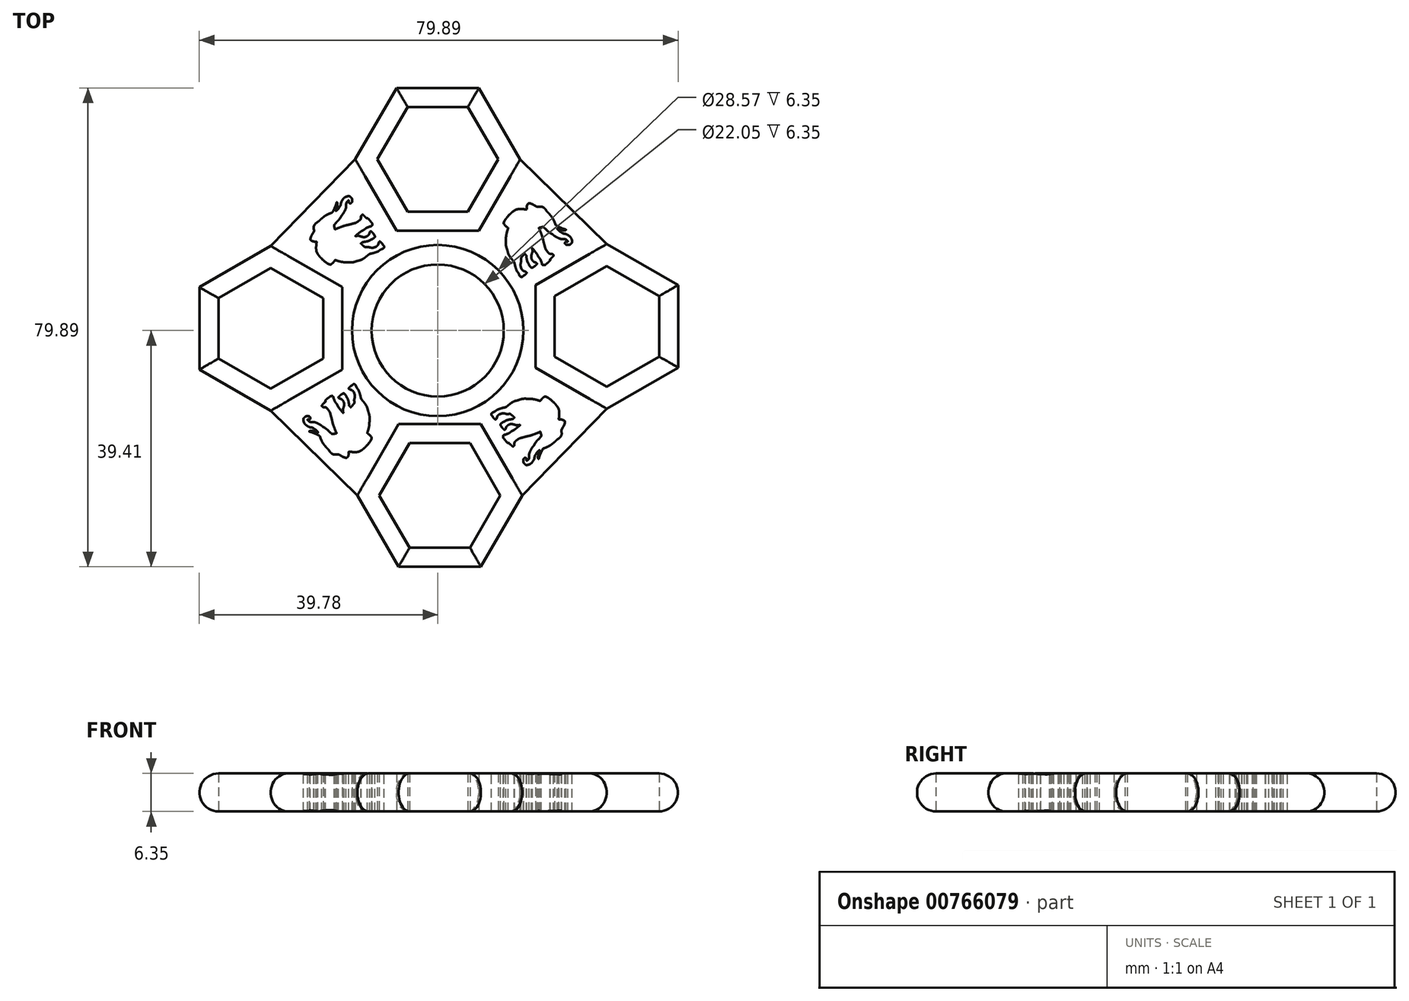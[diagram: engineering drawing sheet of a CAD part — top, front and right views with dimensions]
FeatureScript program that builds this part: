
annotation { "Feature Type Name" : "Feature", "Feature Type Description" : "" }
export const myFeature = defineFeature(function(context is Context, id is Id, definition is map)
    precondition{}
    {
        {
            var Q0;
            Q0=qCreatedBy(makeId("Top.planeOp"),FACE);
            var sketch = newSketch(context, id + "F0", { "sketchPlane" : qUnion([Q0])});
            skCircle(sketch, "E0", {"center": v(0, 0) * mm, "radius": 11.02 * mm});
            skCircle(sketch, "E1", {"center": v(0, 0) * mm, "radius": 14.29 * mm});
            skCircle(sketch, "E2.cCircle", {"center": v(0, 28.58) * mm, "radius": 8.73 * mm, "construction": true});
            skLineSegment(sketch, "E2.0", {"start": v(5.04, 19.84) * mm, "end": v(-5.04, 19.84) * mm});
            skLineSegment(sketch, "E2.1", {"start": v(-5.04, 19.84) * mm, "end": v(-10.08, 28.58) * mm});
            skLineSegment(sketch, "E2.2", {"start": v(-10.08, 28.58) * mm, "end": v(-5.04, 37.3) * mm});
            skLineSegment(sketch, "E2.3", {"start": v(-5.04, 37.3) * mm, "end": v(5.04, 37.3) * mm});
            skLineSegment(sketch, "E2.4", {"start": v(5.04, 37.3) * mm, "end": v(10.08, 28.57) * mm});
            skLineSegment(sketch, "E2.5", {"start": v(10.08, 28.58) * mm, "end": v(5.04, 19.84) * mm});
            skPoint(sketch, "E2.0.midPoint", {"position": v(0, 19.84) * mm});
            skCircle(sketch, "E3.cCircle", {"center": v(0, 28.58) * mm, "radius": 11.9 * mm, "construction": true});
            skLineSegment(sketch, "E3.0", {"start": v(6.87, 16.67) * mm, "end": v(-6.87, 16.67) * mm});
            skLineSegment(sketch, "E3.1", {"start": v(-6.87, 16.67) * mm, "end": v(-13.75, 28.57) * mm});
            skLineSegment(sketch, "E3.2", {"start": v(-13.75, 28.57) * mm, "end": v(-6.87, 40.48) * mm});
            skLineSegment(sketch, "E3.3", {"start": v(-6.87, 40.48) * mm, "end": v(6.87, 40.48) * mm});
            skLineSegment(sketch, "E3.4", {"start": v(6.87, 40.48) * mm, "end": v(13.75, 28.58) * mm});
            skLineSegment(sketch, "E3.5", {"start": v(13.75, 28.58) * mm, "end": v(6.87, 16.67) * mm});
            skPoint(sketch, "E3.0.midPoint", {"position": v(0, 16.67) * mm});
            skLineSegment(sketch, "E4.1.0", {"start": v(-39.78, 7.24) * mm, "end": v(-27.87, 14.11) * mm});
            skLineSegment(sketch, "E4.1.1", {"start": v(-27.87, 14.11) * mm, "end": v(-15.96, 7.24) * mm});
            skPoint(sketch, "E4.1.2", {"position": v(-15.96, 0.37) * mm});
            skCircle(sketch, "E4.1.3", {"center": v(-27.87, 0.37) * mm, "radius": 8.73 * mm, "construction": true});
            skCircle(sketch, "E4.1.4", {"center": v(-27.87, 0.37) * mm, "radius": 11.9 * mm, "construction": true});
            skLineSegment(sketch, "E4.1.5", {"start": v(-15.96, -6.5) * mm, "end": v(-27.87, -13.38) * mm});
            skLineSegment(sketch, "E4.1.6", {"start": v(-27.87, -13.38) * mm, "end": v(-39.78, -6.5) * mm});
            skPoint(sketch, "E4.1.7", {"position": v(-19.14, 0.37) * mm});
            skLineSegment(sketch, "E4.1.8", {"start": v(-36.6, -4.67) * mm, "end": v(-36.6, 5.4) * mm});
            skLineSegment(sketch, "E4.1.9", {"start": v(-39.78, -6.5) * mm, "end": v(-39.78, 7.24) * mm});
            skLineSegment(sketch, "E4.1.10", {"start": v(-19.14, -4.67) * mm, "end": v(-27.87, -9.72) * mm});
            skLineSegment(sketch, "E4.1.11", {"start": v(-27.87, -9.72) * mm, "end": v(-36.6, -4.67) * mm});
            skLineSegment(sketch, "E4.1.12", {"start": v(-19.14, 5.4) * mm, "end": v(-19.14, -4.67) * mm});
            skLineSegment(sketch, "E4.1.13", {"start": v(-36.6, 5.4) * mm, "end": v(-27.87, 10.45) * mm});
            skLineSegment(sketch, "E4.1.14", {"start": v(-27.87, 10.45) * mm, "end": v(-19.14, 5.4) * mm});
            skLineSegment(sketch, "E4.1.15", {"start": v(-15.96, 7.24) * mm, "end": v(-15.96, -6.5) * mm});
            skLineSegment(sketch, "E4.2.0", {"start": v(-6.54, -39.4) * mm, "end": v(-13.4, -27.5) * mm});
            skLineSegment(sketch, "E4.2.1", {"start": v(-13.4, -27.5) * mm, "end": v(-6.54, -15.6) * mm});
            skPoint(sketch, "E4.2.2", {"position": v(0.34, -15.6) * mm});
            skCircle(sketch, "E4.2.3", {"center": v(0.34, -27.5) * mm, "radius": 8.73 * mm, "construction": true});
            skCircle(sketch, "E4.2.4", {"center": v(0.34, -27.5) * mm, "radius": 11.9 * mm, "construction": true});
            skLineSegment(sketch, "E4.2.5", {"start": v(7.21, -15.6) * mm, "end": v(14.09, -27.5) * mm});
            skLineSegment(sketch, "E4.2.6", {"start": v(14.09, -27.5) * mm, "end": v(7.21, -39.4) * mm});
            skPoint(sketch, "E4.2.7", {"position": v(0.34, -18.77) * mm});
            skLineSegment(sketch, "E4.2.8", {"start": v(5.38, -36.23) * mm, "end": v(-4.7, -36.23) * mm});
            skLineSegment(sketch, "E4.2.9", {"start": v(7.21, -39.4) * mm, "end": v(-6.54, -39.4) * mm});
            skLineSegment(sketch, "E4.2.10", {"start": v(5.38, -18.77) * mm, "end": v(10.42, -27.5) * mm});
            skLineSegment(sketch, "E4.2.11", {"start": v(10.42, -27.5) * mm, "end": v(5.38, -36.23) * mm});
            skLineSegment(sketch, "E4.2.12", {"start": v(-4.7, -18.77) * mm, "end": v(5.38, -18.77) * mm});
            skLineSegment(sketch, "E4.2.13", {"start": v(-4.7, -36.23) * mm, "end": v(-9.74, -27.5) * mm});
            skLineSegment(sketch, "E4.2.14", {"start": v(-9.74, -27.5) * mm, "end": v(-4.7, -18.77) * mm});
            skLineSegment(sketch, "E4.2.15", {"start": v(-6.54, -15.6) * mm, "end": v(7.21, -15.6) * mm});
            skLineSegment(sketch, "E4.3.0", {"start": v(40.11, -6.17) * mm, "end": v(28.2, -13.04) * mm});
            skLineSegment(sketch, "E4.3.1", {"start": v(28.2, -13.04) * mm, "end": v(16.3, -6.17) * mm});
            skPoint(sketch, "E4.3.2", {"position": v(16.3, 0.7) * mm});
            skCircle(sketch, "E4.3.3", {"center": v(28.2, 0.7) * mm, "radius": 8.73 * mm, "construction": true});
            skCircle(sketch, "E4.3.4", {"center": v(28.2, 0.7) * mm, "radius": 11.9 * mm, "construction": true});
            skLineSegment(sketch, "E4.3.5", {"start": v(16.3, 7.58) * mm, "end": v(28.2, 14.45) * mm});
            skLineSegment(sketch, "E4.3.6", {"start": v(28.2, 14.45) * mm, "end": v(40.11, 7.58) * mm});
            skPoint(sketch, "E4.3.7", {"position": v(19.48, 0.7) * mm});
            skLineSegment(sketch, "E4.3.8", {"start": v(36.94, 5.75) * mm, "end": v(36.94, -4.34) * mm});
            skLineSegment(sketch, "E4.3.9", {"start": v(40.11, 7.58) * mm, "end": v(40.11, -6.17) * mm});
            skLineSegment(sketch, "E4.3.10", {"start": v(19.48, 5.75) * mm, "end": v(28.2, 10.79) * mm});
            skLineSegment(sketch, "E4.3.11", {"start": v(28.2, 10.79) * mm, "end": v(36.94, 5.75) * mm});
            skLineSegment(sketch, "E4.3.12", {"start": v(19.48, -4.34) * mm, "end": v(19.48, 5.75) * mm});
            skLineSegment(sketch, "E4.3.13", {"start": v(36.94, -4.34) * mm, "end": v(28.2, -9.38) * mm});
            skLineSegment(sketch, "E4.3.14", {"start": v(28.2, -9.38) * mm, "end": v(19.48, -4.34) * mm});
            skLineSegment(sketch, "E4.3.15", {"start": v(16.3, -6.17) * mm, "end": v(16.3, 7.58) * mm});
            skPoint(sketch, "E4.center", {"position": v(0.17, 0.54) * mm});
            skSolve(sketch);
        }
        {
            var Q0;
            Q0=qCreatedBy(makeId("Top.planeOp"),FACE);
            var sketch = newSketch(context, id + "F1", { "sketchPlane" : qUnion([Q0])});
            skLineSegment(sketch, "E5.0", {"start": v(6.87, 40.48) * mm, "end": v(13.75, 28.58) * mm});
            skLineSegment(sketch, "E5.1", {"start": v(-6.87, 40.48) * mm, "end": v(6.87, 40.48) * mm});
            skLineSegment(sketch, "E5.2", {"start": v(14.09, -27.5) * mm, "end": v(7.21, -39.4) * mm});
            skCircle(sketch, "E5.3", {"center": v(0, 28.58) * mm, "radius": 11.9 * mm});
            skLineSegment(sketch, "E5.4", {"start": v(-5.04, 19.84) * mm, "end": v(-10.08, 28.58) * mm});
            skLineSegment(sketch, "E5.5", {"start": v(10.08, 28.58) * mm, "end": v(5.04, 19.84) * mm});
            skLineSegment(sketch, "E5.6", {"start": v(40.11, 7.58) * mm, "end": v(40.11, -6.17) * mm});
            skLineSegment(sketch, "E5.7", {"start": v(5.04, 37.3) * mm, "end": v(10.08, 28.57) * mm});
            skLineSegment(sketch, "E5.8", {"start": v(-5.04, 37.3) * mm, "end": v(5.04, 37.3) * mm});
            skLineSegment(sketch, "E5.9", {"start": v(-10.08, 28.58) * mm, "end": v(-5.04, 37.3) * mm});
            skCircle(sketch, "E5.10", {"center": v(0, 28.58) * mm, "radius": 8.73 * mm});
            skCircle(sketch, "E5.11", {"center": v(0, 0) * mm, "radius": 14.29 * mm});
            skCircle(sketch, "E5.12", {"center": v(0, 0) * mm, "radius": 11.02 * mm});
            skLineSegment(sketch, "E5.13", {"start": v(13.75, 28.58) * mm, "end": v(6.87, 16.67) * mm});
            skLineSegment(sketch, "E5.14", {"start": v(6.87, 16.67) * mm, "end": v(-6.87, 16.67) * mm});
            skLineSegment(sketch, "E5.15", {"start": v(-6.87, 16.67) * mm, "end": v(-13.75, 28.57) * mm});
            skLineSegment(sketch, "E5.16", {"start": v(-13.75, 28.57) * mm, "end": v(-6.87, 40.48) * mm});
            skLineSegment(sketch, "E5.17", {"start": v(-6.54, -15.6) * mm, "end": v(7.21, -15.6) * mm});
            skLineSegment(sketch, "E5.18", {"start": v(-36.6, 5.4) * mm, "end": v(-27.87, 10.45) * mm});
            skLineSegment(sketch, "E5.19", {"start": v(36.94, -4.34) * mm, "end": v(28.2, -9.38) * mm});
            skLineSegment(sketch, "E5.20", {"start": v(-39.78, -6.5) * mm, "end": v(-39.78, 7.24) * mm});
            skLineSegment(sketch, "E5.21", {"start": v(10.42, -27.5) * mm, "end": v(5.38, -36.23) * mm});
            skLineSegment(sketch, "E5.22", {"start": v(-15.96, -6.5) * mm, "end": v(-27.87, -13.38) * mm});
            skLineSegment(sketch, "E5.23", {"start": v(19.48, 5.75) * mm, "end": v(28.2, 10.79) * mm});
            skLineSegment(sketch, "E5.24", {"start": v(28.2, -13.04) * mm, "end": v(16.3, -6.17) * mm});
            skLineSegment(sketch, "E5.25", {"start": v(-15.96, 7.24) * mm, "end": v(-15.96, -6.5) * mm});
            skLineSegment(sketch, "E5.26", {"start": v(5.38, -36.23) * mm, "end": v(-4.7, -36.23) * mm});
            skLineSegment(sketch, "E5.27", {"start": v(-39.78, 7.24) * mm, "end": v(-27.87, 14.11) * mm});
            skLineSegment(sketch, "E5.28", {"start": v(16.3, 7.58) * mm, "end": v(28.2, 14.45) * mm});
            skCircle(sketch, "E5.29", {"center": v(0.34, -27.5) * mm, "radius": 8.73 * mm});
            skLineSegment(sketch, "E5.30", {"start": v(40.11, -6.17) * mm, "end": v(28.2, -13.04) * mm});
            skLineSegment(sketch, "E5.31", {"start": v(-27.87, 10.45) * mm, "end": v(-19.14, 5.4) * mm});
            skLineSegment(sketch, "E5.32", {"start": v(28.2, -9.38) * mm, "end": v(19.48, -4.34) * mm});
            skLineSegment(sketch, "E5.33", {"start": v(-19.14, -4.67) * mm, "end": v(-27.87, -9.72) * mm});
            skLineSegment(sketch, "E5.34", {"start": v(-27.87, -13.38) * mm, "end": v(-39.78, -6.5) * mm});
            skCircle(sketch, "E5.35", {"center": v(28.2, 0.7) * mm, "radius": 8.73 * mm});
            skLineSegment(sketch, "E5.36", {"start": v(28.2, 10.79) * mm, "end": v(36.94, 5.75) * mm});
            skLineSegment(sketch, "E5.37", {"start": v(7.21, -39.4) * mm, "end": v(-6.54, -39.4) * mm});
            skLineSegment(sketch, "E5.38", {"start": v(-6.54, -39.4) * mm, "end": v(-13.4, -27.5) * mm});
            skLineSegment(sketch, "E5.39", {"start": v(-27.87, 14.11) * mm, "end": v(-15.96, 7.24) * mm});
            skLineSegment(sketch, "E5.40", {"start": v(28.2, 14.45) * mm, "end": v(40.11, 7.58) * mm});
            skCircle(sketch, "E5.41", {"center": v(0.34, -27.5) * mm, "radius": 11.9 * mm});
            skLineSegment(sketch, "E5.42", {"start": v(16.3, -6.17) * mm, "end": v(16.3, 7.58) * mm});
            skLineSegment(sketch, "E5.43", {"start": v(-4.7, -36.23) * mm, "end": v(-9.74, -27.5) * mm});
            skLineSegment(sketch, "E5.44", {"start": v(-27.87, -9.72) * mm, "end": v(-36.6, -4.67) * mm});
            skLineSegment(sketch, "E5.45", {"start": v(-36.6, -4.67) * mm, "end": v(-36.6, 5.4) * mm});
            skCircle(sketch, "E5.46", {"center": v(28.2, 0.7) * mm, "radius": 11.9 * mm});
            skLineSegment(sketch, "E5.47", {"start": v(-13.4, -27.5) * mm, "end": v(-6.54, -15.6) * mm});
            skLineSegment(sketch, "E5.48", {"start": v(5.38, -18.77) * mm, "end": v(10.42, -27.5) * mm});
            skCircle(sketch, "E5.49", {"center": v(-27.87, 0.37) * mm, "radius": 8.73 * mm});
            skLineSegment(sketch, "E5.50", {"start": v(36.94, 5.75) * mm, "end": v(36.94, -4.34) * mm});
            skLineSegment(sketch, "E5.51", {"start": v(7.21, -15.6) * mm, "end": v(14.09, -27.5) * mm});
            skCircle(sketch, "E5.52", {"center": v(-27.87, 0.37) * mm, "radius": 11.9 * mm});
            skLineSegment(sketch, "E5.53", {"start": v(-9.74, -27.5) * mm, "end": v(-4.7, -18.77) * mm});
            skLineSegment(sketch, "E5.54", {"start": v(-4.7, -18.77) * mm, "end": v(5.38, -18.77) * mm});
            skLineSegment(sketch, "E6", {"start": v(-27.87, 14.11) * mm, "end": v(-13.75, 28.58) * mm});
            skLineSegment(sketch, "E7", {"start": v(13.75, 28.58) * mm, "end": v(28.2, 14.45) * mm});
            skLineSegment(sketch, "E8", {"start": v(28.2, -13.04) * mm, "end": v(14.09, -27.5) * mm});
            skLineSegment(sketch, "E9", {"start": v(-13.4, -27.5) * mm, "end": v(-27.87, -13.38) * mm});
            skSolve(sketch);
        }
        {
            var Q0;
            Q0=makeQuery(id+"F1.imprint","IMPRINT",FACE,{"disambiguationData":[TD([[makeQuery(id+"F1.imprint","IMPRINT",EDGE,{"derivedFrom":sQuery(id+"F1.wireOp",EDGE,"E5.11")}),-1.0]])]});
            var Q1;
            Q1=makeQuery(id+"F0.imprint","IMPRINT",FACE,{"disambiguationData":[TD([[makeQuery(id+"F0.imprint","IMPRINT",EDGE,{"derivedFrom":sQuery(id+"F0.wireOp",EDGE,"E0")}),-1.0]])]});
            var Q2;
            Q2=makeQuery(id+"F0.imprint","IMPRINT",FACE,{"disambiguationData":[TD([[makeQuery(id+"F0.imprint","IMPRINT",EDGE,{"derivedFrom":sQuery(id+"F0.wireOp",EDGE,"E2.0")}),1.0]])]});
            var Q3;
            Q3=makeQuery(id+"F0.imprint","IMPRINT",FACE,{"disambiguationData":[TD([[makeQuery(id+"F0.imprint","IMPRINT",EDGE,{"derivedFrom":sQuery(id+"F0.wireOp",EDGE,"E4.1.0")}),-1.0]])]});
            var Q4;
            Q4=makeQuery(id+"F0.imprint","IMPRINT",FACE,{"disambiguationData":[TD([[makeQuery(id+"F0.imprint","IMPRINT",EDGE,{"derivedFrom":sQuery(id+"F0.wireOp",EDGE,"E4.3.0")}),-1.0]])]});
            var Q5;
            Q5=makeQuery(id+"F0.imprint","IMPRINT",FACE,{"disambiguationData":[TD([[makeQuery(id+"F0.imprint","IMPRINT",EDGE,{"derivedFrom":sQuery(id+"F0.wireOp",EDGE,"E4.2.0")}),-1.0]])]});
            extrude(context, id + "F2", {"entities" : qUnion([Q0, Q1, Q2, Q3, Q4, Q5]), "depth" : 6.35 * mm, "offsetDistance" : 25.4 * mm});
        }
        {
            var Q0;
            Q0=makeQuery(id+"F2.opExtrude","CAP_FACE",FACE,{"disambiguationData":[OSD([sQuery(id+"F1.wireOp",EDGE,"E5.11"),sQuery(id+"F1.wireOp",EDGE,"E5.13"),sQuery(id+"F1.wireOp",EDGE,"E5.14"),sQuery(id+"F1.wireOp",EDGE,"E5.15"),sQuery(id+"F1.wireOp",EDGE,"E5.17"),sQuery(id+"F1.wireOp",EDGE,"E5.22"),sQuery(id+"F1.wireOp",EDGE,"E5.24"),sQuery(id+"F1.wireOp",EDGE,"E5.25"),sQuery(id+"F1.wireOp",EDGE,"E5.28"),sQuery(id+"F1.wireOp",EDGE,"E5.39"),sQuery(id+"F1.wireOp",EDGE,"E5.42"),sQuery(id+"F1.wireOp",EDGE,"E5.47"),sQuery(id+"F1.wireOp",EDGE,"E5.51"),sQuery(id+"F1.wireOp",EDGE,"E6"),sQuery(id+"F1.wireOp",EDGE,"E7"),sQuery(id+"F1.wireOp",EDGE,"E8"),sQuery(id+"F1.wireOp",EDGE,"E9")])],"isStart":false});
            var sketch = newSketch(context, id + "F3", { "sketchPlane" : qUnion([Q0])});
            skArc(sketch, "E10", {"start": v(12.38, 19.72) * mm, "mid": v(12.3, 19.64) * mm, "end": v(12.2, 19.56) * mm});
            skArc(sketch, "E11", {"start": v(12.2, 19.56) * mm, "mid": v(12.12, 19.49) * mm, "end": v(12.04, 19.41) * mm});
            skArc(sketch, "E12", {"start": v(12.04, 19.41) * mm, "mid": v(11.7, 19.04) * mm, "end": v(11.37, 18.64) * mm});
            skArc(sketch, "E13", {"start": v(11.37, 18.64) * mm, "mid": v(11.27, 18.5) * mm, "end": v(11.18, 18.35) * mm});
            skArc(sketch, "E14", {"start": v(11.18, 18.35) * mm, "mid": v(11.11, 18.22) * mm, "end": v(11.06, 18.09) * mm});
            skArc(sketch, "E15", {"start": v(11.06, 18.09) * mm, "mid": v(11.04, 18.03) * mm, "end": v(11.03, 17.97) * mm});
            skArc(sketch, "E16", {"start": v(11.03, 17.97) * mm, "mid": v(11.02, 17.93) * mm, "end": v(11.02, 17.9) * mm});
            skArc(sketch, "E17", {"start": v(11.02, 17.9) * mm, "mid": v(11.03, 17.87) * mm, "end": v(11.04, 17.84) * mm});
            skArc(sketch, "E18", {"start": v(11.04, 17.84) * mm, "mid": v(11.07, 17.77) * mm, "end": v(11.1, 17.71) * mm});
            skArc(sketch, "E19", {"start": v(11.1, 17.71) * mm, "mid": v(11.22, 17.57) * mm, "end": v(11.34, 17.44) * mm});
            skArc(sketch, "E20", {"start": v(11.34, 17.44) * mm, "mid": v(11.4, 17.4) * mm, "end": v(11.45, 17.34) * mm});
            skArc(sketch, "E21", {"start": v(11.45, 17.34) * mm, "mid": v(11.53, 17.28) * mm, "end": v(11.6, 17.22) * mm});
            skArc(sketch, "E22", {"start": v(11.6, 17.22) * mm, "mid": v(11.66, 17.18) * mm, "end": v(11.73, 17.14) * mm});
            skArc(sketch, "E23", {"start": v(11.73, 17.14) * mm, "mid": v(11.74, 17.13) * mm, "end": v(11.75, 17.12) * mm});
            skArc(sketch, "E24", {"start": v(11.75, 17.12) * mm, "mid": v(11.75, 17.1) * mm, "end": v(11.75, 17.08) * mm});
            skArc(sketch, "E25", {"start": v(11.75, 17.08) * mm, "mid": v(11.73, 17.04) * mm, "end": v(11.72, 16.99) * mm});
            skArc(sketch, "E26", {"start": v(11.72, 16.99) * mm, "mid": v(11.7, 16.96) * mm, "end": v(11.7, 16.93) * mm});
            skArc(sketch, "E27", {"start": v(11.7, 16.93) * mm, "mid": v(11.7, 16.9) * mm, "end": v(11.68, 16.87) * mm});
            skArc(sketch, "E28", {"start": v(11.68, 16.87) * mm, "mid": v(11.67, 16.83) * mm, "end": v(11.66, 16.79) * mm});
            skArc(sketch, "E29", {"start": v(11.66, 16.79) * mm, "mid": v(11.66, 16.77) * mm, "end": v(11.65, 16.75) * mm});
            skArc(sketch, "E30", {"start": v(11.65, 16.75) * mm, "mid": v(11.64, 16.72) * mm, "end": v(11.62, 16.68) * mm});
            skArc(sketch, "E31", {"start": v(11.62, 16.68) * mm, "mid": v(11.62, 16.67) * mm, "end": v(11.62, 16.66) * mm});
            skArc(sketch, "E32", {"start": v(11.62, 16.66) * mm, "mid": v(11.55, 16.4) * mm, "end": v(11.48, 16.15) * mm});
            skArc(sketch, "E33", {"start": v(11.48, 16.15) * mm, "mid": v(11.43, 15.87) * mm, "end": v(11.4, 15.59) * mm});
            skArc(sketch, "E34", {"start": v(11.4, 15.59) * mm, "mid": v(11.4, 15.48) * mm, "end": v(11.4, 15.37) * mm});
            skArc(sketch, "E35", {"start": v(11.4, 15.37) * mm, "mid": v(11.38, 15.13) * mm, "end": v(11.38, 14.9) * mm});
            skArc(sketch, "E36", {"start": v(11.38, 14.9) * mm, "mid": v(11.38, 14.82) * mm, "end": v(11.37, 14.75) * mm});
            skArc(sketch, "E37", {"start": v(11.37, 14.75) * mm, "mid": v(11.36, 14.62) * mm, "end": v(11.37, 14.5) * mm});
            skArc(sketch, "E38", {"start": v(11.37, 14.5) * mm, "mid": v(11.38, 14.34) * mm, "end": v(11.4, 14.18) * mm});
            skArc(sketch, "E39", {"start": v(11.4, 14.18) * mm, "mid": v(11.42, 14.03) * mm, "end": v(11.47, 13.89) * mm});
            skArc(sketch, "E40", {"start": v(11.47, 13.89) * mm, "mid": v(11.59, 13.52) * mm, "end": v(11.69, 13.15) * mm});
            skArc(sketch, "E41", {"start": v(11.69, 13.15) * mm, "mid": v(11.71, 13.05) * mm, "end": v(11.74, 12.96) * mm});
            skArc(sketch, "E42", {"start": v(11.74, 12.96) * mm, "mid": v(11.77, 12.86) * mm, "end": v(11.8, 12.77) * mm});
            skArc(sketch, "E43", {"start": v(11.8, 12.77) * mm, "mid": v(11.83, 12.72) * mm, "end": v(11.85, 12.66) * mm});
            skArc(sketch, "E44", {"start": v(11.85, 12.66) * mm, "mid": v(11.88, 12.6) * mm, "end": v(11.92, 12.55) * mm});
            skArc(sketch, "E45", {"start": v(11.92, 12.55) * mm, "mid": v(11.97, 12.45) * mm, "end": v(12.03, 12.36) * mm});
            skArc(sketch, "E46", {"start": v(12.03, 12.36) * mm, "mid": v(12.06, 12.3) * mm, "end": v(12.1, 12.24) * mm});
            skArc(sketch, "E47", {"start": v(12.1, 12.24) * mm, "mid": v(12.3, 12) * mm, "end": v(12.49, 11.75) * mm});
            skArc(sketch, "E48", {"start": v(12.49, 11.75) * mm, "mid": v(12.6, 11.63) * mm, "end": v(12.7, 11.51) * mm});
            skArc(sketch, "E49", {"start": v(12.7, 11.51) * mm, "mid": v(12.72, 11.48) * mm, "end": v(12.74, 11.45) * mm});
            skArc(sketch, "E50", {"start": v(12.74, 11.45) * mm, "mid": v(12.75, 11.43) * mm, "end": v(12.75, 11.41) * mm});
            skArc(sketch, "E51", {"start": v(12.75, 11.41) * mm, "mid": v(12.78, 11.33) * mm, "end": v(12.8, 11.26) * mm});
            skArc(sketch, "E52", {"start": v(12.8, 11.26) * mm, "mid": v(12.84, 11.15) * mm, "end": v(12.87, 11.03) * mm});
            skArc(sketch, "E53", {"start": v(12.87, 11.03) * mm, "mid": v(12.9, 10.92) * mm, "end": v(12.92, 10.8) * mm});
            skArc(sketch, "E54", {"start": v(12.92, 10.8) * mm, "mid": v(12.93, 10.74) * mm, "end": v(12.95, 10.68) * mm});
            skArc(sketch, "E55", {"start": v(12.95, 10.68) * mm, "mid": v(13, 10.51) * mm, "end": v(13.06, 10.34) * mm});
            skArc(sketch, "E56", {"start": v(13.06, 10.34) * mm, "mid": v(13.12, 10.17) * mm, "end": v(13.19, 10) * mm});
            skArc(sketch, "E57", {"start": v(13.19, 10) * mm, "mid": v(13.22, 9.93) * mm, "end": v(13.26, 9.87) * mm});
            skArc(sketch, "E58", {"start": v(13.26, 9.87) * mm, "mid": v(13.28, 9.84) * mm, "end": v(13.31, 9.8) * mm});
            skArc(sketch, "E59", {"start": v(13.31, 9.8) * mm, "mid": v(13.41, 9.67) * mm, "end": v(13.5, 9.53) * mm});
            skArc(sketch, "E60", {"start": v(13.5, 9.53) * mm, "mid": v(13.53, 9.47) * mm, "end": v(13.55, 9.41) * mm});
            skArc(sketch, "E61", {"start": v(13.55, 9.41) * mm, "mid": v(13.58, 9.36) * mm, "end": v(13.6, 9.3) * mm});
            skArc(sketch, "E62", {"start": v(13.6, 9.3) * mm, "mid": v(13.63, 9.26) * mm, "end": v(13.66, 9.21) * mm});
            skArc(sketch, "E63", {"start": v(13.66, 9.21) * mm, "mid": v(13.67, 9.18) * mm, "end": v(13.68, 9.15) * mm});
            skArc(sketch, "E64", {"start": v(13.68, 9.15) * mm, "mid": v(13.7, 9.12) * mm, "end": v(13.7, 9.1) * mm});
            skArc(sketch, "E65", {"start": v(13.7, 9.1) * mm, "mid": v(13.72, 9.07) * mm, "end": v(13.74, 9.04) * mm});
            skArc(sketch, "E66", {"start": v(13.74, 9.04) * mm, "mid": v(13.77, 9.01) * mm, "end": v(13.81, 8.98) * mm});
            skArc(sketch, "E67", {"start": v(13.81, 8.98) * mm, "mid": v(13.84, 8.97) * mm, "end": v(13.88, 8.96) * mm});
            skArc(sketch, "E68", {"start": v(13.88, 8.96) * mm, "mid": v(13.9, 8.96) * mm, "end": v(13.92, 8.95) * mm});
            skArc(sketch, "E69", {"start": v(13.92, 8.95) * mm, "mid": v(13.94, 8.95) * mm, "end": v(13.96, 8.95) * mm});
            skArc(sketch, "E70", {"start": v(13.96, 8.95) * mm, "mid": v(13.99, 8.94) * mm, "end": v(14.02, 8.94) * mm});
            skArc(sketch, "E71", {"start": v(14.02, 8.94) * mm, "mid": v(14.05, 8.95) * mm, "end": v(14.08, 8.96) * mm});
            skArc(sketch, "E72", {"start": v(14.08, 8.96) * mm, "mid": v(14.1, 8.97) * mm, "end": v(14.12, 9) * mm});
            skArc(sketch, "E73", {"start": v(14.12, 9) * mm, "mid": v(14.16, 9.02) * mm, "end": v(14.2, 9.06) * mm});
            skArc(sketch, "E74", {"start": v(14.2, 9.06) * mm, "mid": v(14.24, 9.1) * mm, "end": v(14.28, 9.12) * mm});
            skArc(sketch, "E75", {"start": v(14.28, 9.12) * mm, "mid": v(14.36, 9.17) * mm, "end": v(14.45, 9.22) * mm});
            skArc(sketch, "E76", {"start": v(14.45, 9.22) * mm, "mid": v(14.5, 9.26) * mm, "end": v(14.56, 9.3) * mm});
            skArc(sketch, "E77", {"start": v(14.56, 9.3) * mm, "mid": v(14.6, 9.34) * mm, "end": v(14.64, 9.38) * mm});
            skArc(sketch, "E78", {"start": v(14.64, 9.38) * mm, "mid": v(14.68, 9.42) * mm, "end": v(14.72, 9.46) * mm});
            skArc(sketch, "E79", {"start": v(14.72, 9.46) * mm, "mid": v(14.75, 9.48) * mm, "end": v(14.77, 9.51) * mm});
            skArc(sketch, "E80", {"start": v(14.77, 9.51) * mm, "mid": v(14.8, 9.56) * mm, "end": v(14.81, 9.6) * mm});
            skArc(sketch, "E81", {"start": v(14.81, 9.6) * mm, "mid": v(14.82, 9.6) * mm, "end": v(14.83, 9.62) * mm});
            skArc(sketch, "E82", {"start": v(14.83, 9.62) * mm, "mid": v(14.84, 9.63) * mm, "end": v(14.85, 9.64) * mm});
            skArc(sketch, "E83", {"start": v(14.85, 9.64) * mm, "mid": v(14.86, 9.65) * mm, "end": v(14.86, 9.66) * mm});
            skArc(sketch, "E84", {"start": v(14.86, 9.66) * mm, "mid": v(14.86, 9.67) * mm, "end": v(14.85, 9.69) * mm});
            skArc(sketch, "E85", {"start": v(14.85, 9.69) * mm, "mid": v(14.8, 9.74) * mm, "end": v(14.75, 9.79) * mm});
            skArc(sketch, "E86", {"start": v(14.75, 9.79) * mm, "mid": v(14.7, 9.82) * mm, "end": v(14.65, 9.83) * mm});
            skArc(sketch, "E87", {"start": v(14.65, 9.83) * mm, "mid": v(14.62, 9.83) * mm, "end": v(14.6, 9.84) * mm});
            skArc(sketch, "E88", {"start": v(14.6, 9.84) * mm, "mid": v(14.56, 9.85) * mm, "end": v(14.53, 9.87) * mm});
            skArc(sketch, "E89", {"start": v(14.53, 9.87) * mm, "mid": v(14.47, 9.9) * mm, "end": v(14.41, 9.91) * mm});
            skArc(sketch, "E90", {"start": v(14.41, 9.91) * mm, "mid": v(14.37, 9.93) * mm, "end": v(14.32, 9.95) * mm});
            skArc(sketch, "E91", {"start": v(14.32, 9.95) * mm, "mid": v(14.26, 9.98) * mm, "end": v(14.21, 10.02) * mm});
            skArc(sketch, "E92", {"start": v(14.21, 10.02) * mm, "mid": v(14.17, 10.05) * mm, "end": v(14.13, 10.1) * mm});
            skArc(sketch, "E93", {"start": v(14.13, 10.1) * mm, "mid": v(14.07, 10.16) * mm, "end": v(14.02, 10.23) * mm});
            skArc(sketch, "E94", {"start": v(14.02, 10.23) * mm, "mid": v(14, 10.26) * mm, "end": v(13.98, 10.28) * mm});
            skArc(sketch, "E95", {"start": v(13.98, 10.28) * mm, "mid": v(13.98, 10.3) * mm, "end": v(13.97, 10.32) * mm});
            skArc(sketch, "E96", {"start": v(13.97, 10.32) * mm, "mid": v(13.96, 10.34) * mm, "end": v(13.95, 10.36) * mm});
            skArc(sketch, "E97", {"start": v(13.95, 10.36) * mm, "mid": v(13.94, 10.4) * mm, "end": v(13.92, 10.45) * mm});
            skArc(sketch, "E98", {"start": v(13.92, 10.45) * mm, "mid": v(13.87, 10.6) * mm, "end": v(13.84, 10.74) * mm});
            skArc(sketch, "E99", {"start": v(13.84, 10.74) * mm, "mid": v(13.82, 10.96) * mm, "end": v(13.84, 11.19) * mm});
            skArc(sketch, "E100", {"start": v(13.84, 11.19) * mm, "mid": v(13.87, 11.3) * mm, "end": v(13.9, 11.4) * mm});
            skArc(sketch, "E101", {"start": v(13.9, 11.4) * mm, "mid": v(13.91, 11.46) * mm, "end": v(13.93, 11.52) * mm});
            skArc(sketch, "E102", {"start": v(13.93, 11.52) * mm, "mid": v(13.93, 11.59) * mm, "end": v(13.93, 11.66) * mm});
            skArc(sketch, "E103", {"start": v(13.93, 11.66) * mm, "mid": v(13.93, 11.72) * mm, "end": v(13.92, 11.78) * mm});
            skArc(sketch, "E104", {"start": v(13.92, 11.78) * mm, "mid": v(13.91, 11.86) * mm, "end": v(13.9, 11.94) * mm});
            skArc(sketch, "E105", {"start": v(13.9, 11.94) * mm, "mid": v(13.9, 11.98) * mm, "end": v(13.9, 12.03) * mm});
            skArc(sketch, "E106", {"start": v(13.9, 12.03) * mm, "mid": v(13.93, 12.12) * mm, "end": v(13.97, 12.2) * mm});
            skArc(sketch, "E107", {"start": v(13.97, 12.2) * mm, "mid": v(14.01, 12.25) * mm, "end": v(14.06, 12.3) * mm});
            skArc(sketch, "E108", {"start": v(14.06, 12.3) * mm, "mid": v(14.1, 12.35) * mm, "end": v(14.14, 12.4) * mm});
            skArc(sketch, "E109", {"start": v(14.14, 12.4) * mm, "mid": v(14.16, 12.42) * mm, "end": v(14.18, 12.44) * mm});
            skArc(sketch, "E110", {"start": v(14.18, 12.44) * mm, "mid": v(14.3, 12.58) * mm, "end": v(14.4, 12.7) * mm});
            skArc(sketch, "E111", {"start": v(14.4, 12.7) * mm, "mid": v(14.43, 12.74) * mm, "end": v(14.46, 12.77) * mm});
            skArc(sketch, "E112", {"start": v(14.46, 12.77) * mm, "mid": v(14.48, 12.79) * mm, "end": v(14.5, 12.8) * mm});
            skArc(sketch, "E113", {"start": v(14.5, 12.8) * mm, "mid": v(14.51, 12.8) * mm, "end": v(14.53, 12.8) * mm});
            skArc(sketch, "E114", {"start": v(14.53, 12.8) * mm, "mid": v(14.55, 12.8) * mm, "end": v(14.56, 12.79) * mm});
            skArc(sketch, "E115", {"start": v(14.56, 12.79) * mm, "mid": v(14.59, 12.76) * mm, "end": v(14.6, 12.73) * mm});
            skArc(sketch, "E116", {"start": v(14.6, 12.73) * mm, "mid": v(14.62, 12.7) * mm, "end": v(14.64, 12.69) * mm});
            skArc(sketch, "E117", {"start": v(14.64, 12.69) * mm, "mid": v(14.65, 12.66) * mm, "end": v(14.67, 12.64) * mm});
            skArc(sketch, "E118", {"start": v(14.67, 12.64) * mm, "mid": v(14.7, 12.6) * mm, "end": v(14.73, 12.57) * mm});
            skArc(sketch, "E119", {"start": v(14.73, 12.57) * mm, "mid": v(14.75, 12.55) * mm, "end": v(14.77, 12.52) * mm});
            skArc(sketch, "E120", {"start": v(14.77, 12.52) * mm, "mid": v(14.77, 12.5) * mm, "end": v(14.78, 12.48) * mm});
            skArc(sketch, "E121", {"start": v(14.78, 12.48) * mm, "mid": v(14.78, 12.43) * mm, "end": v(14.78, 12.39) * mm});
            skArc(sketch, "E122", {"start": v(14.78, 12.39) * mm, "mid": v(14.79, 12.33) * mm, "end": v(14.8, 12.28) * mm});
            skArc(sketch, "E123", {"start": v(14.8, 12.28) * mm, "mid": v(14.82, 12.14) * mm, "end": v(14.84, 12) * mm});
            skArc(sketch, "E124", {"start": v(14.84, 12) * mm, "mid": v(14.88, 11.82) * mm, "end": v(14.92, 11.65) * mm});
            skArc(sketch, "E125", {"start": v(14.92, 11.65) * mm, "mid": v(14.94, 11.57) * mm, "end": v(14.97, 11.5) * mm});
            skArc(sketch, "E126", {"start": v(14.97, 11.5) * mm, "mid": v(14.99, 11.48) * mm, "end": v(15, 11.45) * mm});
            skArc(sketch, "E127", {"start": v(15, 11.45) * mm, "mid": v(15.01, 11.43) * mm, "end": v(15.02, 11.4) * mm});
            skArc(sketch, "E128", {"start": v(15.02, 11.4) * mm, "mid": v(15.03, 11.37) * mm, "end": v(15.05, 11.34) * mm});
            skArc(sketch, "E129", {"start": v(15.05, 11.34) * mm, "mid": v(15.06, 11.32) * mm, "end": v(15.07, 11.3) * mm});
            skArc(sketch, "E130", {"start": v(15.07, 11.3) * mm, "mid": v(15.09, 11.27) * mm, "end": v(15.1, 11.25) * mm});
            skArc(sketch, "E131", {"start": v(15.1, 11.25) * mm, "mid": v(15.12, 11.23) * mm, "end": v(15.13, 11.21) * mm});
            skArc(sketch, "E132", {"start": v(15.13, 11.21) * mm, "mid": v(15.18, 11.12) * mm, "end": v(15.22, 11.02) * mm});
            skArc(sketch, "E133", {"start": v(15.22, 11.02) * mm, "mid": v(15.25, 10.96) * mm, "end": v(15.27, 10.91) * mm});
            skArc(sketch, "E134", {"start": v(15.27, 10.91) * mm, "mid": v(15.3, 10.88) * mm, "end": v(15.32, 10.84) * mm});
            skArc(sketch, "E135", {"start": v(15.32, 10.84) * mm, "mid": v(15.37, 10.78) * mm, "end": v(15.4, 10.71) * mm});
            skArc(sketch, "E136", {"start": v(15.4, 10.71) * mm, "mid": v(15.45, 10.66) * mm, "end": v(15.49, 10.6) * mm});
            skArc(sketch, "E137", {"start": v(15.49, 10.6) * mm, "mid": v(15.54, 10.54) * mm, "end": v(15.61, 10.5) * mm});
            skArc(sketch, "E138", {"start": v(15.61, 10.5) * mm, "mid": v(15.64, 10.5) * mm, "end": v(15.67, 10.48) * mm});
            skArc(sketch, "E139", {"start": v(15.67, 10.48) * mm, "mid": v(15.7, 10.48) * mm, "end": v(15.72, 10.48) * mm});
            skArc(sketch, "E140", {"start": v(15.72, 10.48) * mm, "mid": v(15.77, 10.5) * mm, "end": v(15.82, 10.52) * mm});
            skArc(sketch, "E141", {"start": v(15.82, 10.52) * mm, "mid": v(15.95, 10.59) * mm, "end": v(16.08, 10.67) * mm});
            skArc(sketch, "E142", {"start": v(16.08, 10.67) * mm, "mid": v(16.15, 10.72) * mm, "end": v(16.23, 10.78) * mm});
            skArc(sketch, "E143", {"start": v(16.23, 10.78) * mm, "mid": v(16.32, 10.85) * mm, "end": v(16.4, 10.93) * mm});
            skArc(sketch, "E144", {"start": v(16.4, 10.93) * mm, "mid": v(16.47, 11) * mm, "end": v(16.53, 11.08) * mm});
            skArc(sketch, "E145", {"start": v(16.53, 11.08) * mm, "mid": v(16.55, 11.1) * mm, "end": v(16.56, 11.14) * mm});
            skArc(sketch, "E146", {"start": v(16.56, 11.14) * mm, "mid": v(16.57, 11.15) * mm, "end": v(16.57, 11.17) * mm});
            skArc(sketch, "E147", {"start": v(16.57, 11.17) * mm, "mid": v(16.57, 11.19) * mm, "end": v(16.56, 11.2) * mm});
            skArc(sketch, "E148", {"start": v(16.56, 11.2) * mm, "mid": v(16.55, 11.23) * mm, "end": v(16.53, 11.25) * mm});
            skArc(sketch, "E149", {"start": v(16.53, 11.25) * mm, "mid": v(16.46, 11.3) * mm, "end": v(16.39, 11.34) * mm});
            skArc(sketch, "E150", {"start": v(16.39, 11.34) * mm, "mid": v(16.35, 11.36) * mm, "end": v(16.3, 11.36) * mm});
            skArc(sketch, "E151", {"start": v(16.3, 11.36) * mm, "mid": v(16.26, 11.37) * mm, "end": v(16.22, 11.39) * mm});
            skArc(sketch, "E152", {"start": v(16.22, 11.39) * mm, "mid": v(16.2, 11.4) * mm, "end": v(16.16, 11.42) * mm});
            skArc(sketch, "E153", {"start": v(16.16, 11.42) * mm, "mid": v(16.13, 11.44) * mm, "end": v(16.1, 11.45) * mm});
            skArc(sketch, "E154", {"start": v(16.1, 11.45) * mm, "mid": v(16.07, 11.46) * mm, "end": v(16.04, 11.47) * mm});
            skArc(sketch, "E155", {"start": v(16.04, 11.47) * mm, "mid": v(16.01, 11.49) * mm, "end": v(15.99, 11.5) * mm});
            skArc(sketch, "E156", {"start": v(15.99, 11.5) * mm, "mid": v(15.96, 11.52) * mm, "end": v(15.94, 11.54) * mm});
            skArc(sketch, "E157", {"start": v(15.94, 11.54) * mm, "mid": v(15.9, 11.58) * mm, "end": v(15.87, 11.62) * mm});
            skArc(sketch, "E158", {"start": v(15.87, 11.62) * mm, "mid": v(15.83, 11.67) * mm, "end": v(15.8, 11.71) * mm});
            skArc(sketch, "E159", {"start": v(15.8, 11.71) * mm, "mid": v(15.72, 11.85) * mm, "end": v(15.66, 12) * mm});
            skArc(sketch, "E160", {"start": v(15.66, 12) * mm, "mid": v(15.64, 12.05) * mm, "end": v(15.62, 12.1) * mm});
            skArc(sketch, "E161", {"start": v(15.62, 12.1) * mm, "mid": v(15.61, 12.15) * mm, "end": v(15.6, 12.2) * mm});
            skArc(sketch, "E162", {"start": v(15.6, 12.2) * mm, "mid": v(15.6, 12.35) * mm, "end": v(15.62, 12.5) * mm});
            skArc(sketch, "E163", {"start": v(15.62, 12.5) * mm, "mid": v(15.65, 12.64) * mm, "end": v(15.69, 12.78) * mm});
            skArc(sketch, "E164", {"start": v(15.69, 12.78) * mm, "mid": v(15.73, 12.89) * mm, "end": v(15.77, 13) * mm});
            skArc(sketch, "E165", {"start": v(15.77, 13) * mm, "mid": v(15.79, 13.05) * mm, "end": v(15.8, 13.1) * mm});
            skArc(sketch, "E166", {"start": v(15.8, 13.1) * mm, "mid": v(15.81, 13.15) * mm, "end": v(15.82, 13.2) * mm});
            skArc(sketch, "E167", {"start": v(15.82, 13.2) * mm, "mid": v(15.82, 13.29) * mm, "end": v(15.81, 13.38) * mm});
            skArc(sketch, "E168", {"start": v(15.81, 13.38) * mm, "mid": v(15.8, 13.46) * mm, "end": v(15.79, 13.53) * mm});
            skArc(sketch, "E169", {"start": v(15.79, 13.53) * mm, "mid": v(15.78, 13.58) * mm, "end": v(15.76, 13.63) * mm});
            skArc(sketch, "E170", {"start": v(15.76, 13.63) * mm, "mid": v(15.75, 13.65) * mm, "end": v(15.74, 13.67) * mm});
            skArc(sketch, "E171", {"start": v(15.74, 13.67) * mm, "mid": v(15.74, 13.7) * mm, "end": v(15.75, 13.72) * mm});
            skArc(sketch, "E172", {"start": v(15.75, 13.72) * mm, "mid": v(15.76, 13.73) * mm, "end": v(15.78, 13.73) * mm});
            skArc(sketch, "E173", {"start": v(15.78, 13.73) * mm, "mid": v(15.8, 13.73) * mm, "end": v(15.81, 13.71) * mm});
            skArc(sketch, "E174", {"start": v(15.81, 13.71) * mm, "mid": v(15.83, 13.7) * mm, "end": v(15.84, 13.7) * mm});
            skArc(sketch, "E175", {"start": v(15.84, 13.7) * mm, "mid": v(15.88, 13.65) * mm, "end": v(15.92, 13.6) * mm});
            skArc(sketch, "E176", {"start": v(15.92, 13.6) * mm, "mid": v(15.95, 13.56) * mm, "end": v(15.99, 13.52) * mm});
            skArc(sketch, "E177", {"start": v(15.99, 13.52) * mm, "mid": v(16.13, 13.34) * mm, "end": v(16.28, 13.15) * mm});
            skArc(sketch, "E178", {"start": v(16.28, 13.15) * mm, "mid": v(16.4, 12.99) * mm, "end": v(16.53, 12.82) * mm});
            skArc(sketch, "E179", {"start": v(16.53, 12.82) * mm, "mid": v(16.59, 12.73) * mm, "end": v(16.64, 12.64) * mm});
            skArc(sketch, "E180", {"start": v(16.64, 12.64) * mm, "mid": v(16.67, 12.59) * mm, "end": v(16.7, 12.53) * mm});
            skArc(sketch, "E181", {"start": v(16.7, 12.53) * mm, "mid": v(16.75, 12.42) * mm, "end": v(16.8, 12.32) * mm});
            skArc(sketch, "E182", {"start": v(16.8, 12.32) * mm, "mid": v(16.86, 12.24) * mm, "end": v(16.93, 12.16) * mm});
            skArc(sketch, "E183", {"start": v(16.93, 12.16) * mm, "mid": v(16.99, 12.08) * mm, "end": v(17.05, 12) * mm});
            skArc(sketch, "E184", {"start": v(17.05, 12) * mm, "mid": v(17.08, 11.96) * mm, "end": v(17.12, 11.91) * mm});
            skArc(sketch, "E185", {"start": v(17.12, 11.91) * mm, "mid": v(17.16, 11.84) * mm, "end": v(17.19, 11.77) * mm});
            skArc(sketch, "E186", {"start": v(17.19, 11.77) * mm, "mid": v(17.2, 11.72) * mm, "end": v(17.22, 11.66) * mm});
            skArc(sketch, "E187", {"start": v(17.22, 11.66) * mm, "mid": v(17.24, 11.6) * mm, "end": v(17.27, 11.55) * mm});
            skArc(sketch, "E188", {"start": v(17.27, 11.55) * mm, "mid": v(17.29, 11.5) * mm, "end": v(17.3, 11.46) * mm});
            skArc(sketch, "E189", {"start": v(17.3, 11.46) * mm, "mid": v(17.33, 11.42) * mm, "end": v(17.35, 11.37) * mm});
            skArc(sketch, "E190", {"start": v(17.35, 11.37) * mm, "mid": v(17.36, 11.33) * mm, "end": v(17.37, 11.3) * mm});
            skArc(sketch, "E191", {"start": v(17.37, 11.3) * mm, "mid": v(17.38, 11.22) * mm, "end": v(17.4, 11.15) * mm});
            skArc(sketch, "E192", {"start": v(17.4, 11.15) * mm, "mid": v(17.4, 11.1) * mm, "end": v(17.43, 11.07) * mm});
            skArc(sketch, "E193", {"start": v(17.43, 11.07) * mm, "mid": v(17.46, 11) * mm, "end": v(17.52, 10.96) * mm});
            skArc(sketch, "E194", {"start": v(17.52, 10.96) * mm, "mid": v(17.55, 10.95) * mm, "end": v(17.58, 10.93) * mm});
            skArc(sketch, "E195", {"start": v(17.58, 10.93) * mm, "mid": v(17.6, 10.93) * mm, "end": v(17.63, 10.92) * mm});
            skArc(sketch, "E196", {"start": v(17.63, 10.92) * mm, "mid": v(17.67, 10.92) * mm, "end": v(17.7, 10.93) * mm});
            skArc(sketch, "E197", {"start": v(17.7, 10.93) * mm, "mid": v(17.74, 10.93) * mm, "end": v(17.78, 10.93) * mm});
            skArc(sketch, "E198", {"start": v(17.78, 10.93) * mm, "mid": v(17.82, 10.93) * mm, "end": v(17.86, 10.93) * mm});
            skArc(sketch, "E199", {"start": v(17.86, 10.93) * mm, "mid": v(17.9, 10.95) * mm, "end": v(17.95, 10.97) * mm});
            skArc(sketch, "E200", {"start": v(17.95, 10.97) * mm, "mid": v(17.97, 11) * mm, "end": v(18, 11.01) * mm});
            skArc(sketch, "E201", {"start": v(18, 11.01) * mm, "mid": v(18.04, 11.06) * mm, "end": v(18.08, 11.1) * mm});
            skArc(sketch, "E202", {"start": v(18.08, 11.1) * mm, "mid": v(18.12, 11.13) * mm, "end": v(18.16, 11.16) * mm});
            skArc(sketch, "E203", {"start": v(18.16, 11.16) * mm, "mid": v(18.3, 11.27) * mm, "end": v(18.46, 11.39) * mm});
            skArc(sketch, "E204", {"start": v(18.46, 11.39) * mm, "mid": v(18.56, 11.48) * mm, "end": v(18.66, 11.58) * mm});
            skArc(sketch, "E205", {"start": v(18.66, 11.58) * mm, "mid": v(18.7, 11.62) * mm, "end": v(18.72, 11.65) * mm});
            skArc(sketch, "E206", {"start": v(18.72, 11.65) * mm, "mid": v(18.73, 11.69) * mm, "end": v(18.74, 11.72) * mm});
            skArc(sketch, "E207", {"start": v(18.74, 11.72) * mm, "mid": v(18.75, 11.74) * mm, "end": v(18.75, 11.75) * mm});
            skArc(sketch, "E208", {"start": v(18.75, 11.75) * mm, "mid": v(18.77, 11.77) * mm, "end": v(18.78, 11.78) * mm});
            skArc(sketch, "E209", {"start": v(18.78, 11.78) * mm, "mid": v(18.8, 11.79) * mm, "end": v(18.8, 11.8) * mm});
            skArc(sketch, "E210", {"start": v(18.8, 11.8) * mm, "mid": v(18.79, 11.83) * mm, "end": v(18.77, 11.84) * mm});
            skArc(sketch, "E211", {"start": v(18.77, 11.84) * mm, "mid": v(18.76, 11.86) * mm, "end": v(18.75, 11.87) * mm});
            skArc(sketch, "E212", {"start": v(18.75, 11.87) * mm, "mid": v(18.74, 11.88) * mm, "end": v(18.74, 11.9) * mm});
            skArc(sketch, "E213", {"start": v(18.74, 11.9) * mm, "mid": v(18.74, 11.9) * mm, "end": v(18.75, 11.91) * mm});
            skArc(sketch, "E214", {"start": v(18.75, 11.91) * mm, "mid": v(18.76, 11.92) * mm, "end": v(18.77, 11.93) * mm});
            skArc(sketch, "E215", {"start": v(18.77, 11.93) * mm, "mid": v(18.82, 11.95) * mm, "end": v(18.87, 11.99) * mm});
            skArc(sketch, "E216", {"start": v(18.87, 11.99) * mm, "mid": v(18.93, 12.04) * mm, "end": v(18.98, 12.1) * mm});
            skArc(sketch, "E217", {"start": v(18.98, 12.1) * mm, "mid": v(19.02, 12.15) * mm, "end": v(19.07, 12.2) * mm});
            skArc(sketch, "E218", {"start": v(19.07, 12.2) * mm, "mid": v(19.12, 12.25) * mm, "end": v(19.17, 12.3) * mm});
            skArc(sketch, "E219", {"start": v(19.17, 12.3) * mm, "mid": v(19.21, 12.34) * mm, "end": v(19.25, 12.39) * mm});
            skArc(sketch, "E220", {"start": v(19.25, 12.39) * mm, "mid": v(19.27, 12.41) * mm, "end": v(19.29, 12.44) * mm});
            skArc(sketch, "E221", {"start": v(19.29, 12.44) * mm, "mid": v(19.3, 12.48) * mm, "end": v(19.32, 12.53) * mm});
            skArc(sketch, "E222", {"start": v(19.32, 12.53) * mm, "mid": v(19.33, 12.55) * mm, "end": v(19.33, 12.58) * mm});
            skArc(sketch, "E223", {"start": v(19.33, 12.58) * mm, "mid": v(19.33, 12.6) * mm, "end": v(19.32, 12.63) * mm});
            skArc(sketch, "E224", {"start": v(19.32, 12.63) * mm, "mid": v(19.3, 12.65) * mm, "end": v(19.29, 12.66) * mm});
            skArc(sketch, "E225", {"start": v(19.29, 12.66) * mm, "mid": v(19.25, 12.7) * mm, "end": v(19.2, 12.73) * mm});
            skArc(sketch, "E226", {"start": v(19.2, 12.73) * mm, "mid": v(19.16, 12.75) * mm, "end": v(19.12, 12.77) * mm});
            skArc(sketch, "E227", {"start": v(19.12, 12.77) * mm, "mid": v(19.07, 12.79) * mm, "end": v(19.02, 12.8) * mm});
            skArc(sketch, "E228", {"start": v(19.02, 12.8) * mm, "mid": v(19, 12.8) * mm, "end": v(18.97, 12.8) * mm});
            skArc(sketch, "E229", {"start": v(18.97, 12.8) * mm, "mid": v(18.92, 12.79) * mm, "end": v(18.88, 12.79) * mm});
            skArc(sketch, "E230", {"start": v(18.88, 12.79) * mm, "mid": v(18.83, 12.8) * mm, "end": v(18.77, 12.8) * mm});
            skArc(sketch, "E231", {"start": v(18.77, 12.8) * mm, "mid": v(18.71, 12.82) * mm, "end": v(18.66, 12.84) * mm});
            skArc(sketch, "E232", {"start": v(18.66, 12.84) * mm, "mid": v(18.59, 12.87) * mm, "end": v(18.53, 12.9) * mm});
            skArc(sketch, "E233", {"start": v(18.53, 12.9) * mm, "mid": v(18.5, 12.94) * mm, "end": v(18.47, 12.97) * mm});
            skArc(sketch, "E234", {"start": v(18.47, 12.97) * mm, "mid": v(18.43, 13.01) * mm, "end": v(18.4, 13.05) * mm});
            skArc(sketch, "E235", {"start": v(18.4, 13.05) * mm, "mid": v(18.37, 13.1) * mm, "end": v(18.34, 13.13) * mm});
            skArc(sketch, "E236", {"start": v(18.34, 13.13) * mm, "mid": v(18.28, 13.21) * mm, "end": v(18.22, 13.3) * mm});
            skArc(sketch, "E237", {"start": v(18.22, 13.3) * mm, "mid": v(18.14, 13.41) * mm, "end": v(18.06, 13.53) * mm});
            skArc(sketch, "E238", {"start": v(18.06, 13.53) * mm, "mid": v(18.01, 13.61) * mm, "end": v(17.98, 13.7) * mm});
            skArc(sketch, "E239", {"start": v(17.98, 13.7) * mm, "mid": v(17.94, 13.78) * mm, "end": v(17.92, 13.88) * mm});
            skArc(sketch, "E240", {"start": v(17.92, 13.88) * mm, "mid": v(17.9, 13.97) * mm, "end": v(17.87, 14.06) * mm});
            skArc(sketch, "E241", {"start": v(17.87, 14.06) * mm, "mid": v(17.85, 14.16) * mm, "end": v(17.82, 14.25) * mm});
            skArc(sketch, "E242", {"start": v(17.82, 14.25) * mm, "mid": v(17.78, 14.4) * mm, "end": v(17.74, 14.54) * mm});
            skArc(sketch, "E243", {"start": v(17.74, 14.54) * mm, "mid": v(17.7, 14.68) * mm, "end": v(17.66, 14.83) * mm});
            skArc(sketch, "E244", {"start": v(17.66, 14.83) * mm, "mid": v(17.64, 14.91) * mm, "end": v(17.63, 15) * mm});
            skArc(sketch, "E245", {"start": v(17.63, 15) * mm, "mid": v(17.56, 15.33) * mm, "end": v(17.46, 15.66) * mm});
            skArc(sketch, "E246", {"start": v(17.46, 15.66) * mm, "mid": v(17.42, 15.8) * mm, "end": v(17.37, 15.93) * mm});
            skArc(sketch, "E247", {"start": v(17.37, 15.93) * mm, "mid": v(17.24, 16.26) * mm, "end": v(17.12, 16.59) * mm});
            skArc(sketch, "E248", {"start": v(17.12, 16.59) * mm, "mid": v(17.06, 16.72) * mm, "end": v(17, 16.86) * mm});
            skArc(sketch, "E249", {"start": v(17, 16.86) * mm, "mid": v(16.95, 16.97) * mm, "end": v(16.9, 17.08) * mm});
            skArc(sketch, "E250", {"start": v(16.9, 17.08) * mm, "mid": v(16.89, 17.1) * mm, "end": v(16.88, 17.11) * mm});
            skArc(sketch, "E251", {"start": v(16.88, 17.11) * mm, "mid": v(16.88, 17.13) * mm, "end": v(16.9, 17.14) * mm});
            skArc(sketch, "E252", {"start": v(16.9, 17.14) * mm, "mid": v(16.9, 17.15) * mm, "end": v(16.9, 17.15) * mm});
            skArc(sketch, "E253", {"start": v(16.9, 17.15) * mm, "mid": v(16.95, 17.16) * mm, "end": v(17, 17.17) * mm});
            skArc(sketch, "E254", {"start": v(17, 17.17) * mm, "mid": v(17.09, 17.19) * mm, "end": v(17.18, 17.21) * mm});
            skArc(sketch, "E255", {"start": v(17.18, 17.21) * mm, "mid": v(17.28, 17.24) * mm, "end": v(17.37, 17.26) * mm});
            skArc(sketch, "E256", {"start": v(17.37, 17.26) * mm, "mid": v(17.43, 17.27) * mm, "end": v(17.48, 17.27) * mm});
            skArc(sketch, "E257", {"start": v(17.48, 17.27) * mm, "mid": v(17.53, 17.27) * mm, "end": v(17.58, 17.27) * mm});
            skArc(sketch, "E258", {"start": v(17.58, 17.27) * mm, "mid": v(17.62, 17.26) * mm, "end": v(17.65, 17.25) * mm});
            skArc(sketch, "E259", {"start": v(17.65, 17.25) * mm, "mid": v(17.67, 17.24) * mm, "end": v(17.7, 17.22) * mm});
            skArc(sketch, "E260", {"start": v(17.7, 17.22) * mm, "mid": v(17.72, 17.2) * mm, "end": v(17.74, 17.17) * mm});
            skArc(sketch, "E261", {"start": v(17.74, 17.17) * mm, "mid": v(17.79, 17.12) * mm, "end": v(17.83, 17.08) * mm});
            skArc(sketch, "E262", {"start": v(17.83, 17.08) * mm, "mid": v(17.9, 17.02) * mm, "end": v(17.97, 16.98) * mm});
            skArc(sketch, "E263", {"start": v(17.97, 16.98) * mm, "mid": v(18.05, 16.93) * mm, "end": v(18.1, 16.87) * mm});
            skArc(sketch, "E264", {"start": v(18.1, 16.87) * mm, "mid": v(18.13, 16.85) * mm, "end": v(18.14, 16.83) * mm});
            skArc(sketch, "E265", {"start": v(18.14, 16.83) * mm, "mid": v(18.22, 16.73) * mm, "end": v(18.3, 16.64) * mm});
            skArc(sketch, "E266", {"start": v(18.3, 16.64) * mm, "mid": v(18.43, 16.53) * mm, "end": v(18.56, 16.43) * mm});
            skArc(sketch, "E267", {"start": v(18.56, 16.43) * mm, "mid": v(18.77, 16.28) * mm, "end": v(19, 16.14) * mm});
            skArc(sketch, "E268", {"start": v(19, 16.14) * mm, "mid": v(19.02, 16.12) * mm, "end": v(19.05, 16.11) * mm});
            skArc(sketch, "E269", {"start": v(19.05, 16.11) * mm, "mid": v(19.08, 16.1) * mm, "end": v(19.1, 16.09) * mm});
            skArc(sketch, "E270", {"start": v(19.1, 16.09) * mm, "mid": v(19.13, 16.08) * mm, "end": v(19.15, 16.07) * mm});
            skArc(sketch, "E271", {"start": v(19.15, 16.07) * mm, "mid": v(19.18, 16.05) * mm, "end": v(19.2, 16.03) * mm});
            skArc(sketch, "E272", {"start": v(19.2, 16.03) * mm, "mid": v(19.22, 16.02) * mm, "end": v(19.24, 16) * mm});
            skArc(sketch, "E273", {"start": v(19.24, 16) * mm, "mid": v(19.32, 15.93) * mm, "end": v(19.4, 15.87) * mm});
            skArc(sketch, "E274", {"start": v(19.4, 15.87) * mm, "mid": v(19.54, 15.77) * mm, "end": v(19.69, 15.68) * mm});
            skArc(sketch, "E275", {"start": v(19.69, 15.68) * mm, "mid": v(19.95, 15.53) * mm, "end": v(20.23, 15.4) * mm});
            skArc(sketch, "E276", {"start": v(20.23, 15.4) * mm, "mid": v(20.38, 15.34) * mm, "end": v(20.53, 15.29) * mm});
            skArc(sketch, "E277", {"start": v(20.53, 15.29) * mm, "mid": v(20.63, 15.27) * mm, "end": v(20.73, 15.27) * mm});
            skArc(sketch, "E278", {"start": v(20.73, 15.27) * mm, "mid": v(20.82, 15.27) * mm, "end": v(20.91, 15.27) * mm});
            skArc(sketch, "E279", {"start": v(20.91, 15.27) * mm, "mid": v(21, 15.28) * mm, "end": v(21.1, 15.27) * mm});
            skArc(sketch, "E280", {"start": v(21.1, 15.27) * mm, "mid": v(21.15, 15.26) * mm, "end": v(21.2, 15.26) * mm});
            skArc(sketch, "E281", {"start": v(21.2, 15.26) * mm, "mid": v(21.27, 15.24) * mm, "end": v(21.33, 15.22) * mm});
            skArc(sketch, "E282", {"start": v(21.33, 15.22) * mm, "mid": v(21.4, 15.2) * mm, "end": v(21.45, 15.17) * mm});
            skArc(sketch, "E283", {"start": v(21.45, 15.17) * mm, "mid": v(21.51, 15.13) * mm, "end": v(21.56, 15.08) * mm});
            skArc(sketch, "E284", {"start": v(21.56, 15.08) * mm, "mid": v(21.58, 15.05) * mm, "end": v(21.6, 15.02) * mm});
            skArc(sketch, "E285", {"start": v(21.6, 15.02) * mm, "mid": v(21.62, 15) * mm, "end": v(21.64, 14.98) * mm});
            skArc(sketch, "E286", {"start": v(21.64, 14.98) * mm, "mid": v(21.68, 14.94) * mm, "end": v(21.71, 14.9) * mm});
            skArc(sketch, "E287", {"start": v(21.71, 14.9) * mm, "mid": v(21.72, 14.88) * mm, "end": v(21.72, 14.87) * mm});
            skArc(sketch, "E288", {"start": v(21.72, 14.87) * mm, "mid": v(21.72, 14.85) * mm, "end": v(21.7, 14.84) * mm});
            skArc(sketch, "E289", {"start": v(21.7, 14.84) * mm, "mid": v(21.64, 14.83) * mm, "end": v(21.57, 14.83) * mm});
            skArc(sketch, "E290", {"start": v(21.57, 14.83) * mm, "mid": v(21.54, 14.83) * mm, "end": v(21.52, 14.84) * mm});
            skArc(sketch, "E291", {"start": v(21.52, 14.84) * mm, "mid": v(21.49, 14.84) * mm, "end": v(21.46, 14.84) * mm});
            skArc(sketch, "E292", {"start": v(21.46, 14.84) * mm, "mid": v(21.44, 14.84) * mm, "end": v(21.41, 14.84) * mm});
            skArc(sketch, "E293", {"start": v(21.41, 14.84) * mm, "mid": v(21.38, 14.83) * mm, "end": v(21.35, 14.82) * mm});
            skArc(sketch, "E294", {"start": v(21.35, 14.82) * mm, "mid": v(21.33, 14.8) * mm, "end": v(21.3, 14.8) * mm});
            skArc(sketch, "E295", {"start": v(21.3, 14.8) * mm, "mid": v(21.3, 14.78) * mm, "end": v(21.29, 14.77) * mm});
            skArc(sketch, "E296", {"start": v(21.29, 14.77) * mm, "mid": v(21.28, 14.75) * mm, "end": v(21.27, 14.74) * mm});
            skArc(sketch, "E297", {"start": v(21.27, 14.74) * mm, "mid": v(21.26, 14.7) * mm, "end": v(21.26, 14.67) * mm});
            skArc(sketch, "E298", {"start": v(21.26, 14.67) * mm, "mid": v(21.24, 14.59) * mm, "end": v(21.25, 14.5) * mm});
            skArc(sketch, "E299", {"start": v(21.25, 14.5) * mm, "mid": v(21.25, 14.47) * mm, "end": v(21.27, 14.45) * mm});
            skArc(sketch, "E300", {"start": v(21.27, 14.45) * mm, "mid": v(21.3, 14.44) * mm, "end": v(21.31, 14.43) * mm});
            skArc(sketch, "E301", {"start": v(21.31, 14.43) * mm, "mid": v(21.33, 14.42) * mm, "end": v(21.35, 14.4) * mm});
            skArc(sketch, "E302", {"start": v(21.35, 14.4) * mm, "mid": v(21.36, 14.4) * mm, "end": v(21.36, 14.38) * mm});
            skArc(sketch, "E303", {"start": v(21.36, 14.38) * mm, "mid": v(21.37, 14.37) * mm, "end": v(21.38, 14.37) * mm});
            skArc(sketch, "E304", {"start": v(21.38, 14.37) * mm, "mid": v(21.39, 14.36) * mm, "end": v(21.4, 14.35) * mm});
            skArc(sketch, "E305", {"start": v(21.4, 14.35) * mm, "mid": v(21.41, 14.34) * mm, "end": v(21.42, 14.33) * mm});
            skArc(sketch, "E306", {"start": v(21.42, 14.33) * mm, "mid": v(21.43, 14.32) * mm, "end": v(21.44, 14.3) * mm});
            skArc(sketch, "E307", {"start": v(21.44, 14.3) * mm, "mid": v(21.45, 14.3) * mm, "end": v(21.46, 14.3) * mm});
            skArc(sketch, "E308", {"start": v(21.46, 14.3) * mm, "mid": v(21.48, 14.29) * mm, "end": v(21.5, 14.29) * mm});
            skArc(sketch, "E309", {"start": v(21.5, 14.29) * mm, "mid": v(21.53, 14.3) * mm, "end": v(21.56, 14.3) * mm});
            skArc(sketch, "E310", {"start": v(21.56, 14.3) * mm, "mid": v(21.6, 14.3) * mm, "end": v(21.65, 14.3) * mm});
            skArc(sketch, "E311", {"start": v(21.65, 14.3) * mm, "mid": v(21.74, 14.29) * mm, "end": v(21.83, 14.29) * mm});
            skArc(sketch, "E312", {"start": v(21.83, 14.29) * mm, "mid": v(21.87, 14.29) * mm, "end": v(21.92, 14.3) * mm});
            skArc(sketch, "E313", {"start": v(21.92, 14.3) * mm, "mid": v(21.98, 14.3) * mm, "end": v(22.03, 14.32) * mm});
            skArc(sketch, "E314", {"start": v(22.03, 14.32) * mm, "mid": v(22.06, 14.34) * mm, "end": v(22.1, 14.37) * mm});
            skArc(sketch, "E315", {"start": v(22.1, 14.37) * mm, "mid": v(22.16, 14.41) * mm, "end": v(22.22, 14.46) * mm});
            skArc(sketch, "E316", {"start": v(22.22, 14.46) * mm, "mid": v(22.25, 14.49) * mm, "end": v(22.28, 14.51) * mm});
            skArc(sketch, "E317", {"start": v(22.28, 14.51) * mm, "mid": v(22.3, 14.53) * mm, "end": v(22.32, 14.56) * mm});
            skArc(sketch, "E318", {"start": v(22.32, 14.56) * mm, "mid": v(22.37, 14.63) * mm, "end": v(22.4, 14.7) * mm});
            skArc(sketch, "E319", {"start": v(22.4, 14.7) * mm, "mid": v(22.43, 14.77) * mm, "end": v(22.43, 14.83) * mm});
            skArc(sketch, "E320", {"start": v(22.43, 14.83) * mm, "mid": v(22.44, 14.9) * mm, "end": v(22.43, 14.96) * mm});
            skArc(sketch, "E321", {"start": v(22.43, 14.96) * mm, "mid": v(22.4, 15.05) * mm, "end": v(22.38, 15.15) * mm});
            skArc(sketch, "E322", {"start": v(22.38, 15.15) * mm, "mid": v(22.34, 15.26) * mm, "end": v(22.3, 15.38) * mm});
            skArc(sketch, "E323", {"start": v(22.3, 15.38) * mm, "mid": v(22.2, 15.53) * mm, "end": v(22.1, 15.66) * mm});
            skArc(sketch, "E324", {"start": v(22.1, 15.66) * mm, "mid": v(22.01, 15.74) * mm, "end": v(21.92, 15.81) * mm});
            skArc(sketch, "E325", {"start": v(21.92, 15.81) * mm, "mid": v(21.75, 15.93) * mm, "end": v(21.57, 16.03) * mm});
            skArc(sketch, "E326", {"start": v(21.57, 16.03) * mm, "mid": v(21.48, 16.08) * mm, "end": v(21.38, 16.11) * mm});
            skArc(sketch, "E327", {"start": v(21.38, 16.11) * mm, "mid": v(21.3, 16.14) * mm, "end": v(21.22, 16.16) * mm});
            skArc(sketch, "E328", {"start": v(21.22, 16.16) * mm, "mid": v(21.15, 16.17) * mm, "end": v(21.08, 16.18) * mm});
            skArc(sketch, "E329", {"start": v(21.08, 16.18) * mm, "mid": v(21.01, 16.19) * mm, "end": v(20.94, 16.2) * mm});
            skArc(sketch, "E330", {"start": v(20.94, 16.2) * mm, "mid": v(20.9, 16.23) * mm, "end": v(20.84, 16.25) * mm});
            skArc(sketch, "E331", {"start": v(20.84, 16.25) * mm, "mid": v(20.77, 16.3) * mm, "end": v(20.7, 16.34) * mm});
            skArc(sketch, "E332", {"start": v(20.7, 16.34) * mm, "mid": v(20.66, 16.37) * mm, "end": v(20.61, 16.4) * mm});
            skArc(sketch, "E333", {"start": v(20.61, 16.4) * mm, "mid": v(20.57, 16.43) * mm, "end": v(20.52, 16.46) * mm});
            skArc(sketch, "E334", {"start": v(20.52, 16.46) * mm, "mid": v(20.43, 16.52) * mm, "end": v(20.33, 16.58) * mm});
            skArc(sketch, "E335", {"start": v(20.33, 16.58) * mm, "mid": v(20.28, 16.6) * mm, "end": v(20.23, 16.64) * mm});
            skArc(sketch, "E336", {"start": v(20.23, 16.64) * mm, "mid": v(20.18, 16.7) * mm, "end": v(20.14, 16.75) * mm});
            skArc(sketch, "E337", {"start": v(20.14, 16.75) * mm, "mid": v(20.08, 16.82) * mm, "end": v(20.03, 16.9) * mm});
            skArc(sketch, "E338", {"start": v(20.03, 16.9) * mm, "mid": v(20, 16.93) * mm, "end": v(19.98, 16.97) * mm});
            skArc(sketch, "E339", {"start": v(19.98, 16.97) * mm, "mid": v(19.98, 16.98) * mm, "end": v(19.97, 17) * mm});
            skArc(sketch, "E340", {"start": v(19.97, 17) * mm, "mid": v(19.97, 17) * mm, "end": v(19.97, 17.01) * mm});
            skArc(sketch, "E341", {"start": v(19.97, 17.01) * mm, "mid": v(19.98, 17.02) * mm, "end": v(19.98, 17.02) * mm});
            skArc(sketch, "E342", {"start": v(19.98, 17.02) * mm, "mid": v(20, 17.02) * mm, "end": v(20, 17.02) * mm});
            skArc(sketch, "E343", {"start": v(20, 17.02) * mm, "mid": v(20.05, 17) * mm, "end": v(20.1, 17) * mm});
            skArc(sketch, "E344", {"start": v(20.1, 17) * mm, "mid": v(20.15, 16.97) * mm, "end": v(20.2, 16.96) * mm});
            skArc(sketch, "E345", {"start": v(20.2, 16.96) * mm, "mid": v(20.31, 16.93) * mm, "end": v(20.42, 16.9) * mm});
            skArc(sketch, "E346", {"start": v(20.42, 16.9) * mm, "mid": v(20.52, 16.86) * mm, "end": v(20.61, 16.83) * mm});
            skArc(sketch, "E347", {"start": v(20.61, 16.83) * mm, "mid": v(20.71, 16.8) * mm, "end": v(20.81, 16.77) * mm});
            skArc(sketch, "E348", {"start": v(20.81, 16.77) * mm, "mid": v(20.92, 16.74) * mm, "end": v(21.03, 16.73) * mm});
            skArc(sketch, "E349", {"start": v(21.03, 16.73) * mm, "mid": v(21.14, 16.73) * mm, "end": v(21.25, 16.74) * mm});
            skArc(sketch, "E350", {"start": v(21.25, 16.74) * mm, "mid": v(21.31, 16.75) * mm, "end": v(21.37, 16.78) * mm});
            skArc(sketch, "E351", {"start": v(21.37, 16.78) * mm, "mid": v(21.4, 16.79) * mm, "end": v(21.4, 16.8) * mm});
            skArc(sketch, "E352", {"start": v(21.4, 16.8) * mm, "mid": v(21.41, 16.82) * mm, "end": v(21.42, 16.83) * mm});
            skArc(sketch, "E353", {"start": v(21.42, 16.83) * mm, "mid": v(21.41, 16.84) * mm, "end": v(21.4, 16.85) * mm});
            skArc(sketch, "E354", {"start": v(21.4, 16.85) * mm, "mid": v(21.39, 16.86) * mm, "end": v(21.37, 16.87) * mm});
            skArc(sketch, "E355", {"start": v(21.37, 16.87) * mm, "mid": v(21.34, 16.88) * mm, "end": v(21.31, 16.88) * mm});
            skArc(sketch, "E356", {"start": v(21.31, 16.88) * mm, "mid": v(21.25, 16.9) * mm, "end": v(21.2, 16.9) * mm});
            skArc(sketch, "E357", {"start": v(21.2, 16.9) * mm, "mid": v(20.98, 16.98) * mm, "end": v(20.78, 17.05) * mm});
            skArc(sketch, "E358", {"start": v(20.78, 17.05) * mm, "mid": v(20.63, 17.11) * mm, "end": v(20.49, 17.18) * mm});
            skArc(sketch, "E359", {"start": v(20.49, 17.18) * mm, "mid": v(20.16, 17.34) * mm, "end": v(19.84, 17.5) * mm});
            skArc(sketch, "E360", {"start": v(19.84, 17.5) * mm, "mid": v(19.79, 17.54) * mm, "end": v(19.73, 17.57) * mm});
            skArc(sketch, "E361", {"start": v(19.73, 17.57) * mm, "mid": v(19.7, 17.6) * mm, "end": v(19.66, 17.66) * mm});
            skArc(sketch, "E362", {"start": v(19.66, 17.66) * mm, "mid": v(19.65, 17.69) * mm, "end": v(19.64, 17.72) * mm});
            skArc(sketch, "E363", {"start": v(19.64, 17.72) * mm, "mid": v(19.64, 17.75) * mm, "end": v(19.63, 17.78) * mm});
            skArc(sketch, "E364", {"start": v(19.63, 17.78) * mm, "mid": v(19.58, 17.9) * mm, "end": v(19.54, 18.02) * mm});
            skArc(sketch, "E365", {"start": v(19.54, 18.02) * mm, "mid": v(19.46, 18.2) * mm, "end": v(19.38, 18.38) * mm});
            skArc(sketch, "E366", {"start": v(19.38, 18.38) * mm, "mid": v(19.3, 18.54) * mm, "end": v(19.21, 18.7) * mm});
            skArc(sketch, "E367", {"start": v(19.21, 18.7) * mm, "mid": v(19.12, 18.84) * mm, "end": v(19.02, 18.98) * mm});
            skArc(sketch, "E368", {"start": v(19.02, 18.98) * mm, "mid": v(18.96, 19.05) * mm, "end": v(18.9, 19.12) * mm});
            skArc(sketch, "E369", {"start": v(18.9, 19.12) * mm, "mid": v(18.8, 19.24) * mm, "end": v(18.7, 19.37) * mm});
            skArc(sketch, "E370", {"start": v(18.7, 19.37) * mm, "mid": v(18.63, 19.47) * mm, "end": v(18.55, 19.56) * mm});
            skArc(sketch, "E371", {"start": v(18.55, 19.56) * mm, "mid": v(18.46, 19.64) * mm, "end": v(18.38, 19.72) * mm});
            skArc(sketch, "E372", {"start": v(18.38, 19.72) * mm, "mid": v(18.31, 19.8) * mm, "end": v(18.25, 19.87) * mm});
            skArc(sketch, "E373", {"start": v(18.25, 19.87) * mm, "mid": v(18.16, 19.97) * mm, "end": v(18.08, 20.09) * mm});
            skArc(sketch, "E374", {"start": v(18.08, 20.09) * mm, "mid": v(18.04, 20.16) * mm, "end": v(18, 20.23) * mm});
            skArc(sketch, "E375", {"start": v(18, 20.23) * mm, "mid": v(17.93, 20.32) * mm, "end": v(17.85, 20.4) * mm});
            skArc(sketch, "E376", {"start": v(17.85, 20.4) * mm, "mid": v(17.7, 20.53) * mm, "end": v(17.51, 20.63) * mm});
            skArc(sketch, "E377", {"start": v(17.51, 20.63) * mm, "mid": v(17.34, 20.68) * mm, "end": v(17.17, 20.7) * mm});
            skArc(sketch, "E378", {"start": v(17.17, 20.7) * mm, "mid": v(17.1, 20.7) * mm, "end": v(17.05, 20.68) * mm});
            skArc(sketch, "E379", {"start": v(17.05, 20.68) * mm, "mid": v(16.93, 20.67) * mm, "end": v(16.82, 20.65) * mm});
            skArc(sketch, "E380", {"start": v(16.82, 20.65) * mm, "mid": v(16.73, 20.65) * mm, "end": v(16.64, 20.65) * mm});
            skArc(sketch, "E381", {"start": v(16.64, 20.65) * mm, "mid": v(16.6, 20.65) * mm, "end": v(16.57, 20.66) * mm});
            skArc(sketch, "E382", {"start": v(16.57, 20.66) * mm, "mid": v(16.53, 20.67) * mm, "end": v(16.49, 20.7) * mm});
            skArc(sketch, "E383", {"start": v(16.49, 20.7) * mm, "mid": v(16.39, 20.75) * mm, "end": v(16.3, 20.8) * mm});
            skArc(sketch, "E384", {"start": v(16.3, 20.8) * mm, "mid": v(16.16, 20.88) * mm, "end": v(16.02, 20.96) * mm});
            skArc(sketch, "E385", {"start": v(16.02, 20.96) * mm, "mid": v(15.92, 21.02) * mm, "end": v(15.82, 21.07) * mm});
            skArc(sketch, "E386", {"start": v(15.82, 21.07) * mm, "mid": v(15.66, 21.14) * mm, "end": v(15.5, 21.2) * mm});
            skArc(sketch, "E387", {"start": v(15.5, 21.2) * mm, "mid": v(15.4, 21.22) * mm, "end": v(15.27, 21.24) * mm});
            skArc(sketch, "E388", {"start": v(15.27, 21.24) * mm, "mid": v(15.2, 21.23) * mm, "end": v(15.14, 21.2) * mm});
            skArc(sketch, "E389", {"start": v(15.14, 21.2) * mm, "mid": v(15.1, 21.17) * mm, "end": v(15.05, 21.12) * mm});
            skArc(sketch, "E390", {"start": v(15.05, 21.12) * mm, "mid": v(15, 21.07) * mm, "end": v(14.96, 21) * mm});
            skArc(sketch, "E391", {"start": v(14.96, 21) * mm, "mid": v(14.9, 20.85) * mm, "end": v(14.86, 20.68) * mm});
            skArc(sketch, "E392", {"start": v(14.86, 20.68) * mm, "mid": v(14.85, 20.6) * mm, "end": v(14.85, 20.52) * mm});
            skArc(sketch, "E393", {"start": v(14.85, 20.52) * mm, "mid": v(14.84, 20.43) * mm, "end": v(14.85, 20.33) * mm});
            skArc(sketch, "E394", {"start": v(14.85, 20.33) * mm, "mid": v(14.85, 20.29) * mm, "end": v(14.85, 20.25) * mm});
            skArc(sketch, "E395", {"start": v(14.85, 20.25) * mm, "mid": v(14.85, 20.23) * mm, "end": v(14.84, 20.22) * mm});
            skArc(sketch, "E396", {"start": v(14.84, 20.22) * mm, "mid": v(14.83, 20.2) * mm, "end": v(14.81, 20.2) * mm});
            skArc(sketch, "E397", {"start": v(14.81, 20.2) * mm, "mid": v(14.78, 20.2) * mm, "end": v(14.75, 20.2) * mm});
            skArc(sketch, "E398", {"start": v(14.75, 20.2) * mm, "mid": v(14.72, 20.2) * mm, "end": v(14.7, 20.22) * mm});
            skArc(sketch, "E399", {"start": v(14.7, 20.22) * mm, "mid": v(14.66, 20.22) * mm, "end": v(14.63, 20.23) * mm});
            skArc(sketch, "E400", {"start": v(14.63, 20.23) * mm, "mid": v(14.57, 20.23) * mm, "end": v(14.5, 20.24) * mm});
            skArc(sketch, "E401", {"start": v(14.5, 20.24) * mm, "mid": v(14.38, 20.25) * mm, "end": v(14.26, 20.26) * mm});
            skArc(sketch, "E402", {"start": v(14.26, 20.26) * mm, "mid": v(13.98, 20.28) * mm, "end": v(13.7, 20.28) * mm});
            skArc(sketch, "E403", {"start": v(13.7, 20.28) * mm, "mid": v(13.54, 20.27) * mm, "end": v(13.37, 20.25) * mm});
            skArc(sketch, "E404", {"start": v(13.37, 20.25) * mm, "mid": v(13.26, 20.23) * mm, "end": v(13.16, 20.2) * mm});
            skArc(sketch, "E405", {"start": v(13.16, 20.2) * mm, "mid": v(13.07, 20.17) * mm, "end": v(12.98, 20.13) * mm});
            skArc(sketch, "E406", {"start": v(12.98, 20.13) * mm, "mid": v(12.9, 20.09) * mm, "end": v(12.83, 20.05) * mm});
            skArc(sketch, "E407", {"start": v(12.83, 20.05) * mm, "mid": v(12.71, 19.98) * mm, "end": v(12.6, 19.9) * mm});
            skArc(sketch, "E408", {"start": v(12.6, 19.9) * mm, "mid": v(12.55, 19.87) * mm, "end": v(12.5, 19.83) * mm});
            skArc(sketch, "E409", {"start": v(12.5, 19.83) * mm, "mid": v(12.44, 19.77) * mm, "end": v(12.38, 19.72) * mm});
            skArc(sketch, "E410.1.0", {"start": v(-20.05, 12.83) * mm, "mid": v(-19.98, 12.71) * mm, "end": v(-19.9, 12.6) * mm});
            skArc(sketch, "E410.1.1", {"start": v(-19.83, 12.5) * mm, "mid": v(-19.77, 12.44) * mm, "end": v(-19.72, 12.38) * mm});
            skArc(sketch, "E410.1.2", {"start": v(-19.41, 12.04) * mm, "mid": v(-19.04, 11.7) * mm, "end": v(-18.64, 11.37) * mm});
            skArc(sketch, "E410.1.3", {"start": v(-20.13, 12.98) * mm, "mid": v(-20.09, 12.9) * mm, "end": v(-20.05, 12.83) * mm});
            skArc(sketch, "E410.1.4", {"start": v(-19.9, 12.6) * mm, "mid": v(-19.87, 12.55) * mm, "end": v(-19.83, 12.5) * mm});
            skArc(sketch, "E410.1.5", {"start": v(-19.56, 18.55) * mm, "mid": v(-19.64, 18.46) * mm, "end": v(-19.72, 18.38) * mm});
            skArc(sketch, "E410.1.6", {"start": v(-19.56, 12.2) * mm, "mid": v(-19.49, 12.12) * mm, "end": v(-19.41, 12.04) * mm});
            skArc(sketch, "E410.1.7", {"start": v(-20.23, 18) * mm, "mid": v(-20.32, 17.93) * mm, "end": v(-20.4, 17.85) * mm});
            skArc(sketch, "E410.1.8", {"start": v(-20.4, 17.85) * mm, "mid": v(-20.53, 17.7) * mm, "end": v(-20.63, 17.51) * mm});
            skArc(sketch, "E410.1.9", {"start": v(-20.68, 17.05) * mm, "mid": v(-20.67, 16.93) * mm, "end": v(-20.65, 16.82) * mm});
            skArc(sketch, "E410.1.10", {"start": v(-20.65, 16.82) * mm, "mid": v(-20.65, 16.73) * mm, "end": v(-20.65, 16.64) * mm});
            skArc(sketch, "E410.1.11", {"start": v(-20.66, 16.57) * mm, "mid": v(-20.67, 16.53) * mm, "end": v(-20.7, 16.49) * mm});
            skArc(sketch, "E410.1.12", {"start": v(-19.37, 18.7) * mm, "mid": v(-19.47, 18.63) * mm, "end": v(-19.56, 18.55) * mm});
            skArc(sketch, "E410.1.13", {"start": v(-19.72, 12.38) * mm, "mid": v(-19.64, 12.3) * mm, "end": v(-19.56, 12.2) * mm});
            skArc(sketch, "E410.1.14", {"start": v(-19.87, 18.25) * mm, "mid": v(-19.97, 18.16) * mm, "end": v(-20.09, 18.08) * mm});
            skArc(sketch, "E410.1.15", {"start": v(-20.09, 18.08) * mm, "mid": v(-20.16, 18.04) * mm, "end": v(-20.23, 18) * mm});
            skArc(sketch, "E410.1.16", {"start": v(-20.7, 17.17) * mm, "mid": v(-20.7, 17.1) * mm, "end": v(-20.68, 17.05) * mm});
            skArc(sketch, "E410.1.17", {"start": v(-20.65, 16.64) * mm, "mid": v(-20.65, 16.6) * mm, "end": v(-20.66, 16.57) * mm});
            skArc(sketch, "E410.1.18", {"start": v(-19.72, 18.38) * mm, "mid": v(-19.8, 18.31) * mm, "end": v(-19.87, 18.25) * mm});
            skArc(sketch, "E410.1.19", {"start": v(-20.63, 17.51) * mm, "mid": v(-20.68, 17.34) * mm, "end": v(-20.7, 17.17) * mm});
            skArc(sketch, "E410.1.20", {"start": v(-18.64, 11.37) * mm, "mid": v(-18.5, 11.27) * mm, "end": v(-18.35, 11.18) * mm});
            skArc(sketch, "E410.1.21", {"start": v(-20.25, 13.37) * mm, "mid": v(-20.23, 13.26) * mm, "end": v(-20.2, 13.16) * mm});
            skArc(sketch, "E410.1.22", {"start": v(-20.2, 13.16) * mm, "mid": v(-20.17, 13.07) * mm, "end": v(-20.13, 12.98) * mm});
            skArc(sketch, "E410.1.23", {"start": v(-13.89, 11.47) * mm, "mid": v(-13.52, 11.59) * mm, "end": v(-13.15, 11.69) * mm});
            skArc(sketch, "E410.1.24", {"start": v(-18.7, 19.21) * mm, "mid": v(-18.84, 19.12) * mm, "end": v(-18.98, 19.02) * mm});
            skArc(sketch, "E410.1.25", {"start": v(-19.12, 18.9) * mm, "mid": v(-19.24, 18.8) * mm, "end": v(-19.37, 18.7) * mm});
            skArc(sketch, "E410.1.26", {"start": v(-20.28, 13.7) * mm, "mid": v(-20.27, 13.54) * mm, "end": v(-20.25, 13.37) * mm});
            skArc(sketch, "E410.1.27", {"start": v(-14.18, 11.4) * mm, "mid": v(-14.03, 11.42) * mm, "end": v(-13.89, 11.47) * mm});
            skArc(sketch, "E410.1.28", {"start": v(-12.96, 11.74) * mm, "mid": v(-12.86, 11.77) * mm, "end": v(-12.77, 11.8) * mm});
            skArc(sketch, "E410.1.29", {"start": v(-18.38, 19.38) * mm, "mid": v(-18.54, 19.3) * mm, "end": v(-18.7, 19.21) * mm});
            skArc(sketch, "E410.1.30", {"start": v(-18.98, 19.02) * mm, "mid": v(-19.05, 18.96) * mm, "end": v(-19.12, 18.9) * mm});
            skArc(sketch, "E410.1.31", {"start": v(-15.37, 11.4) * mm, "mid": v(-15.13, 11.38) * mm, "end": v(-14.9, 11.38) * mm});
            skArc(sketch, "E410.1.32", {"start": v(-14.9, 11.38) * mm, "mid": v(-14.82, 11.38) * mm, "end": v(-14.75, 11.37) * mm});
            skArc(sketch, "E410.1.33", {"start": v(-14.75, 11.37) * mm, "mid": v(-14.62, 11.36) * mm, "end": v(-14.5, 11.37) * mm});
            skArc(sketch, "E410.1.34", {"start": v(-14.5, 11.37) * mm, "mid": v(-14.34, 11.38) * mm, "end": v(-14.18, 11.4) * mm});
            skArc(sketch, "E410.1.35", {"start": v(-13.15, 11.69) * mm, "mid": v(-13.05, 11.71) * mm, "end": v(-12.96, 11.74) * mm});
            skArc(sketch, "E410.1.36", {"start": v(-12.66, 11.85) * mm, "mid": v(-12.6, 11.88) * mm, "end": v(-12.55, 11.92) * mm});
            skArc(sketch, "E410.1.37", {"start": v(-12.36, 12.03) * mm, "mid": v(-12.3, 12.06) * mm, "end": v(-12.24, 12.1) * mm});
            skArc(sketch, "E410.1.38", {"start": v(-12.24, 12.1) * mm, "mid": v(-12, 12.3) * mm, "end": v(-11.75, 12.49) * mm});
            skArc(sketch, "E410.1.39", {"start": v(-12.77, 11.8) * mm, "mid": v(-12.72, 11.83) * mm, "end": v(-12.66, 11.85) * mm});
            skArc(sketch, "E410.1.40", {"start": v(-12.55, 11.92) * mm, "mid": v(-12.45, 11.97) * mm, "end": v(-12.36, 12.03) * mm});
            skArc(sketch, "E410.1.41", {"start": v(-16.66, 11.62) * mm, "mid": v(-16.4, 11.55) * mm, "end": v(-16.15, 11.48) * mm});
            skArc(sketch, "E410.1.42", {"start": v(-16.15, 11.48) * mm, "mid": v(-15.87, 11.43) * mm, "end": v(-15.59, 11.4) * mm});
            skArc(sketch, "E410.1.43", {"start": v(-15.59, 11.4) * mm, "mid": v(-15.48, 11.4) * mm, "end": v(-15.37, 11.4) * mm});
            skArc(sketch, "E410.1.44", {"start": v(-17.9, 11.02) * mm, "mid": v(-17.87, 11.03) * mm, "end": v(-17.84, 11.04) * mm});
            skArc(sketch, "E410.1.45", {"start": v(-17.84, 11.04) * mm, "mid": v(-17.77, 11.07) * mm, "end": v(-17.71, 11.1) * mm});
            skArc(sketch, "E410.1.46", {"start": v(-17.44, 11.34) * mm, "mid": v(-17.4, 11.4) * mm, "end": v(-17.34, 11.45) * mm});
            skArc(sketch, "E410.1.47", {"start": v(-17.22, 11.6) * mm, "mid": v(-17.18, 11.66) * mm, "end": v(-17.14, 11.73) * mm});
            skArc(sketch, "E410.1.48", {"start": v(-21, 14.96) * mm, "mid": v(-20.85, 14.9) * mm, "end": v(-20.68, 14.86) * mm});
            skArc(sketch, "E410.1.49", {"start": v(-20.52, 14.85) * mm, "mid": v(-20.43, 14.84) * mm, "end": v(-20.33, 14.85) * mm});
            skArc(sketch, "E410.1.50", {"start": v(-16.68, 11.62) * mm, "mid": v(-16.67, 11.62) * mm, "end": v(-16.66, 11.62) * mm});
            skArc(sketch, "E410.1.51", {"start": v(-20.8, 16.3) * mm, "mid": v(-20.88, 16.16) * mm, "end": v(-20.96, 16.02) * mm});
            skArc(sketch, "E410.1.52", {"start": v(-20.24, 14.5) * mm, "mid": v(-20.25, 14.38) * mm, "end": v(-20.26, 14.26) * mm});
            skArc(sketch, "E410.1.53", {"start": v(-20.96, 16.02) * mm, "mid": v(-21.02, 15.92) * mm, "end": v(-21.07, 15.82) * mm});
            skArc(sketch, "E410.1.54", {"start": v(-20.26, 14.26) * mm, "mid": v(-20.28, 13.98) * mm, "end": v(-20.28, 13.7) * mm});
            skArc(sketch, "E410.1.55", {"start": v(-21.2, 15.5) * mm, "mid": v(-21.22, 15.4) * mm, "end": v(-21.24, 15.27) * mm});
            skArc(sketch, "E410.1.56", {"start": v(-17.97, 11.03) * mm, "mid": v(-17.93, 11.02) * mm, "end": v(-17.9, 11.02) * mm});
            skArc(sketch, "E410.1.57", {"start": v(-17.71, 11.1) * mm, "mid": v(-17.57, 11.22) * mm, "end": v(-17.44, 11.34) * mm});
            skArc(sketch, "E410.1.58", {"start": v(-17.34, 11.45) * mm, "mid": v(-17.28, 11.53) * mm, "end": v(-17.22, 11.6) * mm});
            skArc(sketch, "E410.1.59", {"start": v(-21.24, 15.27) * mm, "mid": v(-21.23, 15.2) * mm, "end": v(-21.2, 15.14) * mm});
            skArc(sketch, "E410.1.60", {"start": v(-21.2, 15.14) * mm, "mid": v(-21.17, 15.1) * mm, "end": v(-21.12, 15.05) * mm});
            skArc(sketch, "E410.1.61", {"start": v(-21.12, 15.05) * mm, "mid": v(-21.07, 15) * mm, "end": v(-21, 14.96) * mm});
            skArc(sketch, "E410.1.62", {"start": v(-16.98, 17.97) * mm, "mid": v(-16.93, 18.05) * mm, "end": v(-16.87, 18.1) * mm});
            skArc(sketch, "E410.1.63", {"start": v(-15.93, 17.37) * mm, "mid": v(-16.26, 17.24) * mm, "end": v(-16.59, 17.12) * mm});
            skArc(sketch, "E410.1.64", {"start": v(-20.68, 14.86) * mm, "mid": v(-20.6, 14.85) * mm, "end": v(-20.52, 14.85) * mm});
            skArc(sketch, "E410.1.65", {"start": v(-16.87, 18.1) * mm, "mid": v(-16.85, 18.13) * mm, "end": v(-16.83, 18.14) * mm});
            skArc(sketch, "E410.1.66", {"start": v(-16.59, 17.12) * mm, "mid": v(-16.72, 17.06) * mm, "end": v(-16.86, 17) * mm});
            skArc(sketch, "E410.1.67", {"start": v(-16.86, 17) * mm, "mid": v(-16.97, 16.95) * mm, "end": v(-17.08, 16.9) * mm});
            skArc(sketch, "E410.1.68", {"start": v(-16.64, 18.3) * mm, "mid": v(-16.53, 18.43) * mm, "end": v(-16.43, 18.56) * mm});
            skArc(sketch, "E410.1.69", {"start": v(-16.75, 11.65) * mm, "mid": v(-16.72, 11.64) * mm, "end": v(-16.68, 11.62) * mm});
            skArc(sketch, "E410.1.70", {"start": v(-17.17, 17) * mm, "mid": v(-17.19, 17.09) * mm, "end": v(-17.21, 17.18) * mm});
            skArc(sketch, "E410.1.71", {"start": v(-20.7, 16.49) * mm, "mid": v(-20.75, 16.39) * mm, "end": v(-20.8, 16.3) * mm});
            skArc(sketch, "E410.1.72", {"start": v(-17.21, 17.18) * mm, "mid": v(-17.24, 17.28) * mm, "end": v(-17.26, 17.37) * mm});
            skArc(sketch, "E410.1.73", {"start": v(-20.23, 14.63) * mm, "mid": v(-20.23, 14.57) * mm, "end": v(-20.24, 14.5) * mm});
            skArc(sketch, "E410.1.74", {"start": v(-17.27, 17.48) * mm, "mid": v(-17.27, 17.53) * mm, "end": v(-17.27, 17.58) * mm});
            skArc(sketch, "E410.1.75", {"start": v(-21.07, 15.82) * mm, "mid": v(-21.14, 15.66) * mm, "end": v(-21.2, 15.5) * mm});
            skArc(sketch, "E410.1.76", {"start": v(-17.08, 11.75) * mm, "mid": v(-17.04, 11.73) * mm, "end": v(-16.99, 11.72) * mm});
            skArc(sketch, "E410.1.77", {"start": v(-18.09, 11.06) * mm, "mid": v(-18.03, 11.04) * mm, "end": v(-17.97, 11.03) * mm});
            skArc(sketch, "E410.1.78", {"start": v(-15, 17.63) * mm, "mid": v(-15.33, 17.56) * mm, "end": v(-15.66, 17.46) * mm});
            skArc(sketch, "E410.1.79", {"start": v(-17.17, 17.74) * mm, "mid": v(-17.12, 17.79) * mm, "end": v(-17.08, 17.83) * mm});
            skArc(sketch, "E410.1.80", {"start": v(-15.66, 17.46) * mm, "mid": v(-15.8, 17.42) * mm, "end": v(-15.93, 17.37) * mm});
            skArc(sketch, "E410.1.81", {"start": v(-10.68, 12.95) * mm, "mid": v(-10.51, 13) * mm, "end": v(-10.34, 13.06) * mm});
            skArc(sketch, "E410.1.82", {"start": v(-10.34, 13.06) * mm, "mid": v(-10.17, 13.12) * mm, "end": v(-10, 13.19) * mm});
            skArc(sketch, "E410.1.83", {"start": v(-16.83, 18.14) * mm, "mid": v(-16.73, 18.22) * mm, "end": v(-16.64, 18.3) * mm});
            skArc(sketch, "E410.1.84", {"start": v(-9.12, 14.28) * mm, "mid": v(-9.17, 14.36) * mm, "end": v(-9.22, 14.45) * mm});
            skArc(sketch, "E410.1.85", {"start": v(-9.8, 13.31) * mm, "mid": v(-9.67, 13.41) * mm, "end": v(-9.53, 13.5) * mm});
            skArc(sketch, "E410.1.86", {"start": v(-9.22, 14.45) * mm, "mid": v(-9.26, 14.5) * mm, "end": v(-9.3, 14.56) * mm});
            skArc(sketch, "E410.1.87", {"start": v(-17.15, 16.9) * mm, "mid": v(-17.16, 16.95) * mm, "end": v(-17.17, 17) * mm});
            skArc(sketch, "E410.1.88", {"start": v(-16.79, 11.66) * mm, "mid": v(-16.77, 11.66) * mm, "end": v(-16.75, 11.65) * mm});
            skArc(sketch, "E410.1.89", {"start": v(-9.3, 13.6) * mm, "mid": v(-9.26, 13.63) * mm, "end": v(-9.21, 13.66) * mm});
            skArc(sketch, "E410.1.90", {"start": v(-20.22, 14.7) * mm, "mid": v(-20.22, 14.66) * mm, "end": v(-20.23, 14.63) * mm});
            skArc(sketch, "E410.1.91", {"start": v(-17.26, 17.37) * mm, "mid": v(-17.27, 17.43) * mm, "end": v(-17.27, 17.48) * mm});
            skArc(sketch, "E410.1.92", {"start": v(-11.41, 12.75) * mm, "mid": v(-11.33, 12.78) * mm, "end": v(-11.26, 12.8) * mm});
            skArc(sketch, "E410.1.93", {"start": v(-8.98, 13.81) * mm, "mid": v(-8.97, 13.84) * mm, "end": v(-8.96, 13.88) * mm});
            skArc(sketch, "E410.1.94", {"start": v(-17.12, 11.75) * mm, "mid": v(-17.1, 11.75) * mm, "end": v(-17.08, 11.75) * mm});
            skArc(sketch, "E410.1.95", {"start": v(-14.83, 17.66) * mm, "mid": v(-14.91, 17.64) * mm, "end": v(-15, 17.63) * mm});
            skArc(sketch, "E410.1.96", {"start": v(-18.35, 11.18) * mm, "mid": v(-18.22, 11.11) * mm, "end": v(-18.09, 11.06) * mm});
            skArc(sketch, "E410.1.97", {"start": v(-17.22, 17.7) * mm, "mid": v(-17.2, 17.72) * mm, "end": v(-17.17, 17.74) * mm});
            skArc(sketch, "E410.1.98", {"start": v(-11.03, 12.87) * mm, "mid": v(-10.92, 12.9) * mm, "end": v(-10.8, 12.92) * mm});
            skArc(sketch, "E410.1.99", {"start": v(-9.69, 14.85) * mm, "mid": v(-9.74, 14.8) * mm, "end": v(-9.79, 14.75) * mm});
            skArc(sketch, "E410.1.100", {"start": v(-8.95, 13.92) * mm, "mid": v(-8.95, 13.94) * mm, "end": v(-8.95, 13.96) * mm});
            skArc(sketch, "E410.1.101", {"start": v(-10.8, 12.92) * mm, "mid": v(-10.74, 12.93) * mm, "end": v(-10.68, 12.95) * mm});
            skArc(sketch, "E410.1.102", {"start": v(-9.06, 14.2) * mm, "mid": v(-9.1, 14.24) * mm, "end": v(-9.12, 14.28) * mm});
            skArc(sketch, "E410.1.103", {"start": v(-9.87, 13.26) * mm, "mid": v(-9.84, 13.28) * mm, "end": v(-9.8, 13.31) * mm});
            skArc(sketch, "E410.1.104", {"start": v(-9.91, 14.41) * mm, "mid": v(-9.93, 14.37) * mm, "end": v(-9.95, 14.32) * mm});
            skArc(sketch, "E410.1.105", {"start": v(-17.14, 16.9) * mm, "mid": v(-17.15, 16.9) * mm, "end": v(-17.15, 16.9) * mm});
            skArc(sketch, "E410.1.106", {"start": v(-16.87, 11.68) * mm, "mid": v(-16.83, 11.67) * mm, "end": v(-16.79, 11.66) * mm});
            skArc(sketch, "E410.1.107", {"start": v(-9.41, 13.55) * mm, "mid": v(-9.36, 13.58) * mm, "end": v(-9.3, 13.6) * mm});
            skArc(sketch, "E410.1.108", {"start": v(-20.2, 14.75) * mm, "mid": v(-20.2, 14.72) * mm, "end": v(-20.22, 14.7) * mm});
            skArc(sketch, "E410.1.109", {"start": v(-11.45, 12.74) * mm, "mid": v(-11.43, 12.75) * mm, "end": v(-11.41, 12.75) * mm});
            skArc(sketch, "E410.1.110", {"start": v(-14.54, 17.74) * mm, "mid": v(-14.68, 17.7) * mm, "end": v(-14.83, 17.66) * mm});
            skArc(sketch, "E410.1.111", {"start": v(-17.25, 17.65) * mm, "mid": v(-17.24, 17.67) * mm, "end": v(-17.22, 17.7) * mm});
            skArc(sketch, "E410.1.112", {"start": v(-11.26, 12.8) * mm, "mid": v(-11.15, 12.84) * mm, "end": v(-11.03, 12.87) * mm});
            skArc(sketch, "E410.1.113", {"start": v(-17.14, 11.73) * mm, "mid": v(-17.13, 11.74) * mm, "end": v(-17.12, 11.75) * mm});
            skArc(sketch, "E410.1.114", {"start": v(-9.66, 14.86) * mm, "mid": v(-9.67, 14.86) * mm, "end": v(-9.69, 14.85) * mm});
            skArc(sketch, "E410.1.115", {"start": v(-8.96, 13.88) * mm, "mid": v(-8.96, 13.9) * mm, "end": v(-8.95, 13.92) * mm});
            skArc(sketch, "E410.1.116", {"start": v(-9, 14.12) * mm, "mid": v(-9.02, 14.16) * mm, "end": v(-9.06, 14.2) * mm});
            skArc(sketch, "E410.1.117", {"start": v(-10, 13.19) * mm, "mid": v(-9.93, 13.22) * mm, "end": v(-9.87, 13.26) * mm});
            skArc(sketch, "E410.1.118", {"start": v(-17.11, 16.88) * mm, "mid": v(-17.13, 16.88) * mm, "end": v(-17.14, 16.9) * mm});
            skArc(sketch, "E410.1.119", {"start": v(-16.93, 11.7) * mm, "mid": v(-16.9, 11.7) * mm, "end": v(-16.87, 11.68) * mm});
            skArc(sketch, "E410.1.120", {"start": v(-9.53, 13.5) * mm, "mid": v(-9.47, 13.53) * mm, "end": v(-9.41, 13.55) * mm});
            skArc(sketch, "E410.1.121", {"start": v(-20.2, 14.81) * mm, "mid": v(-20.2, 14.78) * mm, "end": v(-20.2, 14.75) * mm});
            skArc(sketch, "E410.1.122", {"start": v(-10.23, 14.02) * mm, "mid": v(-10.26, 14) * mm, "end": v(-10.28, 13.98) * mm});
            skArc(sketch, "E410.1.123", {"start": v(-11.51, 12.7) * mm, "mid": v(-11.48, 12.72) * mm, "end": v(-11.45, 12.74) * mm});
            skArc(sketch, "E410.1.124", {"start": v(-10.36, 13.95) * mm, "mid": v(-10.4, 13.94) * mm, "end": v(-10.45, 13.92) * mm});
            skArc(sketch, "E410.1.125", {"start": v(-9.04, 13.74) * mm, "mid": v(-9.01, 13.77) * mm, "end": v(-8.98, 13.81) * mm});
            skArc(sketch, "E410.1.126", {"start": v(-14.25, 17.82) * mm, "mid": v(-14.4, 17.78) * mm, "end": v(-14.54, 17.74) * mm});
            skArc(sketch, "E410.1.127", {"start": v(-17.27, 17.58) * mm, "mid": v(-17.26, 17.62) * mm, "end": v(-17.25, 17.65) * mm});
            skArc(sketch, "E410.1.128", {"start": v(-10.74, 13.84) * mm, "mid": v(-10.96, 13.82) * mm, "end": v(-11.19, 13.84) * mm});
            skArc(sketch, "E410.1.129", {"start": v(-9.64, 14.85) * mm, "mid": v(-9.65, 14.86) * mm, "end": v(-9.66, 14.86) * mm});
            skArc(sketch, "E410.1.130", {"start": v(-17.08, 17.83) * mm, "mid": v(-17.02, 17.9) * mm, "end": v(-16.98, 17.97) * mm});
            skArc(sketch, "E410.1.131", {"start": v(-8.96, 14.08) * mm, "mid": v(-8.97, 14.1) * mm, "end": v(-9, 14.12) * mm});
            skArc(sketch, "E410.1.132", {"start": v(-10.71, 15.4) * mm, "mid": v(-10.66, 15.45) * mm, "end": v(-10.6, 15.49) * mm});
            skArc(sketch, "E410.1.133", {"start": v(-9.87, 14.53) * mm, "mid": v(-9.9, 14.47) * mm, "end": v(-9.91, 14.41) * mm});
            skArc(sketch, "E410.1.134", {"start": v(-16.99, 11.72) * mm, "mid": v(-16.96, 11.7) * mm, "end": v(-16.93, 11.7) * mm});
            skArc(sketch, "E410.1.135", {"start": v(-12.03, 13.9) * mm, "mid": v(-12.12, 13.93) * mm, "end": v(-12.2, 13.97) * mm});
            skArc(sketch, "E410.1.136", {"start": v(-17.08, 16.9) * mm, "mid": v(-17.1, 16.89) * mm, "end": v(-17.11, 16.88) * mm});
            skArc(sketch, "E410.1.137", {"start": v(-20.22, 14.84) * mm, "mid": v(-20.2, 14.83) * mm, "end": v(-20.2, 14.81) * mm});
            skArc(sketch, "E410.1.138", {"start": v(-12, 14.84) * mm, "mid": v(-11.82, 14.88) * mm, "end": v(-11.65, 14.92) * mm});
            skArc(sketch, "E410.1.139", {"start": v(-12.3, 14.06) * mm, "mid": v(-12.35, 14.1) * mm, "end": v(-12.4, 14.14) * mm});
            skArc(sketch, "E410.1.140", {"start": v(-11.65, 14.92) * mm, "mid": v(-11.57, 14.94) * mm, "end": v(-11.5, 14.97) * mm});
            skArc(sketch, "E410.1.141", {"start": v(-10.1, 14.13) * mm, "mid": v(-10.16, 14.07) * mm, "end": v(-10.23, 14.02) * mm});
            skArc(sketch, "E410.1.142", {"start": v(-12.7, 14.4) * mm, "mid": v(-12.74, 14.43) * mm, "end": v(-12.77, 14.46) * mm});
            skArc(sketch, "E410.1.143", {"start": v(-11.75, 12.49) * mm, "mid": v(-11.63, 12.6) * mm, "end": v(-11.51, 12.7) * mm});
            skArc(sketch, "E410.1.144", {"start": v(-10.32, 13.97) * mm, "mid": v(-10.34, 13.96) * mm, "end": v(-10.36, 13.95) * mm});
            skArc(sketch, "E410.1.145", {"start": v(-9.1, 13.7) * mm, "mid": v(-9.07, 13.72) * mm, "end": v(-9.04, 13.74) * mm});
            skArc(sketch, "E410.1.146", {"start": v(-13.52, 15.99) * mm, "mid": v(-13.34, 16.13) * mm, "end": v(-13.15, 16.28) * mm});
            skArc(sketch, "E410.1.147", {"start": v(-12.1, 15.62) * mm, "mid": v(-12.15, 15.61) * mm, "end": v(-12.2, 15.6) * mm});
            skArc(sketch, "E410.1.148", {"start": v(-10.45, 13.92) * mm, "mid": v(-10.6, 13.87) * mm, "end": v(-10.74, 13.84) * mm});
            skArc(sketch, "E410.1.149", {"start": v(-9.62, 14.83) * mm, "mid": v(-9.63, 14.84) * mm, "end": v(-9.64, 14.85) * mm});
            skArc(sketch, "E410.1.150", {"start": v(-12.2, 15.6) * mm, "mid": v(-12.35, 15.6) * mm, "end": v(-12.5, 15.62) * mm});
            skArc(sketch, "E410.1.151", {"start": v(-11.3, 15.07) * mm, "mid": v(-11.27, 15.09) * mm, "end": v(-11.25, 15.1) * mm});
            skArc(sketch, "E410.1.152", {"start": v(-11.19, 13.84) * mm, "mid": v(-11.3, 13.87) * mm, "end": v(-11.4, 13.9) * mm});
            skArc(sketch, "E410.1.153", {"start": v(-12.69, 14.64) * mm, "mid": v(-12.66, 14.65) * mm, "end": v(-12.64, 14.67) * mm});
            skArc(sketch, "E410.1.154", {"start": v(-11.4, 13.9) * mm, "mid": v(-11.46, 13.91) * mm, "end": v(-11.52, 13.93) * mm});
            skArc(sketch, "E410.1.155", {"start": v(-11.02, 15.22) * mm, "mid": v(-10.96, 15.25) * mm, "end": v(-10.91, 15.27) * mm});
            skArc(sketch, "E410.1.156", {"start": v(-8.94, 14.02) * mm, "mid": v(-8.95, 14.05) * mm, "end": v(-8.96, 14.08) * mm});
            skArc(sketch, "E410.1.157", {"start": v(-10.84, 15.32) * mm, "mid": v(-10.78, 15.37) * mm, "end": v(-10.71, 15.4) * mm});
            skArc(sketch, "E410.1.158", {"start": v(-11.78, 13.92) * mm, "mid": v(-11.86, 13.91) * mm, "end": v(-11.94, 13.9) * mm});
            skArc(sketch, "E410.1.159", {"start": v(-9.84, 14.6) * mm, "mid": v(-9.85, 14.56) * mm, "end": v(-9.87, 14.53) * mm});
            skArc(sketch, "E410.1.160", {"start": v(-13.38, 15.81) * mm, "mid": v(-13.46, 15.8) * mm, "end": v(-13.53, 15.79) * mm});
            skArc(sketch, "E410.1.161", {"start": v(-11.94, 13.9) * mm, "mid": v(-11.98, 13.9) * mm, "end": v(-12.03, 13.9) * mm});
            skArc(sketch, "E410.1.162", {"start": v(-12.28, 14.8) * mm, "mid": v(-12.14, 14.82) * mm, "end": v(-12, 14.84) * mm});
            skArc(sketch, "E410.1.163", {"start": v(-12.2, 13.97) * mm, "mid": v(-12.25, 14.01) * mm, "end": v(-12.3, 14.06) * mm});
            skArc(sketch, "E410.1.164", {"start": v(-20.25, 14.85) * mm, "mid": v(-20.23, 14.85) * mm, "end": v(-20.22, 14.84) * mm});
            skArc(sketch, "E410.1.165", {"start": v(-10.02, 14.21) * mm, "mid": v(-10.05, 14.17) * mm, "end": v(-10.1, 14.13) * mm});
            skArc(sketch, "E410.1.166", {"start": v(-10.52, 15.82) * mm, "mid": v(-10.59, 15.95) * mm, "end": v(-10.67, 16.08) * mm});
            skArc(sketch, "E410.1.167", {"start": v(-12.44, 14.18) * mm, "mid": v(-12.58, 14.3) * mm, "end": v(-12.7, 14.4) * mm});
            skArc(sketch, "E410.1.168", {"start": v(-13.53, 18.06) * mm, "mid": v(-13.61, 18.01) * mm, "end": v(-13.7, 17.98) * mm});
            skArc(sketch, "E410.1.169", {"start": v(-10.78, 16.23) * mm, "mid": v(-10.85, 16.32) * mm, "end": v(-10.93, 16.4) * mm});
            skArc(sketch, "E410.1.170", {"start": v(-10.28, 13.98) * mm, "mid": v(-10.3, 13.98) * mm, "end": v(-10.32, 13.97) * mm});
            skArc(sketch, "E410.1.171", {"start": v(-11.71, 15.8) * mm, "mid": v(-11.85, 15.72) * mm, "end": v(-12, 15.66) * mm});
            skArc(sketch, "E410.1.172", {"start": v(-13.7, 17.98) * mm, "mid": v(-13.78, 17.94) * mm, "end": v(-13.88, 17.92) * mm});
            skArc(sketch, "E410.1.173", {"start": v(-9.15, 13.68) * mm, "mid": v(-9.12, 13.7) * mm, "end": v(-9.1, 13.7) * mm});
            skArc(sketch, "E410.1.174", {"start": v(-10.93, 16.4) * mm, "mid": v(-11, 16.47) * mm, "end": v(-11.08, 16.53) * mm});
            skArc(sketch, "E410.1.175", {"start": v(-13.6, 15.92) * mm, "mid": v(-13.56, 15.95) * mm, "end": v(-13.52, 15.99) * mm});
            skArc(sketch, "E410.1.176", {"start": v(-12, 15.66) * mm, "mid": v(-12.05, 15.64) * mm, "end": v(-12.1, 15.62) * mm});
            skArc(sketch, "E410.1.177", {"start": v(-13.88, 17.92) * mm, "mid": v(-13.97, 17.9) * mm, "end": v(-14.06, 17.87) * mm});
            skArc(sketch, "E410.1.178", {"start": v(-9.6, 14.81) * mm, "mid": v(-9.6, 14.82) * mm, "end": v(-9.62, 14.83) * mm});
            skArc(sketch, "E410.1.179", {"start": v(-11.34, 15.05) * mm, "mid": v(-11.32, 15.06) * mm, "end": v(-11.3, 15.07) * mm});
            skArc(sketch, "E410.1.180", {"start": v(-14.06, 17.87) * mm, "mid": v(-14.16, 17.85) * mm, "end": v(-14.25, 17.82) * mm});
            skArc(sketch, "E410.1.181", {"start": v(-13.15, 16.28) * mm, "mid": v(-12.99, 16.4) * mm, "end": v(-12.82, 16.53) * mm});
            skArc(sketch, "E410.1.182", {"start": v(-12.82, 16.53) * mm, "mid": v(-12.73, 16.59) * mm, "end": v(-12.64, 16.64) * mm});
            skArc(sketch, "E410.1.183", {"start": v(-12.73, 14.6) * mm, "mid": v(-12.7, 14.62) * mm, "end": v(-12.69, 14.64) * mm});
            skArc(sketch, "E410.1.184", {"start": v(-12.78, 15.69) * mm, "mid": v(-12.89, 15.73) * mm, "end": v(-13, 15.77) * mm});
            skArc(sketch, "E410.1.185", {"start": v(-11.21, 15.13) * mm, "mid": v(-11.12, 15.18) * mm, "end": v(-11.02, 15.22) * mm});
            skArc(sketch, "E410.1.186", {"start": v(-13, 15.77) * mm, "mid": v(-13.05, 15.79) * mm, "end": v(-13.1, 15.8) * mm});
            skArc(sketch, "E410.1.187", {"start": v(-11.25, 16.53) * mm, "mid": v(-11.3, 16.46) * mm, "end": v(-11.34, 16.39) * mm});
            skArc(sketch, "E410.1.188", {"start": v(-8.95, 13.96) * mm, "mid": v(-8.94, 13.99) * mm, "end": v(-8.94, 14.02) * mm});
            skArc(sketch, "E410.1.189", {"start": v(-11.66, 13.93) * mm, "mid": v(-11.72, 13.93) * mm, "end": v(-11.78, 13.92) * mm});
            skArc(sketch, "E410.1.190", {"start": v(-9.83, 14.65) * mm, "mid": v(-9.83, 14.62) * mm, "end": v(-9.84, 14.6) * mm});
            skArc(sketch, "E410.1.191", {"start": v(-12.16, 16.93) * mm, "mid": v(-12.08, 16.99) * mm, "end": v(-12, 17.05) * mm});
            skArc(sketch, "E410.1.192", {"start": v(-13.2, 15.82) * mm, "mid": v(-13.29, 15.82) * mm, "end": v(-13.38, 15.81) * mm});
            skArc(sketch, "E410.1.193", {"start": v(-12.39, 14.78) * mm, "mid": v(-12.33, 14.79) * mm, "end": v(-12.28, 14.8) * mm});
            skArc(sketch, "E410.1.194", {"start": v(-11.77, 17.19) * mm, "mid": v(-11.72, 17.2) * mm, "end": v(-11.66, 17.22) * mm});
            skArc(sketch, "E410.1.195", {"start": v(-20.33, 14.85) * mm, "mid": v(-20.29, 14.85) * mm, "end": v(-20.25, 14.85) * mm});
            skArc(sketch, "E410.1.196", {"start": v(-9.95, 14.32) * mm, "mid": v(-9.98, 14.26) * mm, "end": v(-10.02, 14.21) * mm});
            skArc(sketch, "E410.1.197", {"start": v(-11.47, 16.04) * mm, "mid": v(-11.49, 16.01) * mm, "end": v(-11.5, 15.99) * mm});
            skArc(sketch, "E410.1.198", {"start": v(-10.48, 15.72) * mm, "mid": v(-10.5, 15.77) * mm, "end": v(-10.52, 15.82) * mm});
            skArc(sketch, "E410.1.199", {"start": v(-13.3, 18.22) * mm, "mid": v(-13.41, 18.14) * mm, "end": v(-13.53, 18.06) * mm});
            skArc(sketch, "E410.1.200", {"start": v(-12.4, 14.14) * mm, "mid": v(-12.42, 14.16) * mm, "end": v(-12.44, 14.18) * mm});
            skArc(sketch, "E410.1.201", {"start": v(-10.67, 16.08) * mm, "mid": v(-10.72, 16.15) * mm, "end": v(-10.78, 16.23) * mm});
            skArc(sketch, "E410.1.202", {"start": v(-11.62, 15.87) * mm, "mid": v(-11.67, 15.83) * mm, "end": v(-11.71, 15.8) * mm});
            skArc(sketch, "E410.1.203", {"start": v(-9.21, 13.66) * mm, "mid": v(-9.18, 13.67) * mm, "end": v(-9.15, 13.68) * mm});
            skArc(sketch, "E410.1.204", {"start": v(-13.7, 15.84) * mm, "mid": v(-13.65, 15.88) * mm, "end": v(-13.6, 15.92) * mm});
            skArc(sketch, "E410.1.205", {"start": v(-9.51, 14.77) * mm, "mid": v(-9.56, 14.8) * mm, "end": v(-9.6, 14.81) * mm});
            skArc(sketch, "E410.1.206", {"start": v(-11.4, 15.02) * mm, "mid": v(-11.37, 15.03) * mm, "end": v(-11.34, 15.05) * mm});
            skArc(sketch, "E410.1.207", {"start": v(-12.79, 14.56) * mm, "mid": v(-12.76, 14.59) * mm, "end": v(-12.73, 14.6) * mm});
            skArc(sketch, "E410.1.208", {"start": v(-12.5, 15.62) * mm, "mid": v(-12.64, 15.65) * mm, "end": v(-12.78, 15.69) * mm});
            skArc(sketch, "E410.1.209", {"start": v(-11.25, 15.1) * mm, "mid": v(-11.23, 15.12) * mm, "end": v(-11.21, 15.13) * mm});
            skArc(sketch, "E410.1.210", {"start": v(-11.2, 16.56) * mm, "mid": v(-11.23, 16.55) * mm, "end": v(-11.25, 16.53) * mm});
            skArc(sketch, "E410.1.211", {"start": v(-12.53, 16.7) * mm, "mid": v(-12.42, 16.75) * mm, "end": v(-12.32, 16.8) * mm});
            skArc(sketch, "E410.1.212", {"start": v(-11.52, 13.93) * mm, "mid": v(-11.59, 13.93) * mm, "end": v(-11.66, 13.93) * mm});
            skArc(sketch, "E410.1.213", {"start": v(-9.79, 14.75) * mm, "mid": v(-9.82, 14.7) * mm, "end": v(-9.83, 14.65) * mm});
            skArc(sketch, "E410.1.214", {"start": v(-12.32, 16.8) * mm, "mid": v(-12.24, 16.86) * mm, "end": v(-12.16, 16.93) * mm});
            skArc(sketch, "E410.1.215", {"start": v(-13.1, 15.8) * mm, "mid": v(-13.15, 15.81) * mm, "end": v(-13.2, 15.82) * mm});
            skArc(sketch, "E410.1.216", {"start": v(-11.34, 16.39) * mm, "mid": v(-11.36, 16.35) * mm, "end": v(-11.36, 16.3) * mm});
            skArc(sketch, "E410.1.217", {"start": v(-10.91, 15.27) * mm, "mid": v(-10.88, 15.3) * mm, "end": v(-10.84, 15.32) * mm});
            skArc(sketch, "E410.1.218", {"start": v(-17.18, 20.49) * mm, "mid": v(-17.34, 20.16) * mm, "end": v(-17.5, 19.84) * mm});
            skArc(sketch, "E410.1.219", {"start": v(-11.45, 16.1) * mm, "mid": v(-11.46, 16.07) * mm, "end": v(-11.47, 16.04) * mm});
            skArc(sketch, "E410.1.220", {"start": v(-16.9, 20.42) * mm, "mid": v(-16.86, 20.52) * mm, "end": v(-16.83, 20.61) * mm});
            skArc(sketch, "E410.1.221", {"start": v(-10.48, 15.67) * mm, "mid": v(-10.48, 15.7) * mm, "end": v(-10.48, 15.72) * mm});
            skArc(sketch, "E410.1.222", {"start": v(-16.43, 18.56) * mm, "mid": v(-16.28, 18.77) * mm, "end": v(-16.14, 19) * mm});
            skArc(sketch, "E410.1.223", {"start": v(-17.72, 19.64) * mm, "mid": v(-17.75, 19.64) * mm, "end": v(-17.78, 19.63) * mm});
            skArc(sketch, "E410.1.224", {"start": v(-17.78, 19.63) * mm, "mid": v(-17.9, 19.58) * mm, "end": v(-18.02, 19.54) * mm});
            skArc(sketch, "E410.1.225", {"start": v(-16.11, 19.05) * mm, "mid": v(-16.1, 19.08) * mm, "end": v(-16.09, 19.1) * mm});
            skArc(sketch, "E410.1.226", {"start": v(-18.02, 19.54) * mm, "mid": v(-18.2, 19.46) * mm, "end": v(-18.38, 19.38) * mm});
            skArc(sketch, "E410.1.227", {"start": v(-16.73, 21.03) * mm, "mid": v(-16.73, 21.14) * mm, "end": v(-16.74, 21.25) * mm});
            skArc(sketch, "E410.1.228", {"start": v(-11.54, 15.94) * mm, "mid": v(-11.58, 15.9) * mm, "end": v(-11.62, 15.87) * mm});
            skArc(sketch, "E410.1.229", {"start": v(-13.71, 15.81) * mm, "mid": v(-13.7, 15.83) * mm, "end": v(-13.7, 15.84) * mm});
            skArc(sketch, "E410.1.230", {"start": v(-9.46, 14.72) * mm, "mid": v(-9.48, 14.75) * mm, "end": v(-9.51, 14.77) * mm});
            skArc(sketch, "E410.1.231", {"start": v(-11.45, 15) * mm, "mid": v(-11.43, 15.01) * mm, "end": v(-11.4, 15.02) * mm});
            skArc(sketch, "E410.1.232", {"start": v(-16.75, 20.14) * mm, "mid": v(-16.82, 20.08) * mm, "end": v(-16.9, 20.03) * mm});
            skArc(sketch, "E410.1.233", {"start": v(-12.8, 14.53) * mm, "mid": v(-12.8, 14.55) * mm, "end": v(-12.79, 14.56) * mm});
            skArc(sketch, "E410.1.234", {"start": v(-15.87, 19.4) * mm, "mid": v(-15.77, 19.54) * mm, "end": v(-15.68, 19.69) * mm});
            skArc(sketch, "E410.1.235", {"start": v(-11.17, 16.57) * mm, "mid": v(-11.19, 16.57) * mm, "end": v(-11.2, 16.56) * mm});
            skArc(sketch, "E410.1.236", {"start": v(-15.68, 19.69) * mm, "mid": v(-15.53, 19.95) * mm, "end": v(-15.4, 20.23) * mm});
            skArc(sketch, "E410.1.237", {"start": v(-16.87, 21.37) * mm, "mid": v(-16.88, 21.34) * mm, "end": v(-16.88, 21.31) * mm});
            skArc(sketch, "E410.1.238", {"start": v(-12.64, 16.64) * mm, "mid": v(-12.59, 16.67) * mm, "end": v(-12.53, 16.7) * mm});
            skArc(sketch, "E410.1.239", {"start": v(-16.9, 21.2) * mm, "mid": v(-16.98, 20.98) * mm, "end": v(-17.05, 20.78) * mm});
            skArc(sketch, "E410.1.240", {"start": v(-17.01, 19.97) * mm, "mid": v(-17.02, 19.98) * mm, "end": v(-17.02, 19.98) * mm});
            skArc(sketch, "E410.1.241", {"start": v(-17.05, 20.78) * mm, "mid": v(-17.11, 20.63) * mm, "end": v(-17.18, 20.49) * mm});
            skArc(sketch, "E410.1.242", {"start": v(-11.42, 16.16) * mm, "mid": v(-11.44, 16.13) * mm, "end": v(-11.45, 16.1) * mm});
            skArc(sketch, "E410.1.243", {"start": v(-16.96, 20.2) * mm, "mid": v(-16.93, 20.31) * mm, "end": v(-16.9, 20.42) * mm});
            skArc(sketch, "E410.1.244", {"start": v(-10.5, 15.61) * mm, "mid": v(-10.5, 15.64) * mm, "end": v(-10.48, 15.67) * mm});
            skArc(sketch, "E410.1.245", {"start": v(-17.66, 19.66) * mm, "mid": v(-17.69, 19.65) * mm, "end": v(-17.72, 19.64) * mm});
            skArc(sketch, "E410.1.246", {"start": v(-11.5, 15.99) * mm, "mid": v(-11.52, 15.96) * mm, "end": v(-11.54, 15.94) * mm});
            skArc(sketch, "E410.1.247", {"start": v(-16.14, 19) * mm, "mid": v(-16.12, 19.02) * mm, "end": v(-16.11, 19.05) * mm});
            skArc(sketch, "E410.1.248", {"start": v(-16.4, 20.61) * mm, "mid": v(-16.43, 20.57) * mm, "end": v(-16.46, 20.52) * mm});
            skArc(sketch, "E410.1.249", {"start": v(-13.73, 15.78) * mm, "mid": v(-13.73, 15.8) * mm, "end": v(-13.71, 15.81) * mm});
            skArc(sketch, "E410.1.250", {"start": v(-9.38, 14.64) * mm, "mid": v(-9.42, 14.68) * mm, "end": v(-9.46, 14.72) * mm});
            skArc(sketch, "E410.1.251", {"start": v(-11.5, 14.97) * mm, "mid": v(-11.48, 14.99) * mm, "end": v(-11.45, 15) * mm});
            skArc(sketch, "E410.1.252", {"start": v(-16.64, 20.23) * mm, "mid": v(-16.7, 20.18) * mm, "end": v(-16.75, 20.14) * mm});
            skArc(sketch, "E410.1.253", {"start": v(-12.8, 14.5) * mm, "mid": v(-12.8, 14.51) * mm, "end": v(-12.8, 14.53) * mm});
            skArc(sketch, "E410.1.254", {"start": v(-16, 19.24) * mm, "mid": v(-15.93, 19.32) * mm, "end": v(-15.87, 19.4) * mm});
            skArc(sketch, "E410.1.255", {"start": v(-11.14, 16.56) * mm, "mid": v(-11.15, 16.57) * mm, "end": v(-11.17, 16.57) * mm});
            skArc(sketch, "E410.1.256", {"start": v(-16.85, 21.4) * mm, "mid": v(-16.86, 21.39) * mm, "end": v(-16.87, 21.37) * mm});
            skArc(sketch, "E410.1.257", {"start": v(-16.88, 21.31) * mm, "mid": v(-16.9, 21.25) * mm, "end": v(-16.9, 21.2) * mm});
            skArc(sketch, "E410.1.258", {"start": v(-17, 19.97) * mm, "mid": v(-17, 19.97) * mm, "end": v(-17.01, 19.97) * mm});
            skArc(sketch, "E410.1.259", {"start": v(-17, 20.1) * mm, "mid": v(-16.97, 20.15) * mm, "end": v(-16.96, 20.2) * mm});
            skArc(sketch, "E410.1.260", {"start": v(-11.39, 16.22) * mm, "mid": v(-11.4, 16.2) * mm, "end": v(-11.42, 16.16) * mm});
            skArc(sketch, "E410.1.261", {"start": v(-10.6, 15.49) * mm, "mid": v(-10.54, 15.54) * mm, "end": v(-10.5, 15.61) * mm});
            skArc(sketch, "E410.1.262", {"start": v(-17.57, 19.73) * mm, "mid": v(-17.6, 19.7) * mm, "end": v(-17.66, 19.66) * mm});
            skArc(sketch, "E410.1.263", {"start": v(-16.83, 20.61) * mm, "mid": v(-16.8, 20.71) * mm, "end": v(-16.77, 20.81) * mm});
            skArc(sketch, "E410.1.264", {"start": v(-13.72, 15.75) * mm, "mid": v(-13.73, 15.76) * mm, "end": v(-13.73, 15.78) * mm});
            skArc(sketch, "E410.1.265", {"start": v(-16.77, 20.81) * mm, "mid": v(-16.74, 20.92) * mm, "end": v(-16.73, 21.03) * mm});
            skArc(sketch, "E410.1.266", {"start": v(-9.3, 14.56) * mm, "mid": v(-9.34, 14.6) * mm, "end": v(-9.38, 14.64) * mm});
            skArc(sketch, "E410.1.267", {"start": v(-16.58, 20.33) * mm, "mid": v(-16.6, 20.28) * mm, "end": v(-16.64, 20.23) * mm});
            skArc(sketch, "E410.1.268", {"start": v(-12.77, 14.46) * mm, "mid": v(-12.79, 14.48) * mm, "end": v(-12.8, 14.5) * mm});
            skArc(sketch, "E410.1.269", {"start": v(-16.03, 19.2) * mm, "mid": v(-16.02, 19.22) * mm, "end": v(-16, 19.24) * mm});
            skArc(sketch, "E410.1.270", {"start": v(-11.08, 16.53) * mm, "mid": v(-11.1, 16.55) * mm, "end": v(-11.14, 16.56) * mm});
            skArc(sketch, "E410.1.271", {"start": v(-16.83, 21.42) * mm, "mid": v(-16.84, 21.41) * mm, "end": v(-16.85, 21.4) * mm});
            skArc(sketch, "E410.1.272", {"start": v(-16.97, 19.98) * mm, "mid": v(-16.98, 19.98) * mm, "end": v(-17, 19.97) * mm});
            skArc(sketch, "E410.1.273", {"start": v(-17.02, 20) * mm, "mid": v(-17, 20.05) * mm, "end": v(-17, 20.1) * mm});
            skArc(sketch, "E410.1.274", {"start": v(-11.36, 16.3) * mm, "mid": v(-11.37, 16.26) * mm, "end": v(-11.39, 16.22) * mm});
            skArc(sketch, "E410.1.275", {"start": v(-17.5, 19.84) * mm, "mid": v(-17.54, 19.79) * mm, "end": v(-17.57, 19.73) * mm});
            skArc(sketch, "E410.1.276", {"start": v(-12.48, 14.78) * mm, "mid": v(-12.43, 14.78) * mm, "end": v(-12.39, 14.78) * mm});
            skArc(sketch, "E410.1.277", {"start": v(-13.67, 15.74) * mm, "mid": v(-13.7, 15.74) * mm, "end": v(-13.72, 15.75) * mm});
            skArc(sketch, "E410.1.278", {"start": v(-16.34, 20.7) * mm, "mid": v(-16.37, 20.66) * mm, "end": v(-16.4, 20.61) * mm});
            skArc(sketch, "E410.1.279", {"start": v(-16.46, 20.52) * mm, "mid": v(-16.52, 20.43) * mm, "end": v(-16.58, 20.33) * mm});
            skArc(sketch, "E410.1.280", {"start": v(-16.07, 19.15) * mm, "mid": v(-16.05, 19.18) * mm, "end": v(-16.03, 19.2) * mm});
            skArc(sketch, "E410.1.281", {"start": v(-16.8, 21.4) * mm, "mid": v(-16.82, 21.41) * mm, "end": v(-16.83, 21.42) * mm});
            skArc(sketch, "E410.1.282", {"start": v(-16.9, 20.03) * mm, "mid": v(-16.93, 20) * mm, "end": v(-16.97, 19.98) * mm});
            skArc(sketch, "E410.1.283", {"start": v(-17.02, 19.98) * mm, "mid": v(-17.02, 20) * mm, "end": v(-17.02, 20) * mm});
            skArc(sketch, "E410.1.284", {"start": v(-12.52, 14.77) * mm, "mid": v(-12.5, 14.77) * mm, "end": v(-12.48, 14.78) * mm});
            skArc(sketch, "E410.1.285", {"start": v(-13.63, 15.76) * mm, "mid": v(-13.65, 15.75) * mm, "end": v(-13.67, 15.74) * mm});
            skArc(sketch, "E410.1.286", {"start": v(-16.09, 19.1) * mm, "mid": v(-16.08, 19.13) * mm, "end": v(-16.07, 19.15) * mm});
            skArc(sketch, "E410.1.287", {"start": v(-16.78, 21.37) * mm, "mid": v(-16.79, 21.4) * mm, "end": v(-16.8, 21.4) * mm});
            skArc(sketch, "E410.1.288", {"start": v(-12.57, 14.73) * mm, "mid": v(-12.55, 14.75) * mm, "end": v(-12.52, 14.77) * mm});
            skArc(sketch, "E410.1.289", {"start": v(-12.84, 18.66) * mm, "mid": v(-12.87, 18.59) * mm, "end": v(-12.9, 18.53) * mm});
            skArc(sketch, "E410.1.290", {"start": v(-11.91, 17.12) * mm, "mid": v(-11.84, 17.16) * mm, "end": v(-11.77, 17.19) * mm});
            skArc(sketch, "E410.1.291", {"start": v(-13.53, 15.79) * mm, "mid": v(-13.58, 15.78) * mm, "end": v(-13.63, 15.76) * mm});
            skArc(sketch, "E410.1.292", {"start": v(-11.16, 18.16) * mm, "mid": v(-11.27, 18.3) * mm, "end": v(-11.39, 18.46) * mm});
            skArc(sketch, "E410.1.293", {"start": v(-12.3, 19.17) * mm, "mid": v(-12.34, 19.21) * mm, "end": v(-12.39, 19.25) * mm});
            skArc(sketch, "E410.1.294", {"start": v(-11.39, 18.46) * mm, "mid": v(-11.48, 18.56) * mm, "end": v(-11.58, 18.66) * mm});
            skArc(sketch, "E410.1.295", {"start": v(-13.13, 18.34) * mm, "mid": v(-13.21, 18.28) * mm, "end": v(-13.3, 18.22) * mm});
            skArc(sketch, "E410.1.296", {"start": v(-11.46, 17.3) * mm, "mid": v(-11.42, 17.33) * mm, "end": v(-11.37, 17.35) * mm});
            skArc(sketch, "E410.1.297", {"start": v(-16.74, 21.25) * mm, "mid": v(-16.75, 21.31) * mm, "end": v(-16.78, 21.37) * mm});
            skArc(sketch, "E410.1.298", {"start": v(-11.3, 17.37) * mm, "mid": v(-11.22, 17.38) * mm, "end": v(-11.15, 17.4) * mm});
            skArc(sketch, "E410.1.299", {"start": v(-11.78, 18.78) * mm, "mid": v(-11.79, 18.8) * mm, "end": v(-11.8, 18.8) * mm});
            skArc(sketch, "E410.1.300", {"start": v(-10.96, 17.52) * mm, "mid": v(-10.95, 17.55) * mm, "end": v(-10.93, 17.58) * mm});
            skArc(sketch, "E410.1.301", {"start": v(-12.77, 19.12) * mm, "mid": v(-12.79, 19.07) * mm, "end": v(-12.8, 19.02) * mm});
            skArc(sketch, "E410.1.302", {"start": v(-12.8, 18.97) * mm, "mid": v(-12.79, 18.92) * mm, "end": v(-12.79, 18.88) * mm});
            skArc(sketch, "E410.1.303", {"start": v(-11.9, 18.74) * mm, "mid": v(-11.9, 18.74) * mm, "end": v(-11.91, 18.75) * mm});
            skArc(sketch, "E410.1.304", {"start": v(-10.93, 17.7) * mm, "mid": v(-10.93, 17.74) * mm, "end": v(-10.93, 17.78) * mm});
            skArc(sketch, "E410.1.305", {"start": v(-12.64, 14.67) * mm, "mid": v(-12.6, 14.7) * mm, "end": v(-12.57, 14.73) * mm});
            skArc(sketch, "E410.1.306", {"start": v(-16.11, 21.38) * mm, "mid": v(-16.14, 21.3) * mm, "end": v(-16.16, 21.22) * mm});
            skArc(sketch, "E410.1.307", {"start": v(-12.8, 18.77) * mm, "mid": v(-12.82, 18.71) * mm, "end": v(-12.84, 18.66) * mm});
            skArc(sketch, "E410.1.308", {"start": v(-12, 17.05) * mm, "mid": v(-11.96, 17.08) * mm, "end": v(-11.91, 17.12) * mm});
            skArc(sketch, "E410.1.309", {"start": v(-11.1, 18.08) * mm, "mid": v(-11.13, 18.12) * mm, "end": v(-11.16, 18.16) * mm});
            skArc(sketch, "E410.1.310", {"start": v(-12.2, 19.07) * mm, "mid": v(-12.25, 19.12) * mm, "end": v(-12.3, 19.17) * mm});
            skArc(sketch, "E410.1.311", {"start": v(-13.05, 18.4) * mm, "mid": v(-13.1, 18.37) * mm, "end": v(-13.13, 18.34) * mm});
            skArc(sketch, "E410.1.312", {"start": v(-11.37, 17.35) * mm, "mid": v(-11.33, 17.36) * mm, "end": v(-11.3, 17.37) * mm});
            skArc(sketch, "E410.1.313", {"start": v(-11.75, 18.75) * mm, "mid": v(-11.77, 18.77) * mm, "end": v(-11.78, 18.78) * mm});
            skArc(sketch, "E410.1.314", {"start": v(-11.07, 17.43) * mm, "mid": v(-11, 17.46) * mm, "end": v(-10.96, 17.52) * mm});
            skArc(sketch, "E410.1.315", {"start": v(-12.73, 19.2) * mm, "mid": v(-12.75, 19.16) * mm, "end": v(-12.77, 19.12) * mm});
            skArc(sketch, "E410.1.316", {"start": v(-12.8, 19.02) * mm, "mid": v(-12.8, 19) * mm, "end": v(-12.8, 18.97) * mm});
            skArc(sketch, "E410.1.317", {"start": v(-11.87, 18.75) * mm, "mid": v(-11.88, 18.74) * mm, "end": v(-11.9, 18.74) * mm});
            skArc(sketch, "E410.1.318", {"start": v(-10.92, 17.63) * mm, "mid": v(-10.92, 17.67) * mm, "end": v(-10.93, 17.7) * mm});
            skArc(sketch, "E410.1.319", {"start": v(-12.79, 18.88) * mm, "mid": v(-12.8, 18.83) * mm, "end": v(-12.8, 18.77) * mm});
            skArc(sketch, "E410.1.320", {"start": v(-11.01, 18) * mm, "mid": v(-11.06, 18.04) * mm, "end": v(-11.1, 18.08) * mm});
            skArc(sketch, "E410.1.321", {"start": v(-12.1, 18.98) * mm, "mid": v(-12.15, 19.02) * mm, "end": v(-12.2, 19.07) * mm});
            skArc(sketch, "E410.1.322", {"start": v(-12.97, 18.47) * mm, "mid": v(-13.01, 18.43) * mm, "end": v(-13.05, 18.4) * mm});
            skArc(sketch, "E410.1.323", {"start": v(-11.55, 17.27) * mm, "mid": v(-11.5, 17.29) * mm, "end": v(-11.46, 17.3) * mm});
            skArc(sketch, "E410.1.324", {"start": v(-11.72, 18.74) * mm, "mid": v(-11.74, 18.75) * mm, "end": v(-11.75, 18.75) * mm});
            skArc(sketch, "E410.1.325", {"start": v(-11.15, 17.4) * mm, "mid": v(-11.1, 17.4) * mm, "end": v(-11.07, 17.43) * mm});
            skArc(sketch, "E410.1.326", {"start": v(-12.66, 19.29) * mm, "mid": v(-12.7, 19.25) * mm, "end": v(-12.73, 19.2) * mm});
            skArc(sketch, "E410.1.327", {"start": v(-11.84, 18.77) * mm, "mid": v(-11.86, 18.76) * mm, "end": v(-11.87, 18.75) * mm});
            skArc(sketch, "E410.1.328", {"start": v(-10.93, 17.58) * mm, "mid": v(-10.93, 17.6) * mm, "end": v(-10.92, 17.63) * mm});
            skArc(sketch, "E410.1.329", {"start": v(-10.97, 17.95) * mm, "mid": v(-11, 17.97) * mm, "end": v(-11.01, 18) * mm});
            skArc(sketch, "E410.1.330", {"start": v(-12.9, 18.53) * mm, "mid": v(-12.94, 18.5) * mm, "end": v(-12.97, 18.47) * mm});
            skArc(sketch, "E410.1.331", {"start": v(-11.66, 17.22) * mm, "mid": v(-11.6, 17.24) * mm, "end": v(-11.55, 17.27) * mm});
            skArc(sketch, "E410.1.332", {"start": v(-11.65, 18.72) * mm, "mid": v(-11.69, 18.73) * mm, "end": v(-11.72, 18.74) * mm});
            skArc(sketch, "E410.1.333", {"start": v(-12.63, 19.32) * mm, "mid": v(-12.65, 19.3) * mm, "end": v(-12.66, 19.29) * mm});
            skArc(sketch, "E410.1.334", {"start": v(-11.8, 18.8) * mm, "mid": v(-11.83, 18.79) * mm, "end": v(-11.84, 18.77) * mm});
            skArc(sketch, "E410.1.335", {"start": v(-10.93, 17.86) * mm, "mid": v(-10.95, 17.9) * mm, "end": v(-10.97, 17.95) * mm});
            skArc(sketch, "E410.1.336", {"start": v(-11.99, 18.87) * mm, "mid": v(-12.04, 18.93) * mm, "end": v(-12.1, 18.98) * mm});
            skArc(sketch, "E410.1.337", {"start": v(-11.58, 18.66) * mm, "mid": v(-11.62, 18.7) * mm, "end": v(-11.65, 18.72) * mm});
            skArc(sketch, "E410.1.338", {"start": v(-12.58, 19.33) * mm, "mid": v(-12.6, 19.33) * mm, "end": v(-12.63, 19.32) * mm});
            skArc(sketch, "E410.1.339", {"start": v(-10.93, 17.78) * mm, "mid": v(-10.93, 17.82) * mm, "end": v(-10.93, 17.86) * mm});
            skArc(sketch, "E410.1.340", {"start": v(-11.93, 18.77) * mm, "mid": v(-11.95, 18.82) * mm, "end": v(-11.99, 18.87) * mm});
            skArc(sketch, "E410.1.341", {"start": v(-12.53, 19.32) * mm, "mid": v(-12.55, 19.33) * mm, "end": v(-12.58, 19.33) * mm});
            skArc(sketch, "E410.1.342", {"start": v(-11.91, 18.75) * mm, "mid": v(-11.92, 18.76) * mm, "end": v(-11.93, 18.77) * mm});
            skArc(sketch, "E410.1.343", {"start": v(-12.44, 19.29) * mm, "mid": v(-12.48, 19.3) * mm, "end": v(-12.53, 19.32) * mm});
            skArc(sketch, "E410.1.344", {"start": v(-15.27, 20.73) * mm, "mid": v(-15.27, 20.82) * mm, "end": v(-15.27, 20.91) * mm});
            skArc(sketch, "E410.1.345", {"start": v(-14.32, 22.03) * mm, "mid": v(-14.34, 22.06) * mm, "end": v(-14.37, 22.1) * mm});
            skArc(sketch, "E410.1.346", {"start": v(-14.67, 21.26) * mm, "mid": v(-14.59, 21.24) * mm, "end": v(-14.5, 21.25) * mm});
            skArc(sketch, "E410.1.347", {"start": v(-16.25, 20.84) * mm, "mid": v(-16.3, 20.77) * mm, "end": v(-16.34, 20.7) * mm});
            skArc(sketch, "E410.1.348", {"start": v(-14.37, 22.1) * mm, "mid": v(-14.41, 22.16) * mm, "end": v(-14.46, 22.22) * mm});
            skArc(sketch, "E410.1.349", {"start": v(-12.39, 19.25) * mm, "mid": v(-12.41, 19.27) * mm, "end": v(-12.44, 19.29) * mm});
            skArc(sketch, "E410.1.350", {"start": v(-15.02, 21.6) * mm, "mid": v(-15, 21.62) * mm, "end": v(-14.98, 21.64) * mm});
            skArc(sketch, "E410.1.351", {"start": v(-14.83, 22.43) * mm, "mid": v(-14.9, 22.44) * mm, "end": v(-14.96, 22.43) * mm});
            skArc(sketch, "E410.1.352", {"start": v(-14.84, 21.7) * mm, "mid": v(-14.83, 21.64) * mm, "end": v(-14.83, 21.57) * mm});
            skArc(sketch, "E410.1.353", {"start": v(-14.96, 22.43) * mm, "mid": v(-15.05, 22.4) * mm, "end": v(-15.15, 22.38) * mm});
            skArc(sketch, "E410.1.354", {"start": v(-15.15, 22.38) * mm, "mid": v(-15.26, 22.34) * mm, "end": v(-15.38, 22.3) * mm});
            skArc(sketch, "E410.1.355", {"start": v(-15.38, 22.3) * mm, "mid": v(-15.53, 22.2) * mm, "end": v(-15.66, 22.1) * mm});
            skArc(sketch, "E410.1.356", {"start": v(-15.4, 20.23) * mm, "mid": v(-15.34, 20.38) * mm, "end": v(-15.29, 20.53) * mm});
            skArc(sketch, "E410.1.357", {"start": v(-14.29, 21.5) * mm, "mid": v(-14.3, 21.53) * mm, "end": v(-14.3, 21.56) * mm});
            skArc(sketch, "E410.1.358", {"start": v(-14.84, 21.41) * mm, "mid": v(-14.83, 21.38) * mm, "end": v(-14.82, 21.35) * mm});
            skArc(sketch, "E410.1.359", {"start": v(-15.29, 20.53) * mm, "mid": v(-15.27, 20.63) * mm, "end": v(-15.27, 20.73) * mm});
            skArc(sketch, "E410.1.360", {"start": v(-15.81, 21.92) * mm, "mid": v(-15.93, 21.75) * mm, "end": v(-16.03, 21.57) * mm});
            skArc(sketch, "E410.1.361", {"start": v(-16.16, 21.22) * mm, "mid": v(-16.17, 21.15) * mm, "end": v(-16.18, 21.08) * mm});
            skArc(sketch, "E410.1.362", {"start": v(-14.29, 21.83) * mm, "mid": v(-14.29, 21.87) * mm, "end": v(-14.3, 21.92) * mm});
            skArc(sketch, "E410.1.363", {"start": v(-15.27, 21.1) * mm, "mid": v(-15.26, 21.15) * mm, "end": v(-15.26, 21.2) * mm});
            skArc(sketch, "E410.1.364", {"start": v(-14.3, 21.92) * mm, "mid": v(-14.3, 21.98) * mm, "end": v(-14.32, 22.03) * mm});
            skArc(sketch, "E410.1.365", {"start": v(-15.26, 21.2) * mm, "mid": v(-15.24, 21.27) * mm, "end": v(-15.22, 21.33) * mm});
            skArc(sketch, "E410.1.366", {"start": v(-16.2, 20.94) * mm, "mid": v(-16.23, 20.9) * mm, "end": v(-16.25, 20.84) * mm});
            skArc(sketch, "E410.1.367", {"start": v(-15.08, 21.56) * mm, "mid": v(-15.05, 21.58) * mm, "end": v(-15.02, 21.6) * mm});
            skArc(sketch, "E410.1.368", {"start": v(-14.7, 22.4) * mm, "mid": v(-14.77, 22.43) * mm, "end": v(-14.83, 22.43) * mm});
            skArc(sketch, "E410.1.369", {"start": v(-14.87, 21.72) * mm, "mid": v(-14.85, 21.72) * mm, "end": v(-14.84, 21.7) * mm});
            skArc(sketch, "E410.1.370", {"start": v(-14.3, 21.46) * mm, "mid": v(-14.29, 21.48) * mm, "end": v(-14.29, 21.5) * mm});
            skArc(sketch, "E410.1.371", {"start": v(-14.84, 21.46) * mm, "mid": v(-14.84, 21.44) * mm, "end": v(-14.84, 21.41) * mm});
            skArc(sketch, "E410.1.372", {"start": v(-15.66, 22.1) * mm, "mid": v(-15.74, 22.01) * mm, "end": v(-15.81, 21.92) * mm});
            skArc(sketch, "E410.1.373", {"start": v(-16.03, 21.57) * mm, "mid": v(-16.08, 21.48) * mm, "end": v(-16.11, 21.38) * mm});
            skArc(sketch, "E410.1.374", {"start": v(-14.3, 21.65) * mm, "mid": v(-14.29, 21.74) * mm, "end": v(-14.29, 21.83) * mm});
            skArc(sketch, "E410.1.375", {"start": v(-15.27, 20.91) * mm, "mid": v(-15.28, 21) * mm, "end": v(-15.27, 21.1) * mm});
            skArc(sketch, "E410.1.376", {"start": v(-16.18, 21.08) * mm, "mid": v(-16.19, 21.01) * mm, "end": v(-16.2, 20.94) * mm});
            skArc(sketch, "E410.1.377", {"start": v(-15.17, 21.45) * mm, "mid": v(-15.13, 21.51) * mm, "end": v(-15.08, 21.56) * mm});
            skArc(sketch, "E410.1.378", {"start": v(-14.56, 22.32) * mm, "mid": v(-14.63, 22.37) * mm, "end": v(-14.7, 22.4) * mm});
            skArc(sketch, "E410.1.379", {"start": v(-14.9, 21.71) * mm, "mid": v(-14.88, 21.72) * mm, "end": v(-14.87, 21.72) * mm});
            skArc(sketch, "E410.1.380", {"start": v(-14.3, 21.44) * mm, "mid": v(-14.3, 21.45) * mm, "end": v(-14.3, 21.46) * mm});
            skArc(sketch, "E410.1.381", {"start": v(-14.84, 21.52) * mm, "mid": v(-14.84, 21.49) * mm, "end": v(-14.84, 21.46) * mm});
            skArc(sketch, "E410.1.382", {"start": v(-14.3, 21.56) * mm, "mid": v(-14.3, 21.6) * mm, "end": v(-14.3, 21.65) * mm});
            skArc(sketch, "E410.1.383", {"start": v(-15.22, 21.33) * mm, "mid": v(-15.2, 21.4) * mm, "end": v(-15.17, 21.45) * mm});
            skArc(sketch, "E410.1.384", {"start": v(-14.51, 22.28) * mm, "mid": v(-14.53, 22.3) * mm, "end": v(-14.56, 22.32) * mm});
            skArc(sketch, "E410.1.385", {"start": v(-14.98, 21.64) * mm, "mid": v(-14.94, 21.68) * mm, "end": v(-14.9, 21.71) * mm});
            skArc(sketch, "E410.1.386", {"start": v(-14.33, 21.42) * mm, "mid": v(-14.32, 21.43) * mm, "end": v(-14.3, 21.44) * mm});
            skArc(sketch, "E410.1.387", {"start": v(-14.83, 21.57) * mm, "mid": v(-14.83, 21.54) * mm, "end": v(-14.84, 21.52) * mm});
            skArc(sketch, "E410.1.388", {"start": v(-14.46, 22.22) * mm, "mid": v(-14.49, 22.25) * mm, "end": v(-14.51, 22.28) * mm});
            skArc(sketch, "E410.1.389", {"start": v(-14.35, 21.4) * mm, "mid": v(-14.34, 21.41) * mm, "end": v(-14.33, 21.42) * mm});
            skArc(sketch, "E410.1.390", {"start": v(-14.37, 21.38) * mm, "mid": v(-14.36, 21.39) * mm, "end": v(-14.35, 21.4) * mm});
            skArc(sketch, "E410.1.391", {"start": v(-14.38, 21.36) * mm, "mid": v(-14.37, 21.37) * mm, "end": v(-14.37, 21.38) * mm});
            skArc(sketch, "E410.1.392", {"start": v(-14.4, 21.35) * mm, "mid": v(-14.4, 21.36) * mm, "end": v(-14.38, 21.36) * mm});
            skArc(sketch, "E410.1.393", {"start": v(-14.43, 21.31) * mm, "mid": v(-14.42, 21.33) * mm, "end": v(-14.4, 21.35) * mm});
            skArc(sketch, "E410.1.394", {"start": v(-14.45, 21.27) * mm, "mid": v(-14.44, 21.3) * mm, "end": v(-14.43, 21.31) * mm});
            skArc(sketch, "E410.1.395", {"start": v(-14.5, 21.25) * mm, "mid": v(-14.47, 21.25) * mm, "end": v(-14.45, 21.27) * mm});
            skArc(sketch, "E410.1.396", {"start": v(-14.74, 21.27) * mm, "mid": v(-14.7, 21.26) * mm, "end": v(-14.67, 21.26) * mm});
            skArc(sketch, "E410.1.397", {"start": v(-14.77, 21.29) * mm, "mid": v(-14.75, 21.28) * mm, "end": v(-14.74, 21.27) * mm});
            skArc(sketch, "E410.1.398", {"start": v(-14.8, 21.3) * mm, "mid": v(-14.78, 21.3) * mm, "end": v(-14.77, 21.29) * mm});
            skArc(sketch, "E410.1.399", {"start": v(-14.82, 21.35) * mm, "mid": v(-14.8, 21.33) * mm, "end": v(-14.8, 21.3) * mm});
            skArc(sketch, "E410.2.0", {"start": v(-12.83, -20.05) * mm, "mid": v(-12.71, -19.98) * mm, "end": v(-12.6, -19.9) * mm});
            skArc(sketch, "E410.2.1", {"start": v(-12.5, -19.83) * mm, "mid": v(-12.44, -19.77) * mm, "end": v(-12.38, -19.72) * mm});
            skArc(sketch, "E410.2.2", {"start": v(-12.04, -19.41) * mm, "mid": v(-11.7, -19.04) * mm, "end": v(-11.37, -18.64) * mm});
            skArc(sketch, "E410.2.3", {"start": v(-12.98, -20.13) * mm, "mid": v(-12.9, -20.09) * mm, "end": v(-12.83, -20.05) * mm});
            skArc(sketch, "E410.2.4", {"start": v(-12.6, -19.9) * mm, "mid": v(-12.55, -19.87) * mm, "end": v(-12.5, -19.83) * mm});
            skArc(sketch, "E410.2.5", {"start": v(-18.55, -19.56) * mm, "mid": v(-18.46, -19.64) * mm, "end": v(-18.38, -19.72) * mm});
            skArc(sketch, "E410.2.6", {"start": v(-12.2, -19.56) * mm, "mid": v(-12.12, -19.49) * mm, "end": v(-12.04, -19.41) * mm});
            skArc(sketch, "E410.2.7", {"start": v(-18, -20.23) * mm, "mid": v(-17.93, -20.32) * mm, "end": v(-17.85, -20.4) * mm});
            skArc(sketch, "E410.2.8", {"start": v(-17.85, -20.4) * mm, "mid": v(-17.7, -20.53) * mm, "end": v(-17.51, -20.63) * mm});
            skArc(sketch, "E410.2.9", {"start": v(-17.05, -20.68) * mm, "mid": v(-16.93, -20.67) * mm, "end": v(-16.82, -20.65) * mm});
            skArc(sketch, "E410.2.10", {"start": v(-16.82, -20.65) * mm, "mid": v(-16.73, -20.65) * mm, "end": v(-16.64, -20.65) * mm});
            skArc(sketch, "E410.2.11", {"start": v(-16.57, -20.66) * mm, "mid": v(-16.53, -20.67) * mm, "end": v(-16.49, -20.7) * mm});
            skArc(sketch, "E410.2.12", {"start": v(-18.7, -19.37) * mm, "mid": v(-18.63, -19.47) * mm, "end": v(-18.55, -19.56) * mm});
            skArc(sketch, "E410.2.13", {"start": v(-12.38, -19.72) * mm, "mid": v(-12.3, -19.64) * mm, "end": v(-12.2, -19.56) * mm});
            skArc(sketch, "E410.2.14", {"start": v(-18.25, -19.87) * mm, "mid": v(-18.16, -19.97) * mm, "end": v(-18.08, -20.09) * mm});
            skArc(sketch, "E410.2.15", {"start": v(-18.08, -20.09) * mm, "mid": v(-18.04, -20.16) * mm, "end": v(-18, -20.23) * mm});
            skArc(sketch, "E410.2.16", {"start": v(-17.17, -20.7) * mm, "mid": v(-17.1, -20.7) * mm, "end": v(-17.05, -20.68) * mm});
            skArc(sketch, "E410.2.17", {"start": v(-16.64, -20.65) * mm, "mid": v(-16.6, -20.65) * mm, "end": v(-16.57, -20.66) * mm});
            skArc(sketch, "E410.2.18", {"start": v(-18.38, -19.72) * mm, "mid": v(-18.31, -19.8) * mm, "end": v(-18.25, -19.87) * mm});
            skArc(sketch, "E410.2.19", {"start": v(-17.51, -20.63) * mm, "mid": v(-17.34, -20.68) * mm, "end": v(-17.17, -20.7) * mm});
            skArc(sketch, "E410.2.20", {"start": v(-11.37, -18.64) * mm, "mid": v(-11.27, -18.5) * mm, "end": v(-11.18, -18.35) * mm});
            skArc(sketch, "E410.2.21", {"start": v(-13.37, -20.25) * mm, "mid": v(-13.26, -20.23) * mm, "end": v(-13.16, -20.2) * mm});
            skArc(sketch, "E410.2.22", {"start": v(-13.16, -20.2) * mm, "mid": v(-13.07, -20.17) * mm, "end": v(-12.98, -20.13) * mm});
            skArc(sketch, "E410.2.23", {"start": v(-11.47, -13.89) * mm, "mid": v(-11.59, -13.52) * mm, "end": v(-11.69, -13.15) * mm});
            skArc(sketch, "E410.2.24", {"start": v(-19.21, -18.7) * mm, "mid": v(-19.12, -18.84) * mm, "end": v(-19.02, -18.98) * mm});
            skArc(sketch, "E410.2.25", {"start": v(-18.9, -19.12) * mm, "mid": v(-18.8, -19.24) * mm, "end": v(-18.7, -19.37) * mm});
            skArc(sketch, "E410.2.26", {"start": v(-13.7, -20.28) * mm, "mid": v(-13.54, -20.27) * mm, "end": v(-13.37, -20.25) * mm});
            skArc(sketch, "E410.2.27", {"start": v(-11.4, -14.18) * mm, "mid": v(-11.42, -14.03) * mm, "end": v(-11.47, -13.89) * mm});
            skArc(sketch, "E410.2.28", {"start": v(-11.74, -12.96) * mm, "mid": v(-11.77, -12.86) * mm, "end": v(-11.8, -12.77) * mm});
            skArc(sketch, "E410.2.29", {"start": v(-19.38, -18.38) * mm, "mid": v(-19.3, -18.54) * mm, "end": v(-19.21, -18.7) * mm});
            skArc(sketch, "E410.2.30", {"start": v(-19.02, -18.98) * mm, "mid": v(-18.96, -19.05) * mm, "end": v(-18.9, -19.12) * mm});
            skArc(sketch, "E410.2.31", {"start": v(-11.4, -15.37) * mm, "mid": v(-11.38, -15.13) * mm, "end": v(-11.38, -14.9) * mm});
            skArc(sketch, "E410.2.32", {"start": v(-11.38, -14.9) * mm, "mid": v(-11.38, -14.82) * mm, "end": v(-11.37, -14.75) * mm});
            skArc(sketch, "E410.2.33", {"start": v(-11.37, -14.75) * mm, "mid": v(-11.36, -14.62) * mm, "end": v(-11.37, -14.5) * mm});
            skArc(sketch, "E410.2.34", {"start": v(-11.37, -14.5) * mm, "mid": v(-11.38, -14.34) * mm, "end": v(-11.4, -14.18) * mm});
            skArc(sketch, "E410.2.35", {"start": v(-11.69, -13.15) * mm, "mid": v(-11.71, -13.05) * mm, "end": v(-11.74, -12.96) * mm});
            skArc(sketch, "E410.2.36", {"start": v(-11.85, -12.66) * mm, "mid": v(-11.88, -12.6) * mm, "end": v(-11.92, -12.55) * mm});
            skArc(sketch, "E410.2.37", {"start": v(-12.03, -12.36) * mm, "mid": v(-12.06, -12.3) * mm, "end": v(-12.1, -12.24) * mm});
            skArc(sketch, "E410.2.38", {"start": v(-12.1, -12.24) * mm, "mid": v(-12.3, -12) * mm, "end": v(-12.49, -11.75) * mm});
            skArc(sketch, "E410.2.39", {"start": v(-11.8, -12.77) * mm, "mid": v(-11.83, -12.72) * mm, "end": v(-11.85, -12.66) * mm});
            skArc(sketch, "E410.2.40", {"start": v(-11.92, -12.55) * mm, "mid": v(-11.97, -12.45) * mm, "end": v(-12.03, -12.36) * mm});
            skArc(sketch, "E410.2.41", {"start": v(-11.62, -16.66) * mm, "mid": v(-11.55, -16.4) * mm, "end": v(-11.48, -16.15) * mm});
            skArc(sketch, "E410.2.42", {"start": v(-11.48, -16.15) * mm, "mid": v(-11.43, -15.87) * mm, "end": v(-11.4, -15.59) * mm});
            skArc(sketch, "E410.2.43", {"start": v(-11.4, -15.59) * mm, "mid": v(-11.4, -15.48) * mm, "end": v(-11.4, -15.37) * mm});
            skArc(sketch, "E410.2.44", {"start": v(-11.02, -17.9) * mm, "mid": v(-11.03, -17.87) * mm, "end": v(-11.04, -17.84) * mm});
            skArc(sketch, "E410.2.45", {"start": v(-11.04, -17.84) * mm, "mid": v(-11.07, -17.77) * mm, "end": v(-11.1, -17.71) * mm});
            skArc(sketch, "E410.2.46", {"start": v(-11.34, -17.44) * mm, "mid": v(-11.4, -17.4) * mm, "end": v(-11.45, -17.34) * mm});
            skArc(sketch, "E410.2.47", {"start": v(-11.6, -17.22) * mm, "mid": v(-11.66, -17.18) * mm, "end": v(-11.73, -17.14) * mm});
            skArc(sketch, "E410.2.48", {"start": v(-14.96, -21) * mm, "mid": v(-14.9, -20.85) * mm, "end": v(-14.86, -20.68) * mm});
            skArc(sketch, "E410.2.49", {"start": v(-14.85, -20.52) * mm, "mid": v(-14.84, -20.43) * mm, "end": v(-14.85, -20.33) * mm});
            skArc(sketch, "E410.2.50", {"start": v(-11.62, -16.68) * mm, "mid": v(-11.62, -16.67) * mm, "end": v(-11.62, -16.66) * mm});
            skArc(sketch, "E410.2.51", {"start": v(-16.3, -20.8) * mm, "mid": v(-16.16, -20.88) * mm, "end": v(-16.02, -20.96) * mm});
            skArc(sketch, "E410.2.52", {"start": v(-14.5, -20.24) * mm, "mid": v(-14.38, -20.25) * mm, "end": v(-14.26, -20.26) * mm});
            skArc(sketch, "E410.2.53", {"start": v(-16.02, -20.96) * mm, "mid": v(-15.92, -21.02) * mm, "end": v(-15.82, -21.07) * mm});
            skArc(sketch, "E410.2.54", {"start": v(-14.26, -20.26) * mm, "mid": v(-13.98, -20.28) * mm, "end": v(-13.7, -20.28) * mm});
            skArc(sketch, "E410.2.55", {"start": v(-15.5, -21.2) * mm, "mid": v(-15.4, -21.22) * mm, "end": v(-15.27, -21.24) * mm});
            skArc(sketch, "E410.2.56", {"start": v(-11.03, -17.97) * mm, "mid": v(-11.02, -17.93) * mm, "end": v(-11.02, -17.9) * mm});
            skArc(sketch, "E410.2.57", {"start": v(-11.1, -17.71) * mm, "mid": v(-11.22, -17.57) * mm, "end": v(-11.34, -17.44) * mm});
            skArc(sketch, "E410.2.58", {"start": v(-11.45, -17.34) * mm, "mid": v(-11.53, -17.28) * mm, "end": v(-11.6, -17.22) * mm});
            skArc(sketch, "E410.2.59", {"start": v(-15.27, -21.24) * mm, "mid": v(-15.2, -21.23) * mm, "end": v(-15.14, -21.2) * mm});
            skArc(sketch, "E410.2.60", {"start": v(-15.14, -21.2) * mm, "mid": v(-15.1, -21.17) * mm, "end": v(-15.05, -21.12) * mm});
            skArc(sketch, "E410.2.61", {"start": v(-15.05, -21.12) * mm, "mid": v(-15, -21.07) * mm, "end": v(-14.96, -21) * mm});
            skArc(sketch, "E410.2.62", {"start": v(-17.97, -16.98) * mm, "mid": v(-18.05, -16.93) * mm, "end": v(-18.1, -16.87) * mm});
            skArc(sketch, "E410.2.63", {"start": v(-17.37, -15.93) * mm, "mid": v(-17.24, -16.26) * mm, "end": v(-17.12, -16.59) * mm});
            skArc(sketch, "E410.2.64", {"start": v(-14.86, -20.68) * mm, "mid": v(-14.85, -20.6) * mm, "end": v(-14.85, -20.52) * mm});
            skArc(sketch, "E410.2.65", {"start": v(-18.1, -16.87) * mm, "mid": v(-18.13, -16.85) * mm, "end": v(-18.14, -16.83) * mm});
            skArc(sketch, "E410.2.66", {"start": v(-17.12, -16.59) * mm, "mid": v(-17.06, -16.72) * mm, "end": v(-17, -16.86) * mm});
            skArc(sketch, "E410.2.67", {"start": v(-17, -16.86) * mm, "mid": v(-16.95, -16.97) * mm, "end": v(-16.9, -17.08) * mm});
            skArc(sketch, "E410.2.68", {"start": v(-18.3, -16.64) * mm, "mid": v(-18.43, -16.53) * mm, "end": v(-18.56, -16.43) * mm});
            skArc(sketch, "E410.2.69", {"start": v(-11.65, -16.75) * mm, "mid": v(-11.64, -16.72) * mm, "end": v(-11.62, -16.68) * mm});
            skArc(sketch, "E410.2.70", {"start": v(-17, -17.17) * mm, "mid": v(-17.09, -17.19) * mm, "end": v(-17.18, -17.21) * mm});
            skArc(sketch, "E410.2.71", {"start": v(-16.49, -20.7) * mm, "mid": v(-16.39, -20.75) * mm, "end": v(-16.3, -20.8) * mm});
            skArc(sketch, "E410.2.72", {"start": v(-17.18, -17.21) * mm, "mid": v(-17.28, -17.24) * mm, "end": v(-17.37, -17.26) * mm});
            skArc(sketch, "E410.2.73", {"start": v(-14.63, -20.23) * mm, "mid": v(-14.57, -20.23) * mm, "end": v(-14.5, -20.24) * mm});
            skArc(sketch, "E410.2.74", {"start": v(-17.48, -17.27) * mm, "mid": v(-17.53, -17.27) * mm, "end": v(-17.58, -17.27) * mm});
            skArc(sketch, "E410.2.75", {"start": v(-15.82, -21.07) * mm, "mid": v(-15.66, -21.14) * mm, "end": v(-15.5, -21.2) * mm});
            skArc(sketch, "E410.2.76", {"start": v(-11.75, -17.08) * mm, "mid": v(-11.73, -17.04) * mm, "end": v(-11.72, -16.99) * mm});
            skArc(sketch, "E410.2.77", {"start": v(-11.06, -18.09) * mm, "mid": v(-11.04, -18.03) * mm, "end": v(-11.03, -17.97) * mm});
            skArc(sketch, "E410.2.78", {"start": v(-17.63, -15) * mm, "mid": v(-17.56, -15.33) * mm, "end": v(-17.46, -15.66) * mm});
            skArc(sketch, "E410.2.79", {"start": v(-17.74, -17.17) * mm, "mid": v(-17.79, -17.12) * mm, "end": v(-17.83, -17.08) * mm});
            skArc(sketch, "E410.2.80", {"start": v(-17.46, -15.66) * mm, "mid": v(-17.42, -15.8) * mm, "end": v(-17.37, -15.93) * mm});
            skArc(sketch, "E410.2.81", {"start": v(-12.95, -10.68) * mm, "mid": v(-13, -10.51) * mm, "end": v(-13.06, -10.34) * mm});
            skArc(sketch, "E410.2.82", {"start": v(-13.06, -10.34) * mm, "mid": v(-13.12, -10.17) * mm, "end": v(-13.19, -10) * mm});
            skArc(sketch, "E410.2.83", {"start": v(-18.14, -16.83) * mm, "mid": v(-18.22, -16.73) * mm, "end": v(-18.3, -16.64) * mm});
            skArc(sketch, "E410.2.84", {"start": v(-14.28, -9.12) * mm, "mid": v(-14.36, -9.17) * mm, "end": v(-14.45, -9.22) * mm});
            skArc(sketch, "E410.2.85", {"start": v(-13.31, -9.8) * mm, "mid": v(-13.41, -9.67) * mm, "end": v(-13.5, -9.53) * mm});
            skArc(sketch, "E410.2.86", {"start": v(-14.45, -9.22) * mm, "mid": v(-14.5, -9.26) * mm, "end": v(-14.56, -9.3) * mm});
            skArc(sketch, "E410.2.87", {"start": v(-16.9, -17.15) * mm, "mid": v(-16.95, -17.16) * mm, "end": v(-17, -17.17) * mm});
            skArc(sketch, "E410.2.88", {"start": v(-11.66, -16.79) * mm, "mid": v(-11.66, -16.77) * mm, "end": v(-11.65, -16.75) * mm});
            skArc(sketch, "E410.2.89", {"start": v(-13.6, -9.3) * mm, "mid": v(-13.63, -9.26) * mm, "end": v(-13.66, -9.21) * mm});
            skArc(sketch, "E410.2.90", {"start": v(-14.7, -20.22) * mm, "mid": v(-14.66, -20.22) * mm, "end": v(-14.63, -20.23) * mm});
            skArc(sketch, "E410.2.91", {"start": v(-17.37, -17.26) * mm, "mid": v(-17.43, -17.27) * mm, "end": v(-17.48, -17.27) * mm});
            skArc(sketch, "E410.2.92", {"start": v(-12.75, -11.41) * mm, "mid": v(-12.78, -11.33) * mm, "end": v(-12.8, -11.26) * mm});
            skArc(sketch, "E410.2.93", {"start": v(-13.81, -8.98) * mm, "mid": v(-13.84, -8.97) * mm, "end": v(-13.88, -8.96) * mm});
            skArc(sketch, "E410.2.94", {"start": v(-11.75, -17.12) * mm, "mid": v(-11.75, -17.1) * mm, "end": v(-11.75, -17.08) * mm});
            skArc(sketch, "E410.2.95", {"start": v(-17.66, -14.83) * mm, "mid": v(-17.64, -14.91) * mm, "end": v(-17.63, -15) * mm});
            skArc(sketch, "E410.2.96", {"start": v(-11.18, -18.35) * mm, "mid": v(-11.11, -18.22) * mm, "end": v(-11.06, -18.09) * mm});
            skArc(sketch, "E410.2.97", {"start": v(-17.7, -17.22) * mm, "mid": v(-17.72, -17.2) * mm, "end": v(-17.74, -17.17) * mm});
            skArc(sketch, "E410.2.98", {"start": v(-12.87, -11.03) * mm, "mid": v(-12.9, -10.92) * mm, "end": v(-12.92, -10.8) * mm});
            skArc(sketch, "E410.2.99", {"start": v(-14.85, -9.69) * mm, "mid": v(-14.8, -9.74) * mm, "end": v(-14.75, -9.79) * mm});
            skArc(sketch, "E410.2.100", {"start": v(-13.92, -8.95) * mm, "mid": v(-13.94, -8.95) * mm, "end": v(-13.96, -8.95) * mm});
            skArc(sketch, "E410.2.101", {"start": v(-12.92, -10.8) * mm, "mid": v(-12.93, -10.74) * mm, "end": v(-12.95, -10.68) * mm});
            skArc(sketch, "E410.2.102", {"start": v(-14.2, -9.06) * mm, "mid": v(-14.24, -9.1) * mm, "end": v(-14.28, -9.12) * mm});
            skArc(sketch, "E410.2.103", {"start": v(-13.26, -9.87) * mm, "mid": v(-13.28, -9.84) * mm, "end": v(-13.31, -9.8) * mm});
            skArc(sketch, "E410.2.104", {"start": v(-14.41, -9.91) * mm, "mid": v(-14.37, -9.93) * mm, "end": v(-14.32, -9.95) * mm});
            skArc(sketch, "E410.2.105", {"start": v(-16.9, -17.14) * mm, "mid": v(-16.9, -17.15) * mm, "end": v(-16.9, -17.15) * mm});
            skArc(sketch, "E410.2.106", {"start": v(-11.68, -16.87) * mm, "mid": v(-11.67, -16.83) * mm, "end": v(-11.66, -16.79) * mm});
            skArc(sketch, "E410.2.107", {"start": v(-13.55, -9.41) * mm, "mid": v(-13.58, -9.36) * mm, "end": v(-13.6, -9.3) * mm});
            skArc(sketch, "E410.2.108", {"start": v(-14.75, -20.2) * mm, "mid": v(-14.72, -20.2) * mm, "end": v(-14.7, -20.22) * mm});
            skArc(sketch, "E410.2.109", {"start": v(-12.74, -11.45) * mm, "mid": v(-12.75, -11.43) * mm, "end": v(-12.75, -11.41) * mm});
            skArc(sketch, "E410.2.110", {"start": v(-17.74, -14.54) * mm, "mid": v(-17.7, -14.68) * mm, "end": v(-17.66, -14.83) * mm});
            skArc(sketch, "E410.2.111", {"start": v(-17.65, -17.25) * mm, "mid": v(-17.67, -17.24) * mm, "end": v(-17.7, -17.22) * mm});
            skArc(sketch, "E410.2.112", {"start": v(-12.8, -11.26) * mm, "mid": v(-12.84, -11.15) * mm, "end": v(-12.87, -11.03) * mm});
            skArc(sketch, "E410.2.113", {"start": v(-11.73, -17.14) * mm, "mid": v(-11.74, -17.13) * mm, "end": v(-11.75, -17.12) * mm});
            skArc(sketch, "E410.2.114", {"start": v(-14.86, -9.66) * mm, "mid": v(-14.86, -9.67) * mm, "end": v(-14.85, -9.69) * mm});
            skArc(sketch, "E410.2.115", {"start": v(-13.88, -8.96) * mm, "mid": v(-13.9, -8.96) * mm, "end": v(-13.92, -8.95) * mm});
            skArc(sketch, "E410.2.116", {"start": v(-14.12, -9) * mm, "mid": v(-14.16, -9.02) * mm, "end": v(-14.2, -9.06) * mm});
            skArc(sketch, "E410.2.117", {"start": v(-13.19, -10) * mm, "mid": v(-13.22, -9.93) * mm, "end": v(-13.26, -9.87) * mm});
            skArc(sketch, "E410.2.118", {"start": v(-16.88, -17.11) * mm, "mid": v(-16.88, -17.13) * mm, "end": v(-16.9, -17.14) * mm});
            skArc(sketch, "E410.2.119", {"start": v(-11.7, -16.93) * mm, "mid": v(-11.7, -16.9) * mm, "end": v(-11.68, -16.87) * mm});
            skArc(sketch, "E410.2.120", {"start": v(-13.5, -9.53) * mm, "mid": v(-13.53, -9.47) * mm, "end": v(-13.55, -9.41) * mm});
            skArc(sketch, "E410.2.121", {"start": v(-14.81, -20.2) * mm, "mid": v(-14.78, -20.2) * mm, "end": v(-14.75, -20.2) * mm});
            skArc(sketch, "E410.2.122", {"start": v(-14.02, -10.23) * mm, "mid": v(-14, -10.26) * mm, "end": v(-13.98, -10.28) * mm});
            skArc(sketch, "E410.2.123", {"start": v(-12.7, -11.51) * mm, "mid": v(-12.72, -11.48) * mm, "end": v(-12.74, -11.45) * mm});
            skArc(sketch, "E410.2.124", {"start": v(-13.95, -10.36) * mm, "mid": v(-13.94, -10.4) * mm, "end": v(-13.92, -10.45) * mm});
            skArc(sketch, "E410.2.125", {"start": v(-13.74, -9.04) * mm, "mid": v(-13.77, -9.01) * mm, "end": v(-13.81, -8.98) * mm});
            skArc(sketch, "E410.2.126", {"start": v(-17.82, -14.25) * mm, "mid": v(-17.78, -14.4) * mm, "end": v(-17.74, -14.54) * mm});
            skArc(sketch, "E410.2.127", {"start": v(-17.58, -17.27) * mm, "mid": v(-17.62, -17.26) * mm, "end": v(-17.65, -17.25) * mm});
            skArc(sketch, "E410.2.128", {"start": v(-13.84, -10.74) * mm, "mid": v(-13.82, -10.96) * mm, "end": v(-13.84, -11.19) * mm});
            skArc(sketch, "E410.2.129", {"start": v(-14.85, -9.64) * mm, "mid": v(-14.86, -9.65) * mm, "end": v(-14.86, -9.66) * mm});
            skArc(sketch, "E410.2.130", {"start": v(-17.83, -17.08) * mm, "mid": v(-17.9, -17.02) * mm, "end": v(-17.97, -16.98) * mm});
            skArc(sketch, "E410.2.131", {"start": v(-14.08, -8.96) * mm, "mid": v(-14.1, -8.97) * mm, "end": v(-14.12, -9) * mm});
            skArc(sketch, "E410.2.132", {"start": v(-15.4, -10.71) * mm, "mid": v(-15.45, -10.66) * mm, "end": v(-15.49, -10.6) * mm});
            skArc(sketch, "E410.2.133", {"start": v(-14.53, -9.87) * mm, "mid": v(-14.47, -9.9) * mm, "end": v(-14.41, -9.91) * mm});
            skArc(sketch, "E410.2.134", {"start": v(-11.72, -16.99) * mm, "mid": v(-11.7, -16.96) * mm, "end": v(-11.7, -16.93) * mm});
            skArc(sketch, "E410.2.135", {"start": v(-13.9, -12.03) * mm, "mid": v(-13.93, -12.12) * mm, "end": v(-13.97, -12.2) * mm});
            skArc(sketch, "E410.2.136", {"start": v(-16.9, -17.08) * mm, "mid": v(-16.89, -17.1) * mm, "end": v(-16.88, -17.11) * mm});
            skArc(sketch, "E410.2.137", {"start": v(-14.84, -20.22) * mm, "mid": v(-14.83, -20.2) * mm, "end": v(-14.81, -20.2) * mm});
            skArc(sketch, "E410.2.138", {"start": v(-14.84, -12) * mm, "mid": v(-14.88, -11.82) * mm, "end": v(-14.92, -11.65) * mm});
            skArc(sketch, "E410.2.139", {"start": v(-14.06, -12.3) * mm, "mid": v(-14.1, -12.35) * mm, "end": v(-14.14, -12.4) * mm});
            skArc(sketch, "E410.2.140", {"start": v(-14.92, -11.65) * mm, "mid": v(-14.94, -11.57) * mm, "end": v(-14.97, -11.5) * mm});
            skArc(sketch, "E410.2.141", {"start": v(-14.13, -10.1) * mm, "mid": v(-14.07, -10.16) * mm, "end": v(-14.02, -10.23) * mm});
            skArc(sketch, "E410.2.142", {"start": v(-14.4, -12.7) * mm, "mid": v(-14.43, -12.74) * mm, "end": v(-14.46, -12.77) * mm});
            skArc(sketch, "E410.2.143", {"start": v(-12.49, -11.75) * mm, "mid": v(-12.6, -11.63) * mm, "end": v(-12.7, -11.51) * mm});
            skArc(sketch, "E410.2.144", {"start": v(-13.97, -10.32) * mm, "mid": v(-13.96, -10.34) * mm, "end": v(-13.95, -10.36) * mm});
            skArc(sketch, "E410.2.145", {"start": v(-13.7, -9.1) * mm, "mid": v(-13.72, -9.07) * mm, "end": v(-13.74, -9.04) * mm});
            skArc(sketch, "E410.2.146", {"start": v(-15.99, -13.52) * mm, "mid": v(-16.13, -13.34) * mm, "end": v(-16.28, -13.15) * mm});
            skArc(sketch, "E410.2.147", {"start": v(-15.62, -12.1) * mm, "mid": v(-15.61, -12.15) * mm, "end": v(-15.6, -12.2) * mm});
            skArc(sketch, "E410.2.148", {"start": v(-13.92, -10.45) * mm, "mid": v(-13.87, -10.6) * mm, "end": v(-13.84, -10.74) * mm});
            skArc(sketch, "E410.2.149", {"start": v(-14.83, -9.62) * mm, "mid": v(-14.84, -9.63) * mm, "end": v(-14.85, -9.64) * mm});
            skArc(sketch, "E410.2.150", {"start": v(-15.6, -12.2) * mm, "mid": v(-15.6, -12.35) * mm, "end": v(-15.62, -12.5) * mm});
            skArc(sketch, "E410.2.151", {"start": v(-15.07, -11.3) * mm, "mid": v(-15.09, -11.27) * mm, "end": v(-15.1, -11.25) * mm});
            skArc(sketch, "E410.2.152", {"start": v(-13.84, -11.19) * mm, "mid": v(-13.87, -11.3) * mm, "end": v(-13.9, -11.4) * mm});
            skArc(sketch, "E410.2.153", {"start": v(-14.64, -12.69) * mm, "mid": v(-14.65, -12.66) * mm, "end": v(-14.67, -12.64) * mm});
            skArc(sketch, "E410.2.154", {"start": v(-13.9, -11.4) * mm, "mid": v(-13.91, -11.46) * mm, "end": v(-13.93, -11.52) * mm});
            skArc(sketch, "E410.2.155", {"start": v(-15.22, -11.02) * mm, "mid": v(-15.25, -10.96) * mm, "end": v(-15.27, -10.91) * mm});
            skArc(sketch, "E410.2.156", {"start": v(-14.02, -8.94) * mm, "mid": v(-14.05, -8.95) * mm, "end": v(-14.08, -8.96) * mm});
            skArc(sketch, "E410.2.157", {"start": v(-15.32, -10.84) * mm, "mid": v(-15.37, -10.78) * mm, "end": v(-15.4, -10.71) * mm});
            skArc(sketch, "E410.2.158", {"start": v(-13.92, -11.78) * mm, "mid": v(-13.91, -11.86) * mm, "end": v(-13.9, -11.94) * mm});
            skArc(sketch, "E410.2.159", {"start": v(-14.6, -9.84) * mm, "mid": v(-14.56, -9.85) * mm, "end": v(-14.53, -9.87) * mm});
            skArc(sketch, "E410.2.160", {"start": v(-15.81, -13.38) * mm, "mid": v(-15.8, -13.46) * mm, "end": v(-15.79, -13.53) * mm});
            skArc(sketch, "E410.2.161", {"start": v(-13.9, -11.94) * mm, "mid": v(-13.9, -11.98) * mm, "end": v(-13.9, -12.03) * mm});
            skArc(sketch, "E410.2.162", {"start": v(-14.8, -12.28) * mm, "mid": v(-14.82, -12.14) * mm, "end": v(-14.84, -12) * mm});
            skArc(sketch, "E410.2.163", {"start": v(-13.97, -12.2) * mm, "mid": v(-14.01, -12.25) * mm, "end": v(-14.06, -12.3) * mm});
            skArc(sketch, "E410.2.164", {"start": v(-14.85, -20.25) * mm, "mid": v(-14.85, -20.23) * mm, "end": v(-14.84, -20.22) * mm});
            skArc(sketch, "E410.2.165", {"start": v(-14.21, -10.02) * mm, "mid": v(-14.17, -10.05) * mm, "end": v(-14.13, -10.1) * mm});
            skArc(sketch, "E410.2.166", {"start": v(-15.82, -10.52) * mm, "mid": v(-15.95, -10.59) * mm, "end": v(-16.08, -10.67) * mm});
            skArc(sketch, "E410.2.167", {"start": v(-14.18, -12.44) * mm, "mid": v(-14.3, -12.58) * mm, "end": v(-14.4, -12.7) * mm});
            skArc(sketch, "E410.2.168", {"start": v(-18.06, -13.53) * mm, "mid": v(-18.01, -13.61) * mm, "end": v(-17.98, -13.7) * mm});
            skArc(sketch, "E410.2.169", {"start": v(-16.23, -10.78) * mm, "mid": v(-16.32, -10.85) * mm, "end": v(-16.4, -10.93) * mm});
            skArc(sketch, "E410.2.170", {"start": v(-13.98, -10.28) * mm, "mid": v(-13.98, -10.3) * mm, "end": v(-13.97, -10.32) * mm});
            skArc(sketch, "E410.2.171", {"start": v(-15.8, -11.71) * mm, "mid": v(-15.72, -11.85) * mm, "end": v(-15.66, -12) * mm});
            skArc(sketch, "E410.2.172", {"start": v(-17.98, -13.7) * mm, "mid": v(-17.94, -13.78) * mm, "end": v(-17.92, -13.88) * mm});
            skArc(sketch, "E410.2.173", {"start": v(-13.68, -9.15) * mm, "mid": v(-13.7, -9.12) * mm, "end": v(-13.7, -9.1) * mm});
            skArc(sketch, "E410.2.174", {"start": v(-16.4, -10.93) * mm, "mid": v(-16.47, -11) * mm, "end": v(-16.53, -11.08) * mm});
            skArc(sketch, "E410.2.175", {"start": v(-15.92, -13.6) * mm, "mid": v(-15.95, -13.56) * mm, "end": v(-15.99, -13.52) * mm});
            skArc(sketch, "E410.2.176", {"start": v(-15.66, -12) * mm, "mid": v(-15.64, -12.05) * mm, "end": v(-15.62, -12.1) * mm});
            skArc(sketch, "E410.2.177", {"start": v(-17.92, -13.88) * mm, "mid": v(-17.9, -13.97) * mm, "end": v(-17.87, -14.06) * mm});
            skArc(sketch, "E410.2.178", {"start": v(-14.81, -9.6) * mm, "mid": v(-14.82, -9.6) * mm, "end": v(-14.83, -9.62) * mm});
            skArc(sketch, "E410.2.179", {"start": v(-15.05, -11.34) * mm, "mid": v(-15.06, -11.32) * mm, "end": v(-15.07, -11.3) * mm});
            skArc(sketch, "E410.2.180", {"start": v(-17.87, -14.06) * mm, "mid": v(-17.85, -14.16) * mm, "end": v(-17.82, -14.25) * mm});
            skArc(sketch, "E410.2.181", {"start": v(-16.28, -13.15) * mm, "mid": v(-16.4, -12.99) * mm, "end": v(-16.53, -12.82) * mm});
            skArc(sketch, "E410.2.182", {"start": v(-16.53, -12.82) * mm, "mid": v(-16.59, -12.73) * mm, "end": v(-16.64, -12.64) * mm});
            skArc(sketch, "E410.2.183", {"start": v(-14.6, -12.73) * mm, "mid": v(-14.62, -12.7) * mm, "end": v(-14.64, -12.69) * mm});
            skArc(sketch, "E410.2.184", {"start": v(-15.69, -12.78) * mm, "mid": v(-15.73, -12.89) * mm, "end": v(-15.77, -13) * mm});
            skArc(sketch, "E410.2.185", {"start": v(-15.13, -11.21) * mm, "mid": v(-15.18, -11.12) * mm, "end": v(-15.22, -11.02) * mm});
            skArc(sketch, "E410.2.186", {"start": v(-15.77, -13) * mm, "mid": v(-15.79, -13.05) * mm, "end": v(-15.8, -13.1) * mm});
            skArc(sketch, "E410.2.187", {"start": v(-16.53, -11.25) * mm, "mid": v(-16.46, -11.3) * mm, "end": v(-16.39, -11.34) * mm});
            skArc(sketch, "E410.2.188", {"start": v(-13.96, -8.95) * mm, "mid": v(-13.99, -8.94) * mm, "end": v(-14.02, -8.94) * mm});
            skArc(sketch, "E410.2.189", {"start": v(-13.93, -11.66) * mm, "mid": v(-13.93, -11.72) * mm, "end": v(-13.92, -11.78) * mm});
            skArc(sketch, "E410.2.190", {"start": v(-14.65, -9.83) * mm, "mid": v(-14.62, -9.83) * mm, "end": v(-14.6, -9.84) * mm});
            skArc(sketch, "E410.2.191", {"start": v(-16.93, -12.16) * mm, "mid": v(-16.99, -12.08) * mm, "end": v(-17.05, -12) * mm});
            skArc(sketch, "E410.2.192", {"start": v(-15.82, -13.2) * mm, "mid": v(-15.82, -13.29) * mm, "end": v(-15.81, -13.38) * mm});
            skArc(sketch, "E410.2.193", {"start": v(-14.78, -12.39) * mm, "mid": v(-14.79, -12.33) * mm, "end": v(-14.8, -12.28) * mm});
            skArc(sketch, "E410.2.194", {"start": v(-17.19, -11.77) * mm, "mid": v(-17.2, -11.72) * mm, "end": v(-17.22, -11.66) * mm});
            skArc(sketch, "E410.2.195", {"start": v(-14.85, -20.33) * mm, "mid": v(-14.85, -20.29) * mm, "end": v(-14.85, -20.25) * mm});
            skArc(sketch, "E410.2.196", {"start": v(-14.32, -9.95) * mm, "mid": v(-14.26, -9.98) * mm, "end": v(-14.21, -10.02) * mm});
            skArc(sketch, "E410.2.197", {"start": v(-16.04, -11.47) * mm, "mid": v(-16.01, -11.49) * mm, "end": v(-15.99, -11.5) * mm});
            skArc(sketch, "E410.2.198", {"start": v(-15.72, -10.48) * mm, "mid": v(-15.77, -10.5) * mm, "end": v(-15.82, -10.52) * mm});
            skArc(sketch, "E410.2.199", {"start": v(-18.22, -13.3) * mm, "mid": v(-18.14, -13.41) * mm, "end": v(-18.06, -13.53) * mm});
            skArc(sketch, "E410.2.200", {"start": v(-14.14, -12.4) * mm, "mid": v(-14.16, -12.42) * mm, "end": v(-14.18, -12.44) * mm});
            skArc(sketch, "E410.2.201", {"start": v(-16.08, -10.67) * mm, "mid": v(-16.15, -10.72) * mm, "end": v(-16.23, -10.78) * mm});
            skArc(sketch, "E410.2.202", {"start": v(-15.87, -11.62) * mm, "mid": v(-15.83, -11.67) * mm, "end": v(-15.8, -11.71) * mm});
            skArc(sketch, "E410.2.203", {"start": v(-13.66, -9.21) * mm, "mid": v(-13.67, -9.18) * mm, "end": v(-13.68, -9.15) * mm});
            skArc(sketch, "E410.2.204", {"start": v(-15.84, -13.7) * mm, "mid": v(-15.88, -13.65) * mm, "end": v(-15.92, -13.6) * mm});
            skArc(sketch, "E410.2.205", {"start": v(-14.77, -9.51) * mm, "mid": v(-14.8, -9.56) * mm, "end": v(-14.81, -9.6) * mm});
            skArc(sketch, "E410.2.206", {"start": v(-15.02, -11.4) * mm, "mid": v(-15.03, -11.37) * mm, "end": v(-15.05, -11.34) * mm});
            skArc(sketch, "E410.2.207", {"start": v(-14.56, -12.79) * mm, "mid": v(-14.59, -12.76) * mm, "end": v(-14.6, -12.73) * mm});
            skArc(sketch, "E410.2.208", {"start": v(-15.62, -12.5) * mm, "mid": v(-15.65, -12.64) * mm, "end": v(-15.69, -12.78) * mm});
            skArc(sketch, "E410.2.209", {"start": v(-15.1, -11.25) * mm, "mid": v(-15.12, -11.23) * mm, "end": v(-15.13, -11.21) * mm});
            skArc(sketch, "E410.2.210", {"start": v(-16.56, -11.2) * mm, "mid": v(-16.55, -11.23) * mm, "end": v(-16.53, -11.25) * mm});
            skArc(sketch, "E410.2.211", {"start": v(-16.7, -12.53) * mm, "mid": v(-16.75, -12.42) * mm, "end": v(-16.8, -12.32) * mm});
            skArc(sketch, "E410.2.212", {"start": v(-13.93, -11.52) * mm, "mid": v(-13.93, -11.59) * mm, "end": v(-13.93, -11.66) * mm});
            skArc(sketch, "E410.2.213", {"start": v(-14.75, -9.79) * mm, "mid": v(-14.7, -9.82) * mm, "end": v(-14.65, -9.83) * mm});
            skArc(sketch, "E410.2.214", {"start": v(-16.8, -12.32) * mm, "mid": v(-16.86, -12.24) * mm, "end": v(-16.93, -12.16) * mm});
            skArc(sketch, "E410.2.215", {"start": v(-15.8, -13.1) * mm, "mid": v(-15.81, -13.15) * mm, "end": v(-15.82, -13.2) * mm});
            skArc(sketch, "E410.2.216", {"start": v(-16.39, -11.34) * mm, "mid": v(-16.35, -11.36) * mm, "end": v(-16.3, -11.36) * mm});
            skArc(sketch, "E410.2.217", {"start": v(-15.27, -10.91) * mm, "mid": v(-15.3, -10.88) * mm, "end": v(-15.32, -10.84) * mm});
            skArc(sketch, "E410.2.218", {"start": v(-20.49, -17.18) * mm, "mid": v(-20.16, -17.34) * mm, "end": v(-19.84, -17.5) * mm});
            skArc(sketch, "E410.2.219", {"start": v(-16.1, -11.45) * mm, "mid": v(-16.07, -11.46) * mm, "end": v(-16.04, -11.47) * mm});
            skArc(sketch, "E410.2.220", {"start": v(-20.42, -16.9) * mm, "mid": v(-20.52, -16.86) * mm, "end": v(-20.61, -16.83) * mm});
            skArc(sketch, "E410.2.221", {"start": v(-15.67, -10.48) * mm, "mid": v(-15.7, -10.48) * mm, "end": v(-15.72, -10.48) * mm});
            skArc(sketch, "E410.2.222", {"start": v(-18.56, -16.43) * mm, "mid": v(-18.77, -16.28) * mm, "end": v(-19, -16.14) * mm});
            skArc(sketch, "E410.2.223", {"start": v(-19.64, -17.72) * mm, "mid": v(-19.64, -17.75) * mm, "end": v(-19.63, -17.78) * mm});
            skArc(sketch, "E410.2.224", {"start": v(-19.63, -17.78) * mm, "mid": v(-19.58, -17.9) * mm, "end": v(-19.54, -18.02) * mm});
            skArc(sketch, "E410.2.225", {"start": v(-19.05, -16.11) * mm, "mid": v(-19.08, -16.1) * mm, "end": v(-19.1, -16.09) * mm});
            skArc(sketch, "E410.2.226", {"start": v(-19.54, -18.02) * mm, "mid": v(-19.46, -18.2) * mm, "end": v(-19.38, -18.38) * mm});
            skArc(sketch, "E410.2.227", {"start": v(-21.03, -16.73) * mm, "mid": v(-21.14, -16.73) * mm, "end": v(-21.25, -16.74) * mm});
            skArc(sketch, "E410.2.228", {"start": v(-15.94, -11.54) * mm, "mid": v(-15.9, -11.58) * mm, "end": v(-15.87, -11.62) * mm});
            skArc(sketch, "E410.2.229", {"start": v(-15.81, -13.71) * mm, "mid": v(-15.83, -13.7) * mm, "end": v(-15.84, -13.7) * mm});
            skArc(sketch, "E410.2.230", {"start": v(-14.72, -9.46) * mm, "mid": v(-14.75, -9.48) * mm, "end": v(-14.77, -9.51) * mm});
            skArc(sketch, "E410.2.231", {"start": v(-15, -11.45) * mm, "mid": v(-15.01, -11.43) * mm, "end": v(-15.02, -11.4) * mm});
            skArc(sketch, "E410.2.232", {"start": v(-20.14, -16.75) * mm, "mid": v(-20.08, -16.82) * mm, "end": v(-20.03, -16.9) * mm});
            skArc(sketch, "E410.2.233", {"start": v(-14.53, -12.8) * mm, "mid": v(-14.55, -12.8) * mm, "end": v(-14.56, -12.79) * mm});
            skArc(sketch, "E410.2.234", {"start": v(-19.4, -15.87) * mm, "mid": v(-19.54, -15.77) * mm, "end": v(-19.69, -15.68) * mm});
            skArc(sketch, "E410.2.235", {"start": v(-16.57, -11.17) * mm, "mid": v(-16.57, -11.19) * mm, "end": v(-16.56, -11.2) * mm});
            skArc(sketch, "E410.2.236", {"start": v(-19.69, -15.68) * mm, "mid": v(-19.95, -15.53) * mm, "end": v(-20.23, -15.4) * mm});
            skArc(sketch, "E410.2.237", {"start": v(-21.37, -16.87) * mm, "mid": v(-21.34, -16.88) * mm, "end": v(-21.31, -16.88) * mm});
            skArc(sketch, "E410.2.238", {"start": v(-16.64, -12.64) * mm, "mid": v(-16.67, -12.59) * mm, "end": v(-16.7, -12.53) * mm});
            skArc(sketch, "E410.2.239", {"start": v(-21.2, -16.9) * mm, "mid": v(-20.98, -16.98) * mm, "end": v(-20.78, -17.05) * mm});
            skArc(sketch, "E410.2.240", {"start": v(-19.97, -17.01) * mm, "mid": v(-19.98, -17.02) * mm, "end": v(-19.98, -17.02) * mm});
            skArc(sketch, "E410.2.241", {"start": v(-20.78, -17.05) * mm, "mid": v(-20.63, -17.11) * mm, "end": v(-20.49, -17.18) * mm});
            skArc(sketch, "E410.2.242", {"start": v(-16.16, -11.42) * mm, "mid": v(-16.13, -11.44) * mm, "end": v(-16.1, -11.45) * mm});
            skArc(sketch, "E410.2.243", {"start": v(-20.2, -16.96) * mm, "mid": v(-20.31, -16.93) * mm, "end": v(-20.42, -16.9) * mm});
            skArc(sketch, "E410.2.244", {"start": v(-15.61, -10.5) * mm, "mid": v(-15.64, -10.5) * mm, "end": v(-15.67, -10.48) * mm});
            skArc(sketch, "E410.2.245", {"start": v(-19.66, -17.66) * mm, "mid": v(-19.65, -17.69) * mm, "end": v(-19.64, -17.72) * mm});
            skArc(sketch, "E410.2.246", {"start": v(-15.99, -11.5) * mm, "mid": v(-15.96, -11.52) * mm, "end": v(-15.94, -11.54) * mm});
            skArc(sketch, "E410.2.247", {"start": v(-19, -16.14) * mm, "mid": v(-19.02, -16.12) * mm, "end": v(-19.05, -16.11) * mm});
            skArc(sketch, "E410.2.248", {"start": v(-20.61, -16.4) * mm, "mid": v(-20.57, -16.43) * mm, "end": v(-20.52, -16.46) * mm});
            skArc(sketch, "E410.2.249", {"start": v(-15.78, -13.73) * mm, "mid": v(-15.8, -13.73) * mm, "end": v(-15.81, -13.71) * mm});
            skArc(sketch, "E410.2.250", {"start": v(-14.64, -9.38) * mm, "mid": v(-14.68, -9.42) * mm, "end": v(-14.72, -9.46) * mm});
            skArc(sketch, "E410.2.251", {"start": v(-14.97, -11.5) * mm, "mid": v(-14.99, -11.48) * mm, "end": v(-15, -11.45) * mm});
            skArc(sketch, "E410.2.252", {"start": v(-20.23, -16.64) * mm, "mid": v(-20.18, -16.7) * mm, "end": v(-20.14, -16.75) * mm});
            skArc(sketch, "E410.2.253", {"start": v(-14.5, -12.8) * mm, "mid": v(-14.51, -12.8) * mm, "end": v(-14.53, -12.8) * mm});
            skArc(sketch, "E410.2.254", {"start": v(-19.24, -16) * mm, "mid": v(-19.32, -15.93) * mm, "end": v(-19.4, -15.87) * mm});
            skArc(sketch, "E410.2.255", {"start": v(-16.56, -11.14) * mm, "mid": v(-16.57, -11.15) * mm, "end": v(-16.57, -11.17) * mm});
            skArc(sketch, "E410.2.256", {"start": v(-21.4, -16.85) * mm, "mid": v(-21.39, -16.86) * mm, "end": v(-21.37, -16.87) * mm});
            skArc(sketch, "E410.2.257", {"start": v(-21.31, -16.88) * mm, "mid": v(-21.25, -16.9) * mm, "end": v(-21.2, -16.9) * mm});
            skArc(sketch, "E410.2.258", {"start": v(-19.97, -17) * mm, "mid": v(-19.97, -17) * mm, "end": v(-19.97, -17.01) * mm});
            skArc(sketch, "E410.2.259", {"start": v(-20.1, -17) * mm, "mid": v(-20.15, -16.97) * mm, "end": v(-20.2, -16.96) * mm});
            skArc(sketch, "E410.2.260", {"start": v(-16.22, -11.39) * mm, "mid": v(-16.2, -11.4) * mm, "end": v(-16.16, -11.42) * mm});
            skArc(sketch, "E410.2.261", {"start": v(-15.49, -10.6) * mm, "mid": v(-15.54, -10.54) * mm, "end": v(-15.61, -10.5) * mm});
            skArc(sketch, "E410.2.262", {"start": v(-19.73, -17.57) * mm, "mid": v(-19.7, -17.6) * mm, "end": v(-19.66, -17.66) * mm});
            skArc(sketch, "E410.2.263", {"start": v(-20.61, -16.83) * mm, "mid": v(-20.71, -16.8) * mm, "end": v(-20.81, -16.77) * mm});
            skArc(sketch, "E410.2.264", {"start": v(-15.75, -13.72) * mm, "mid": v(-15.76, -13.73) * mm, "end": v(-15.78, -13.73) * mm});
            skArc(sketch, "E410.2.265", {"start": v(-20.81, -16.77) * mm, "mid": v(-20.92, -16.74) * mm, "end": v(-21.03, -16.73) * mm});
            skArc(sketch, "E410.2.266", {"start": v(-14.56, -9.3) * mm, "mid": v(-14.6, -9.34) * mm, "end": v(-14.64, -9.38) * mm});
            skArc(sketch, "E410.2.267", {"start": v(-20.33, -16.58) * mm, "mid": v(-20.28, -16.6) * mm, "end": v(-20.23, -16.64) * mm});
            skArc(sketch, "E410.2.268", {"start": v(-14.46, -12.77) * mm, "mid": v(-14.48, -12.79) * mm, "end": v(-14.5, -12.8) * mm});
            skArc(sketch, "E410.2.269", {"start": v(-19.2, -16.03) * mm, "mid": v(-19.22, -16.02) * mm, "end": v(-19.24, -16) * mm});
            skArc(sketch, "E410.2.270", {"start": v(-16.53, -11.08) * mm, "mid": v(-16.55, -11.1) * mm, "end": v(-16.56, -11.14) * mm});
            skArc(sketch, "E410.2.271", {"start": v(-21.42, -16.83) * mm, "mid": v(-21.41, -16.84) * mm, "end": v(-21.4, -16.85) * mm});
            skArc(sketch, "E410.2.272", {"start": v(-19.98, -16.97) * mm, "mid": v(-19.98, -16.98) * mm, "end": v(-19.97, -17) * mm});
            skArc(sketch, "E410.2.273", {"start": v(-20, -17.02) * mm, "mid": v(-20.05, -17) * mm, "end": v(-20.1, -17) * mm});
            skArc(sketch, "E410.2.274", {"start": v(-16.3, -11.36) * mm, "mid": v(-16.26, -11.37) * mm, "end": v(-16.22, -11.39) * mm});
            skArc(sketch, "E410.2.275", {"start": v(-19.84, -17.5) * mm, "mid": v(-19.79, -17.54) * mm, "end": v(-19.73, -17.57) * mm});
            skArc(sketch, "E410.2.276", {"start": v(-14.78, -12.48) * mm, "mid": v(-14.78, -12.43) * mm, "end": v(-14.78, -12.39) * mm});
            skArc(sketch, "E410.2.277", {"start": v(-15.74, -13.67) * mm, "mid": v(-15.74, -13.7) * mm, "end": v(-15.75, -13.72) * mm});
            skArc(sketch, "E410.2.278", {"start": v(-20.7, -16.34) * mm, "mid": v(-20.66, -16.37) * mm, "end": v(-20.61, -16.4) * mm});
            skArc(sketch, "E410.2.279", {"start": v(-20.52, -16.46) * mm, "mid": v(-20.43, -16.52) * mm, "end": v(-20.33, -16.58) * mm});
            skArc(sketch, "E410.2.280", {"start": v(-19.15, -16.07) * mm, "mid": v(-19.18, -16.05) * mm, "end": v(-19.2, -16.03) * mm});
            skArc(sketch, "E410.2.281", {"start": v(-21.4, -16.8) * mm, "mid": v(-21.41, -16.82) * mm, "end": v(-21.42, -16.83) * mm});
            skArc(sketch, "E410.2.282", {"start": v(-20.03, -16.9) * mm, "mid": v(-20, -16.93) * mm, "end": v(-19.98, -16.97) * mm});
            skArc(sketch, "E410.2.283", {"start": v(-19.98, -17.02) * mm, "mid": v(-20, -17.02) * mm, "end": v(-20, -17.02) * mm});
            skArc(sketch, "E410.2.284", {"start": v(-14.77, -12.52) * mm, "mid": v(-14.77, -12.5) * mm, "end": v(-14.78, -12.48) * mm});
            skArc(sketch, "E410.2.285", {"start": v(-15.76, -13.63) * mm, "mid": v(-15.75, -13.65) * mm, "end": v(-15.74, -13.67) * mm});
            skArc(sketch, "E410.2.286", {"start": v(-19.1, -16.09) * mm, "mid": v(-19.13, -16.08) * mm, "end": v(-19.15, -16.07) * mm});
            skArc(sketch, "E410.2.287", {"start": v(-21.37, -16.78) * mm, "mid": v(-21.4, -16.79) * mm, "end": v(-21.4, -16.8) * mm});
            skArc(sketch, "E410.2.288", {"start": v(-14.73, -12.57) * mm, "mid": v(-14.75, -12.55) * mm, "end": v(-14.77, -12.52) * mm});
            skArc(sketch, "E410.2.289", {"start": v(-18.66, -12.84) * mm, "mid": v(-18.59, -12.87) * mm, "end": v(-18.53, -12.9) * mm});
            skArc(sketch, "E410.2.290", {"start": v(-17.12, -11.91) * mm, "mid": v(-17.16, -11.84) * mm, "end": v(-17.19, -11.77) * mm});
            skArc(sketch, "E410.2.291", {"start": v(-15.79, -13.53) * mm, "mid": v(-15.78, -13.58) * mm, "end": v(-15.76, -13.63) * mm});
            skArc(sketch, "E410.2.292", {"start": v(-18.16, -11.16) * mm, "mid": v(-18.3, -11.27) * mm, "end": v(-18.46, -11.39) * mm});
            skArc(sketch, "E410.2.293", {"start": v(-19.17, -12.3) * mm, "mid": v(-19.21, -12.34) * mm, "end": v(-19.25, -12.39) * mm});
            skArc(sketch, "E410.2.294", {"start": v(-18.46, -11.39) * mm, "mid": v(-18.56, -11.48) * mm, "end": v(-18.66, -11.58) * mm});
            skArc(sketch, "E410.2.295", {"start": v(-18.34, -13.13) * mm, "mid": v(-18.28, -13.21) * mm, "end": v(-18.22, -13.3) * mm});
            skArc(sketch, "E410.2.296", {"start": v(-17.3, -11.46) * mm, "mid": v(-17.33, -11.42) * mm, "end": v(-17.35, -11.37) * mm});
            skArc(sketch, "E410.2.297", {"start": v(-21.25, -16.74) * mm, "mid": v(-21.31, -16.75) * mm, "end": v(-21.37, -16.78) * mm});
            skArc(sketch, "E410.2.298", {"start": v(-17.37, -11.3) * mm, "mid": v(-17.38, -11.22) * mm, "end": v(-17.4, -11.15) * mm});
            skArc(sketch, "E410.2.299", {"start": v(-18.78, -11.78) * mm, "mid": v(-18.8, -11.79) * mm, "end": v(-18.8, -11.8) * mm});
            skArc(sketch, "E410.2.300", {"start": v(-17.52, -10.96) * mm, "mid": v(-17.55, -10.95) * mm, "end": v(-17.58, -10.93) * mm});
            skArc(sketch, "E410.2.301", {"start": v(-19.12, -12.77) * mm, "mid": v(-19.07, -12.79) * mm, "end": v(-19.02, -12.8) * mm});
            skArc(sketch, "E410.2.302", {"start": v(-18.97, -12.8) * mm, "mid": v(-18.92, -12.79) * mm, "end": v(-18.88, -12.79) * mm});
            skArc(sketch, "E410.2.303", {"start": v(-18.74, -11.9) * mm, "mid": v(-18.74, -11.9) * mm, "end": v(-18.75, -11.91) * mm});
            skArc(sketch, "E410.2.304", {"start": v(-17.7, -10.93) * mm, "mid": v(-17.74, -10.93) * mm, "end": v(-17.78, -10.93) * mm});
            skArc(sketch, "E410.2.305", {"start": v(-14.67, -12.64) * mm, "mid": v(-14.7, -12.6) * mm, "end": v(-14.73, -12.57) * mm});
            skArc(sketch, "E410.2.306", {"start": v(-21.38, -16.11) * mm, "mid": v(-21.3, -16.14) * mm, "end": v(-21.22, -16.16) * mm});
            skArc(sketch, "E410.2.307", {"start": v(-18.77, -12.8) * mm, "mid": v(-18.71, -12.82) * mm, "end": v(-18.66, -12.84) * mm});
            skArc(sketch, "E410.2.308", {"start": v(-17.05, -12) * mm, "mid": v(-17.08, -11.96) * mm, "end": v(-17.12, -11.91) * mm});
            skArc(sketch, "E410.2.309", {"start": v(-18.08, -11.1) * mm, "mid": v(-18.12, -11.13) * mm, "end": v(-18.16, -11.16) * mm});
            skArc(sketch, "E410.2.310", {"start": v(-19.07, -12.2) * mm, "mid": v(-19.12, -12.25) * mm, "end": v(-19.17, -12.3) * mm});
            skArc(sketch, "E410.2.311", {"start": v(-18.4, -13.05) * mm, "mid": v(-18.37, -13.1) * mm, "end": v(-18.34, -13.13) * mm});
            skArc(sketch, "E410.2.312", {"start": v(-17.35, -11.37) * mm, "mid": v(-17.36, -11.33) * mm, "end": v(-17.37, -11.3) * mm});
            skArc(sketch, "E410.2.313", {"start": v(-18.75, -11.75) * mm, "mid": v(-18.77, -11.77) * mm, "end": v(-18.78, -11.78) * mm});
            skArc(sketch, "E410.2.314", {"start": v(-17.43, -11.07) * mm, "mid": v(-17.46, -11) * mm, "end": v(-17.52, -10.96) * mm});
            skArc(sketch, "E410.2.315", {"start": v(-19.2, -12.73) * mm, "mid": v(-19.16, -12.75) * mm, "end": v(-19.12, -12.77) * mm});
            skArc(sketch, "E410.2.316", {"start": v(-19.02, -12.8) * mm, "mid": v(-19, -12.8) * mm, "end": v(-18.97, -12.8) * mm});
            skArc(sketch, "E410.2.317", {"start": v(-18.75, -11.87) * mm, "mid": v(-18.74, -11.88) * mm, "end": v(-18.74, -11.9) * mm});
            skArc(sketch, "E410.2.318", {"start": v(-17.63, -10.92) * mm, "mid": v(-17.67, -10.92) * mm, "end": v(-17.7, -10.93) * mm});
            skArc(sketch, "E410.2.319", {"start": v(-18.88, -12.79) * mm, "mid": v(-18.83, -12.8) * mm, "end": v(-18.77, -12.8) * mm});
            skArc(sketch, "E410.2.320", {"start": v(-18, -11.01) * mm, "mid": v(-18.04, -11.06) * mm, "end": v(-18.08, -11.1) * mm});
            skArc(sketch, "E410.2.321", {"start": v(-18.98, -12.1) * mm, "mid": v(-19.02, -12.15) * mm, "end": v(-19.07, -12.2) * mm});
            skArc(sketch, "E410.2.322", {"start": v(-18.47, -12.97) * mm, "mid": v(-18.43, -13.01) * mm, "end": v(-18.4, -13.05) * mm});
            skArc(sketch, "E410.2.323", {"start": v(-17.27, -11.55) * mm, "mid": v(-17.29, -11.5) * mm, "end": v(-17.3, -11.46) * mm});
            skArc(sketch, "E410.2.324", {"start": v(-18.74, -11.72) * mm, "mid": v(-18.75, -11.74) * mm, "end": v(-18.75, -11.75) * mm});
            skArc(sketch, "E410.2.325", {"start": v(-17.4, -11.15) * mm, "mid": v(-17.4, -11.1) * mm, "end": v(-17.43, -11.07) * mm});
            skArc(sketch, "E410.2.326", {"start": v(-19.29, -12.66) * mm, "mid": v(-19.25, -12.7) * mm, "end": v(-19.2, -12.73) * mm});
            skArc(sketch, "E410.2.327", {"start": v(-18.77, -11.84) * mm, "mid": v(-18.76, -11.86) * mm, "end": v(-18.75, -11.87) * mm});
            skArc(sketch, "E410.2.328", {"start": v(-17.58, -10.93) * mm, "mid": v(-17.6, -10.93) * mm, "end": v(-17.63, -10.92) * mm});
            skArc(sketch, "E410.2.329", {"start": v(-17.95, -10.97) * mm, "mid": v(-17.97, -11) * mm, "end": v(-18, -11.01) * mm});
            skArc(sketch, "E410.2.330", {"start": v(-18.53, -12.9) * mm, "mid": v(-18.5, -12.94) * mm, "end": v(-18.47, -12.97) * mm});
            skArc(sketch, "E410.2.331", {"start": v(-17.22, -11.66) * mm, "mid": v(-17.24, -11.6) * mm, "end": v(-17.27, -11.55) * mm});
            skArc(sketch, "E410.2.332", {"start": v(-18.72, -11.65) * mm, "mid": v(-18.73, -11.69) * mm, "end": v(-18.74, -11.72) * mm});
            skArc(sketch, "E410.2.333", {"start": v(-19.32, -12.63) * mm, "mid": v(-19.3, -12.65) * mm, "end": v(-19.29, -12.66) * mm});
            skArc(sketch, "E410.2.334", {"start": v(-18.8, -11.8) * mm, "mid": v(-18.79, -11.83) * mm, "end": v(-18.77, -11.84) * mm});
            skArc(sketch, "E410.2.335", {"start": v(-17.86, -10.93) * mm, "mid": v(-17.9, -10.95) * mm, "end": v(-17.95, -10.97) * mm});
            skArc(sketch, "E410.2.336", {"start": v(-18.87, -11.99) * mm, "mid": v(-18.93, -12.04) * mm, "end": v(-18.98, -12.1) * mm});
            skArc(sketch, "E410.2.337", {"start": v(-18.66, -11.58) * mm, "mid": v(-18.7, -11.62) * mm, "end": v(-18.72, -11.65) * mm});
            skArc(sketch, "E410.2.338", {"start": v(-19.33, -12.58) * mm, "mid": v(-19.33, -12.6) * mm, "end": v(-19.32, -12.63) * mm});
            skArc(sketch, "E410.2.339", {"start": v(-17.78, -10.93) * mm, "mid": v(-17.82, -10.93) * mm, "end": v(-17.86, -10.93) * mm});
            skArc(sketch, "E410.2.340", {"start": v(-18.77, -11.93) * mm, "mid": v(-18.82, -11.95) * mm, "end": v(-18.87, -11.99) * mm});
            skArc(sketch, "E410.2.341", {"start": v(-19.32, -12.53) * mm, "mid": v(-19.33, -12.55) * mm, "end": v(-19.33, -12.58) * mm});
            skArc(sketch, "E410.2.342", {"start": v(-18.75, -11.91) * mm, "mid": v(-18.76, -11.92) * mm, "end": v(-18.77, -11.93) * mm});
            skArc(sketch, "E410.2.343", {"start": v(-19.29, -12.44) * mm, "mid": v(-19.3, -12.48) * mm, "end": v(-19.32, -12.53) * mm});
            skArc(sketch, "E410.2.344", {"start": v(-20.73, -15.27) * mm, "mid": v(-20.82, -15.27) * mm, "end": v(-20.91, -15.27) * mm});
            skArc(sketch, "E410.2.345", {"start": v(-22.03, -14.32) * mm, "mid": v(-22.06, -14.34) * mm, "end": v(-22.1, -14.37) * mm});
            skArc(sketch, "E410.2.346", {"start": v(-21.26, -14.67) * mm, "mid": v(-21.24, -14.59) * mm, "end": v(-21.25, -14.5) * mm});
            skArc(sketch, "E410.2.347", {"start": v(-20.84, -16.25) * mm, "mid": v(-20.77, -16.3) * mm, "end": v(-20.7, -16.34) * mm});
            skArc(sketch, "E410.2.348", {"start": v(-22.1, -14.37) * mm, "mid": v(-22.16, -14.41) * mm, "end": v(-22.22, -14.46) * mm});
            skArc(sketch, "E410.2.349", {"start": v(-19.25, -12.39) * mm, "mid": v(-19.27, -12.41) * mm, "end": v(-19.29, -12.44) * mm});
            skArc(sketch, "E410.2.350", {"start": v(-21.6, -15.02) * mm, "mid": v(-21.62, -15) * mm, "end": v(-21.64, -14.98) * mm});
            skArc(sketch, "E410.2.351", {"start": v(-22.43, -14.83) * mm, "mid": v(-22.44, -14.9) * mm, "end": v(-22.43, -14.96) * mm});
            skArc(sketch, "E410.2.352", {"start": v(-21.7, -14.84) * mm, "mid": v(-21.64, -14.83) * mm, "end": v(-21.57, -14.83) * mm});
            skArc(sketch, "E410.2.353", {"start": v(-22.43, -14.96) * mm, "mid": v(-22.4, -15.05) * mm, "end": v(-22.38, -15.15) * mm});
            skArc(sketch, "E410.2.354", {"start": v(-22.38, -15.15) * mm, "mid": v(-22.34, -15.26) * mm, "end": v(-22.3, -15.38) * mm});
            skArc(sketch, "E410.2.355", {"start": v(-22.3, -15.38) * mm, "mid": v(-22.2, -15.53) * mm, "end": v(-22.1, -15.66) * mm});
            skArc(sketch, "E410.2.356", {"start": v(-20.23, -15.4) * mm, "mid": v(-20.38, -15.34) * mm, "end": v(-20.53, -15.29) * mm});
            skArc(sketch, "E410.2.357", {"start": v(-21.5, -14.29) * mm, "mid": v(-21.53, -14.3) * mm, "end": v(-21.56, -14.3) * mm});
            skArc(sketch, "E410.2.358", {"start": v(-21.41, -14.84) * mm, "mid": v(-21.38, -14.83) * mm, "end": v(-21.35, -14.82) * mm});
            skArc(sketch, "E410.2.359", {"start": v(-20.53, -15.29) * mm, "mid": v(-20.63, -15.27) * mm, "end": v(-20.73, -15.27) * mm});
            skArc(sketch, "E410.2.360", {"start": v(-21.92, -15.81) * mm, "mid": v(-21.75, -15.93) * mm, "end": v(-21.57, -16.03) * mm});
            skArc(sketch, "E410.2.361", {"start": v(-21.22, -16.16) * mm, "mid": v(-21.15, -16.17) * mm, "end": v(-21.08, -16.18) * mm});
            skArc(sketch, "E410.2.362", {"start": v(-21.83, -14.29) * mm, "mid": v(-21.87, -14.29) * mm, "end": v(-21.92, -14.3) * mm});
            skArc(sketch, "E410.2.363", {"start": v(-21.1, -15.27) * mm, "mid": v(-21.15, -15.26) * mm, "end": v(-21.2, -15.26) * mm});
            skArc(sketch, "E410.2.364", {"start": v(-21.92, -14.3) * mm, "mid": v(-21.98, -14.3) * mm, "end": v(-22.03, -14.32) * mm});
            skArc(sketch, "E410.2.365", {"start": v(-21.2, -15.26) * mm, "mid": v(-21.27, -15.24) * mm, "end": v(-21.33, -15.22) * mm});
            skArc(sketch, "E410.2.366", {"start": v(-20.94, -16.2) * mm, "mid": v(-20.9, -16.23) * mm, "end": v(-20.84, -16.25) * mm});
            skArc(sketch, "E410.2.367", {"start": v(-21.56, -15.08) * mm, "mid": v(-21.58, -15.05) * mm, "end": v(-21.6, -15.02) * mm});
            skArc(sketch, "E410.2.368", {"start": v(-22.4, -14.7) * mm, "mid": v(-22.43, -14.77) * mm, "end": v(-22.43, -14.83) * mm});
            skArc(sketch, "E410.2.369", {"start": v(-21.72, -14.87) * mm, "mid": v(-21.72, -14.85) * mm, "end": v(-21.7, -14.84) * mm});
            skArc(sketch, "E410.2.370", {"start": v(-21.46, -14.3) * mm, "mid": v(-21.48, -14.29) * mm, "end": v(-21.5, -14.29) * mm});
            skArc(sketch, "E410.2.371", {"start": v(-21.46, -14.84) * mm, "mid": v(-21.44, -14.84) * mm, "end": v(-21.41, -14.84) * mm});
            skArc(sketch, "E410.2.372", {"start": v(-22.1, -15.66) * mm, "mid": v(-22.01, -15.74) * mm, "end": v(-21.92, -15.81) * mm});
            skArc(sketch, "E410.2.373", {"start": v(-21.57, -16.03) * mm, "mid": v(-21.48, -16.08) * mm, "end": v(-21.38, -16.11) * mm});
            skArc(sketch, "E410.2.374", {"start": v(-21.65, -14.3) * mm, "mid": v(-21.74, -14.29) * mm, "end": v(-21.83, -14.29) * mm});
            skArc(sketch, "E410.2.375", {"start": v(-20.91, -15.27) * mm, "mid": v(-21, -15.28) * mm, "end": v(-21.1, -15.27) * mm});
            skArc(sketch, "E410.2.376", {"start": v(-21.08, -16.18) * mm, "mid": v(-21.01, -16.19) * mm, "end": v(-20.94, -16.2) * mm});
            skArc(sketch, "E410.2.377", {"start": v(-21.45, -15.17) * mm, "mid": v(-21.51, -15.13) * mm, "end": v(-21.56, -15.08) * mm});
            skArc(sketch, "E410.2.378", {"start": v(-22.32, -14.56) * mm, "mid": v(-22.37, -14.63) * mm, "end": v(-22.4, -14.7) * mm});
            skArc(sketch, "E410.2.379", {"start": v(-21.71, -14.9) * mm, "mid": v(-21.72, -14.88) * mm, "end": v(-21.72, -14.87) * mm});
            skArc(sketch, "E410.2.380", {"start": v(-21.44, -14.3) * mm, "mid": v(-21.45, -14.3) * mm, "end": v(-21.46, -14.3) * mm});
            skArc(sketch, "E410.2.381", {"start": v(-21.52, -14.84) * mm, "mid": v(-21.49, -14.84) * mm, "end": v(-21.46, -14.84) * mm});
            skArc(sketch, "E410.2.382", {"start": v(-21.56, -14.3) * mm, "mid": v(-21.6, -14.3) * mm, "end": v(-21.65, -14.3) * mm});
            skArc(sketch, "E410.2.383", {"start": v(-21.33, -15.22) * mm, "mid": v(-21.4, -15.2) * mm, "end": v(-21.45, -15.17) * mm});
            skArc(sketch, "E410.2.384", {"start": v(-22.28, -14.51) * mm, "mid": v(-22.3, -14.53) * mm, "end": v(-22.32, -14.56) * mm});
            skArc(sketch, "E410.2.385", {"start": v(-21.64, -14.98) * mm, "mid": v(-21.68, -14.94) * mm, "end": v(-21.71, -14.9) * mm});
            skArc(sketch, "E410.2.386", {"start": v(-21.42, -14.33) * mm, "mid": v(-21.43, -14.32) * mm, "end": v(-21.44, -14.3) * mm});
            skArc(sketch, "E410.2.387", {"start": v(-21.57, -14.83) * mm, "mid": v(-21.54, -14.83) * mm, "end": v(-21.52, -14.84) * mm});
            skArc(sketch, "E410.2.388", {"start": v(-22.22, -14.46) * mm, "mid": v(-22.25, -14.49) * mm, "end": v(-22.28, -14.51) * mm});
            skArc(sketch, "E410.2.389", {"start": v(-21.4, -14.35) * mm, "mid": v(-21.41, -14.34) * mm, "end": v(-21.42, -14.33) * mm});
            skArc(sketch, "E410.2.390", {"start": v(-21.38, -14.37) * mm, "mid": v(-21.39, -14.36) * mm, "end": v(-21.4, -14.35) * mm});
            skArc(sketch, "E410.2.391", {"start": v(-21.36, -14.38) * mm, "mid": v(-21.37, -14.37) * mm, "end": v(-21.38, -14.37) * mm});
            skArc(sketch, "E410.2.392", {"start": v(-21.35, -14.4) * mm, "mid": v(-21.36, -14.4) * mm, "end": v(-21.36, -14.38) * mm});
            skArc(sketch, "E410.2.393", {"start": v(-21.31, -14.43) * mm, "mid": v(-21.33, -14.42) * mm, "end": v(-21.35, -14.4) * mm});
            skArc(sketch, "E410.2.394", {"start": v(-21.27, -14.45) * mm, "mid": v(-21.3, -14.44) * mm, "end": v(-21.31, -14.43) * mm});
            skArc(sketch, "E410.2.395", {"start": v(-21.25, -14.5) * mm, "mid": v(-21.25, -14.47) * mm, "end": v(-21.27, -14.45) * mm});
            skArc(sketch, "E410.2.396", {"start": v(-21.27, -14.74) * mm, "mid": v(-21.26, -14.7) * mm, "end": v(-21.26, -14.67) * mm});
            skArc(sketch, "E410.2.397", {"start": v(-21.29, -14.77) * mm, "mid": v(-21.28, -14.75) * mm, "end": v(-21.27, -14.74) * mm});
            skArc(sketch, "E410.2.398", {"start": v(-21.3, -14.8) * mm, "mid": v(-21.3, -14.78) * mm, "end": v(-21.29, -14.77) * mm});
            skArc(sketch, "E410.2.399", {"start": v(-21.35, -14.82) * mm, "mid": v(-21.33, -14.8) * mm, "end": v(-21.3, -14.8) * mm});
            skArc(sketch, "E410.3.0", {"start": v(20.05, -12.83) * mm, "mid": v(19.98, -12.71) * mm, "end": v(19.9, -12.6) * mm});
            skArc(sketch, "E410.3.1", {"start": v(19.83, -12.5) * mm, "mid": v(19.77, -12.44) * mm, "end": v(19.72, -12.38) * mm});
            skArc(sketch, "E410.3.2", {"start": v(19.41, -12.04) * mm, "mid": v(19.04, -11.7) * mm, "end": v(18.64, -11.37) * mm});
            skArc(sketch, "E410.3.3", {"start": v(20.13, -12.98) * mm, "mid": v(20.09, -12.9) * mm, "end": v(20.05, -12.83) * mm});
            skArc(sketch, "E410.3.4", {"start": v(19.9, -12.6) * mm, "mid": v(19.87, -12.55) * mm, "end": v(19.83, -12.5) * mm});
            skArc(sketch, "E410.3.5", {"start": v(19.56, -18.55) * mm, "mid": v(19.64, -18.46) * mm, "end": v(19.72, -18.38) * mm});
            skArc(sketch, "E410.3.6", {"start": v(19.56, -12.2) * mm, "mid": v(19.49, -12.12) * mm, "end": v(19.41, -12.04) * mm});
            skArc(sketch, "E410.3.7", {"start": v(20.23, -18) * mm, "mid": v(20.32, -17.93) * mm, "end": v(20.4, -17.85) * mm});
            skArc(sketch, "E410.3.8", {"start": v(20.4, -17.85) * mm, "mid": v(20.53, -17.7) * mm, "end": v(20.63, -17.51) * mm});
            skArc(sketch, "E410.3.9", {"start": v(20.68, -17.05) * mm, "mid": v(20.67, -16.93) * mm, "end": v(20.65, -16.82) * mm});
            skArc(sketch, "E410.3.10", {"start": v(20.65, -16.82) * mm, "mid": v(20.65, -16.73) * mm, "end": v(20.65, -16.64) * mm});
            skArc(sketch, "E410.3.11", {"start": v(20.66, -16.57) * mm, "mid": v(20.67, -16.53) * mm, "end": v(20.7, -16.49) * mm});
            skArc(sketch, "E410.3.12", {"start": v(19.37, -18.7) * mm, "mid": v(19.47, -18.63) * mm, "end": v(19.56, -18.55) * mm});
            skArc(sketch, "E410.3.13", {"start": v(19.72, -12.38) * mm, "mid": v(19.64, -12.3) * mm, "end": v(19.56, -12.2) * mm});
            skArc(sketch, "E410.3.14", {"start": v(19.87, -18.25) * mm, "mid": v(19.97, -18.16) * mm, "end": v(20.09, -18.08) * mm});
            skArc(sketch, "E410.3.15", {"start": v(20.09, -18.08) * mm, "mid": v(20.16, -18.04) * mm, "end": v(20.23, -18) * mm});
            skArc(sketch, "E410.3.16", {"start": v(20.7, -17.17) * mm, "mid": v(20.7, -17.1) * mm, "end": v(20.68, -17.05) * mm});
            skArc(sketch, "E410.3.17", {"start": v(20.65, -16.64) * mm, "mid": v(20.65, -16.6) * mm, "end": v(20.66, -16.57) * mm});
            skArc(sketch, "E410.3.18", {"start": v(19.72, -18.38) * mm, "mid": v(19.8, -18.31) * mm, "end": v(19.87, -18.25) * mm});
            skArc(sketch, "E410.3.19", {"start": v(20.63, -17.51) * mm, "mid": v(20.68, -17.34) * mm, "end": v(20.7, -17.17) * mm});
            skArc(sketch, "E410.3.20", {"start": v(18.64, -11.37) * mm, "mid": v(18.5, -11.27) * mm, "end": v(18.35, -11.18) * mm});
            skArc(sketch, "E410.3.21", {"start": v(20.25, -13.37) * mm, "mid": v(20.23, -13.26) * mm, "end": v(20.2, -13.16) * mm});
            skArc(sketch, "E410.3.22", {"start": v(20.2, -13.16) * mm, "mid": v(20.17, -13.07) * mm, "end": v(20.13, -12.98) * mm});
            skArc(sketch, "E410.3.23", {"start": v(13.89, -11.47) * mm, "mid": v(13.52, -11.59) * mm, "end": v(13.15, -11.69) * mm});
            skArc(sketch, "E410.3.24", {"start": v(18.7, -19.21) * mm, "mid": v(18.84, -19.12) * mm, "end": v(18.98, -19.02) * mm});
            skArc(sketch, "E410.3.25", {"start": v(19.12, -18.9) * mm, "mid": v(19.24, -18.8) * mm, "end": v(19.37, -18.7) * mm});
            skArc(sketch, "E410.3.26", {"start": v(20.28, -13.7) * mm, "mid": v(20.27, -13.54) * mm, "end": v(20.25, -13.37) * mm});
            skArc(sketch, "E410.3.27", {"start": v(14.18, -11.4) * mm, "mid": v(14.03, -11.42) * mm, "end": v(13.89, -11.47) * mm});
            skArc(sketch, "E410.3.28", {"start": v(12.96, -11.74) * mm, "mid": v(12.86, -11.77) * mm, "end": v(12.77, -11.8) * mm});
            skArc(sketch, "E410.3.29", {"start": v(18.38, -19.38) * mm, "mid": v(18.54, -19.3) * mm, "end": v(18.7, -19.21) * mm});
            skArc(sketch, "E410.3.30", {"start": v(18.98, -19.02) * mm, "mid": v(19.05, -18.96) * mm, "end": v(19.12, -18.9) * mm});
            skArc(sketch, "E410.3.31", {"start": v(15.37, -11.4) * mm, "mid": v(15.13, -11.38) * mm, "end": v(14.9, -11.38) * mm});
            skArc(sketch, "E410.3.32", {"start": v(14.9, -11.38) * mm, "mid": v(14.82, -11.38) * mm, "end": v(14.75, -11.37) * mm});
            skArc(sketch, "E410.3.33", {"start": v(14.75, -11.37) * mm, "mid": v(14.62, -11.36) * mm, "end": v(14.5, -11.37) * mm});
            skArc(sketch, "E410.3.34", {"start": v(14.5, -11.37) * mm, "mid": v(14.34, -11.38) * mm, "end": v(14.18, -11.4) * mm});
            skArc(sketch, "E410.3.35", {"start": v(13.15, -11.69) * mm, "mid": v(13.05, -11.71) * mm, "end": v(12.96, -11.74) * mm});
            skArc(sketch, "E410.3.36", {"start": v(12.66, -11.85) * mm, "mid": v(12.6, -11.88) * mm, "end": v(12.55, -11.92) * mm});
            skArc(sketch, "E410.3.37", {"start": v(12.36, -12.03) * mm, "mid": v(12.3, -12.06) * mm, "end": v(12.24, -12.1) * mm});
            skArc(sketch, "E410.3.38", {"start": v(12.24, -12.1) * mm, "mid": v(12, -12.3) * mm, "end": v(11.75, -12.49) * mm});
            skArc(sketch, "E410.3.39", {"start": v(12.77, -11.8) * mm, "mid": v(12.72, -11.83) * mm, "end": v(12.66, -11.85) * mm});
            skArc(sketch, "E410.3.40", {"start": v(12.55, -11.92) * mm, "mid": v(12.45, -11.97) * mm, "end": v(12.36, -12.03) * mm});
            skArc(sketch, "E410.3.41", {"start": v(16.66, -11.62) * mm, "mid": v(16.4, -11.55) * mm, "end": v(16.15, -11.48) * mm});
            skArc(sketch, "E410.3.42", {"start": v(16.15, -11.48) * mm, "mid": v(15.87, -11.43) * mm, "end": v(15.59, -11.4) * mm});
            skArc(sketch, "E410.3.43", {"start": v(15.59, -11.4) * mm, "mid": v(15.48, -11.4) * mm, "end": v(15.37, -11.4) * mm});
            skArc(sketch, "E410.3.44", {"start": v(17.9, -11.02) * mm, "mid": v(17.87, -11.03) * mm, "end": v(17.84, -11.04) * mm});
            skArc(sketch, "E410.3.45", {"start": v(17.84, -11.04) * mm, "mid": v(17.77, -11.07) * mm, "end": v(17.71, -11.1) * mm});
            skArc(sketch, "E410.3.46", {"start": v(17.44, -11.34) * mm, "mid": v(17.4, -11.4) * mm, "end": v(17.34, -11.45) * mm});
            skArc(sketch, "E410.3.47", {"start": v(17.22, -11.6) * mm, "mid": v(17.18, -11.66) * mm, "end": v(17.14, -11.73) * mm});
            skArc(sketch, "E410.3.48", {"start": v(21, -14.96) * mm, "mid": v(20.85, -14.9) * mm, "end": v(20.68, -14.86) * mm});
            skArc(sketch, "E410.3.49", {"start": v(20.52, -14.85) * mm, "mid": v(20.43, -14.84) * mm, "end": v(20.33, -14.85) * mm});
            skArc(sketch, "E410.3.50", {"start": v(16.68, -11.62) * mm, "mid": v(16.67, -11.62) * mm, "end": v(16.66, -11.62) * mm});
            skArc(sketch, "E410.3.51", {"start": v(20.8, -16.3) * mm, "mid": v(20.88, -16.16) * mm, "end": v(20.96, -16.02) * mm});
            skArc(sketch, "E410.3.52", {"start": v(20.24, -14.5) * mm, "mid": v(20.25, -14.38) * mm, "end": v(20.26, -14.26) * mm});
            skArc(sketch, "E410.3.53", {"start": v(20.96, -16.02) * mm, "mid": v(21.02, -15.92) * mm, "end": v(21.07, -15.82) * mm});
            skArc(sketch, "E410.3.54", {"start": v(20.26, -14.26) * mm, "mid": v(20.28, -13.98) * mm, "end": v(20.28, -13.7) * mm});
            skArc(sketch, "E410.3.55", {"start": v(21.2, -15.5) * mm, "mid": v(21.22, -15.4) * mm, "end": v(21.24, -15.27) * mm});
            skArc(sketch, "E410.3.56", {"start": v(17.97, -11.03) * mm, "mid": v(17.93, -11.02) * mm, "end": v(17.9, -11.02) * mm});
            skArc(sketch, "E410.3.57", {"start": v(17.71, -11.1) * mm, "mid": v(17.57, -11.22) * mm, "end": v(17.44, -11.34) * mm});
            skArc(sketch, "E410.3.58", {"start": v(17.34, -11.45) * mm, "mid": v(17.28, -11.53) * mm, "end": v(17.22, -11.6) * mm});
            skArc(sketch, "E410.3.59", {"start": v(21.24, -15.27) * mm, "mid": v(21.23, -15.2) * mm, "end": v(21.2, -15.14) * mm});
            skArc(sketch, "E410.3.60", {"start": v(21.2, -15.14) * mm, "mid": v(21.17, -15.1) * mm, "end": v(21.12, -15.05) * mm});
            skArc(sketch, "E410.3.61", {"start": v(21.12, -15.05) * mm, "mid": v(21.07, -15) * mm, "end": v(21, -14.96) * mm});
            skArc(sketch, "E410.3.62", {"start": v(16.98, -17.97) * mm, "mid": v(16.93, -18.05) * mm, "end": v(16.87, -18.1) * mm});
            skArc(sketch, "E410.3.63", {"start": v(15.93, -17.37) * mm, "mid": v(16.26, -17.24) * mm, "end": v(16.59, -17.12) * mm});
            skArc(sketch, "E410.3.64", {"start": v(20.68, -14.86) * mm, "mid": v(20.6, -14.85) * mm, "end": v(20.52, -14.85) * mm});
            skArc(sketch, "E410.3.65", {"start": v(16.87, -18.1) * mm, "mid": v(16.85, -18.13) * mm, "end": v(16.83, -18.14) * mm});
            skArc(sketch, "E410.3.66", {"start": v(16.59, -17.12) * mm, "mid": v(16.72, -17.06) * mm, "end": v(16.86, -17) * mm});
            skArc(sketch, "E410.3.67", {"start": v(16.86, -17) * mm, "mid": v(16.97, -16.95) * mm, "end": v(17.08, -16.9) * mm});
            skArc(sketch, "E410.3.68", {"start": v(16.64, -18.3) * mm, "mid": v(16.53, -18.43) * mm, "end": v(16.43, -18.56) * mm});
            skArc(sketch, "E410.3.69", {"start": v(16.75, -11.65) * mm, "mid": v(16.72, -11.64) * mm, "end": v(16.68, -11.62) * mm});
            skArc(sketch, "E410.3.70", {"start": v(17.17, -17) * mm, "mid": v(17.19, -17.09) * mm, "end": v(17.21, -17.18) * mm});
            skArc(sketch, "E410.3.71", {"start": v(20.7, -16.49) * mm, "mid": v(20.75, -16.39) * mm, "end": v(20.8, -16.3) * mm});
            skArc(sketch, "E410.3.72", {"start": v(17.21, -17.18) * mm, "mid": v(17.24, -17.28) * mm, "end": v(17.26, -17.37) * mm});
            skArc(sketch, "E410.3.73", {"start": v(20.23, -14.63) * mm, "mid": v(20.23, -14.57) * mm, "end": v(20.24, -14.5) * mm});
            skArc(sketch, "E410.3.74", {"start": v(17.27, -17.48) * mm, "mid": v(17.27, -17.53) * mm, "end": v(17.27, -17.58) * mm});
            skArc(sketch, "E410.3.75", {"start": v(21.07, -15.82) * mm, "mid": v(21.14, -15.66) * mm, "end": v(21.2, -15.5) * mm});
            skArc(sketch, "E410.3.76", {"start": v(17.08, -11.75) * mm, "mid": v(17.04, -11.73) * mm, "end": v(16.99, -11.72) * mm});
            skArc(sketch, "E410.3.77", {"start": v(18.09, -11.06) * mm, "mid": v(18.03, -11.04) * mm, "end": v(17.97, -11.03) * mm});
            skArc(sketch, "E410.3.78", {"start": v(15, -17.63) * mm, "mid": v(15.33, -17.56) * mm, "end": v(15.66, -17.46) * mm});
            skArc(sketch, "E410.3.79", {"start": v(17.17, -17.74) * mm, "mid": v(17.12, -17.79) * mm, "end": v(17.08, -17.83) * mm});
            skArc(sketch, "E410.3.80", {"start": v(15.66, -17.46) * mm, "mid": v(15.8, -17.42) * mm, "end": v(15.93, -17.37) * mm});
            skArc(sketch, "E410.3.81", {"start": v(10.68, -12.95) * mm, "mid": v(10.51, -13) * mm, "end": v(10.34, -13.06) * mm});
            skArc(sketch, "E410.3.82", {"start": v(10.34, -13.06) * mm, "mid": v(10.17, -13.12) * mm, "end": v(10, -13.19) * mm});
            skArc(sketch, "E410.3.83", {"start": v(16.83, -18.14) * mm, "mid": v(16.73, -18.22) * mm, "end": v(16.64, -18.3) * mm});
            skArc(sketch, "E410.3.84", {"start": v(9.12, -14.28) * mm, "mid": v(9.17, -14.36) * mm, "end": v(9.22, -14.45) * mm});
            skArc(sketch, "E410.3.85", {"start": v(9.8, -13.31) * mm, "mid": v(9.67, -13.41) * mm, "end": v(9.53, -13.5) * mm});
            skArc(sketch, "E410.3.86", {"start": v(9.22, -14.45) * mm, "mid": v(9.26, -14.5) * mm, "end": v(9.3, -14.56) * mm});
            skArc(sketch, "E410.3.87", {"start": v(17.15, -16.9) * mm, "mid": v(17.16, -16.95) * mm, "end": v(17.17, -17) * mm});
            skArc(sketch, "E410.3.88", {"start": v(16.79, -11.66) * mm, "mid": v(16.77, -11.66) * mm, "end": v(16.75, -11.65) * mm});
            skArc(sketch, "E410.3.89", {"start": v(9.3, -13.6) * mm, "mid": v(9.26, -13.63) * mm, "end": v(9.21, -13.66) * mm});
            skArc(sketch, "E410.3.90", {"start": v(20.22, -14.7) * mm, "mid": v(20.22, -14.66) * mm, "end": v(20.23, -14.63) * mm});
            skArc(sketch, "E410.3.91", {"start": v(17.26, -17.37) * mm, "mid": v(17.27, -17.43) * mm, "end": v(17.27, -17.48) * mm});
            skArc(sketch, "E410.3.92", {"start": v(11.41, -12.75) * mm, "mid": v(11.33, -12.78) * mm, "end": v(11.26, -12.8) * mm});
            skArc(sketch, "E410.3.93", {"start": v(8.98, -13.81) * mm, "mid": v(8.97, -13.84) * mm, "end": v(8.96, -13.88) * mm});
            skArc(sketch, "E410.3.94", {"start": v(17.12, -11.75) * mm, "mid": v(17.1, -11.75) * mm, "end": v(17.08, -11.75) * mm});
            skArc(sketch, "E410.3.95", {"start": v(14.83, -17.66) * mm, "mid": v(14.91, -17.64) * mm, "end": v(15, -17.63) * mm});
            skArc(sketch, "E410.3.96", {"start": v(18.35, -11.18) * mm, "mid": v(18.22, -11.11) * mm, "end": v(18.09, -11.06) * mm});
            skArc(sketch, "E410.3.97", {"start": v(17.22, -17.7) * mm, "mid": v(17.2, -17.72) * mm, "end": v(17.17, -17.74) * mm});
            skArc(sketch, "E410.3.98", {"start": v(11.03, -12.87) * mm, "mid": v(10.92, -12.9) * mm, "end": v(10.8, -12.92) * mm});
            skArc(sketch, "E410.3.99", {"start": v(9.69, -14.85) * mm, "mid": v(9.74, -14.8) * mm, "end": v(9.79, -14.75) * mm});
            skArc(sketch, "E410.3.100", {"start": v(8.95, -13.92) * mm, "mid": v(8.95, -13.94) * mm, "end": v(8.95, -13.96) * mm});
            skArc(sketch, "E410.3.101", {"start": v(10.8, -12.92) * mm, "mid": v(10.74, -12.93) * mm, "end": v(10.68, -12.95) * mm});
            skArc(sketch, "E410.3.102", {"start": v(9.06, -14.2) * mm, "mid": v(9.1, -14.24) * mm, "end": v(9.12, -14.28) * mm});
            skArc(sketch, "E410.3.103", {"start": v(9.87, -13.26) * mm, "mid": v(9.84, -13.28) * mm, "end": v(9.8, -13.31) * mm});
            skArc(sketch, "E410.3.104", {"start": v(9.91, -14.41) * mm, "mid": v(9.93, -14.37) * mm, "end": v(9.95, -14.32) * mm});
            skArc(sketch, "E410.3.105", {"start": v(17.14, -16.9) * mm, "mid": v(17.15, -16.9) * mm, "end": v(17.15, -16.9) * mm});
            skArc(sketch, "E410.3.106", {"start": v(16.87, -11.68) * mm, "mid": v(16.83, -11.67) * mm, "end": v(16.79, -11.66) * mm});
            skArc(sketch, "E410.3.107", {"start": v(9.41, -13.55) * mm, "mid": v(9.36, -13.58) * mm, "end": v(9.3, -13.6) * mm});
            skArc(sketch, "E410.3.108", {"start": v(20.2, -14.75) * mm, "mid": v(20.2, -14.72) * mm, "end": v(20.22, -14.7) * mm});
            skArc(sketch, "E410.3.109", {"start": v(11.45, -12.74) * mm, "mid": v(11.43, -12.75) * mm, "end": v(11.41, -12.75) * mm});
            skArc(sketch, "E410.3.110", {"start": v(14.54, -17.74) * mm, "mid": v(14.68, -17.7) * mm, "end": v(14.83, -17.66) * mm});
            skArc(sketch, "E410.3.111", {"start": v(17.25, -17.65) * mm, "mid": v(17.24, -17.67) * mm, "end": v(17.22, -17.7) * mm});
            skArc(sketch, "E410.3.112", {"start": v(11.26, -12.8) * mm, "mid": v(11.15, -12.84) * mm, "end": v(11.03, -12.87) * mm});
            skArc(sketch, "E410.3.113", {"start": v(17.14, -11.73) * mm, "mid": v(17.13, -11.74) * mm, "end": v(17.12, -11.75) * mm});
            skArc(sketch, "E410.3.114", {"start": v(9.66, -14.86) * mm, "mid": v(9.67, -14.86) * mm, "end": v(9.69, -14.85) * mm});
            skArc(sketch, "E410.3.115", {"start": v(8.96, -13.88) * mm, "mid": v(8.96, -13.9) * mm, "end": v(8.95, -13.92) * mm});
            skArc(sketch, "E410.3.116", {"start": v(9, -14.12) * mm, "mid": v(9.02, -14.16) * mm, "end": v(9.06, -14.2) * mm});
            skArc(sketch, "E410.3.117", {"start": v(10, -13.19) * mm, "mid": v(9.93, -13.22) * mm, "end": v(9.87, -13.26) * mm});
            skArc(sketch, "E410.3.118", {"start": v(17.11, -16.88) * mm, "mid": v(17.13, -16.88) * mm, "end": v(17.14, -16.9) * mm});
            skArc(sketch, "E410.3.119", {"start": v(16.93, -11.7) * mm, "mid": v(16.9, -11.7) * mm, "end": v(16.87, -11.68) * mm});
            skArc(sketch, "E410.3.120", {"start": v(9.53, -13.5) * mm, "mid": v(9.47, -13.53) * mm, "end": v(9.41, -13.55) * mm});
            skArc(sketch, "E410.3.121", {"start": v(20.2, -14.81) * mm, "mid": v(20.2, -14.78) * mm, "end": v(20.2, -14.75) * mm});
            skArc(sketch, "E410.3.122", {"start": v(10.23, -14.02) * mm, "mid": v(10.26, -14) * mm, "end": v(10.28, -13.98) * mm});
            skArc(sketch, "E410.3.123", {"start": v(11.51, -12.7) * mm, "mid": v(11.48, -12.72) * mm, "end": v(11.45, -12.74) * mm});
            skArc(sketch, "E410.3.124", {"start": v(10.36, -13.95) * mm, "mid": v(10.4, -13.94) * mm, "end": v(10.45, -13.92) * mm});
            skArc(sketch, "E410.3.125", {"start": v(9.04, -13.74) * mm, "mid": v(9.01, -13.77) * mm, "end": v(8.98, -13.81) * mm});
            skArc(sketch, "E410.3.126", {"start": v(14.25, -17.82) * mm, "mid": v(14.4, -17.78) * mm, "end": v(14.54, -17.74) * mm});
            skArc(sketch, "E410.3.127", {"start": v(17.27, -17.58) * mm, "mid": v(17.26, -17.62) * mm, "end": v(17.25, -17.65) * mm});
            skArc(sketch, "E410.3.128", {"start": v(10.74, -13.84) * mm, "mid": v(10.96, -13.82) * mm, "end": v(11.19, -13.84) * mm});
            skArc(sketch, "E410.3.129", {"start": v(9.64, -14.85) * mm, "mid": v(9.65, -14.86) * mm, "end": v(9.66, -14.86) * mm});
            skArc(sketch, "E410.3.130", {"start": v(17.08, -17.83) * mm, "mid": v(17.02, -17.9) * mm, "end": v(16.98, -17.97) * mm});
            skArc(sketch, "E410.3.131", {"start": v(8.96, -14.08) * mm, "mid": v(8.97, -14.1) * mm, "end": v(9, -14.12) * mm});
            skArc(sketch, "E410.3.132", {"start": v(10.71, -15.4) * mm, "mid": v(10.66, -15.45) * mm, "end": v(10.6, -15.49) * mm});
            skArc(sketch, "E410.3.133", {"start": v(9.87, -14.53) * mm, "mid": v(9.9, -14.47) * mm, "end": v(9.91, -14.41) * mm});
            skArc(sketch, "E410.3.134", {"start": v(16.99, -11.72) * mm, "mid": v(16.96, -11.7) * mm, "end": v(16.93, -11.7) * mm});
            skArc(sketch, "E410.3.135", {"start": v(12.03, -13.9) * mm, "mid": v(12.12, -13.93) * mm, "end": v(12.2, -13.97) * mm});
            skArc(sketch, "E410.3.136", {"start": v(17.08, -16.9) * mm, "mid": v(17.1, -16.89) * mm, "end": v(17.11, -16.88) * mm});
            skArc(sketch, "E410.3.137", {"start": v(20.22, -14.84) * mm, "mid": v(20.2, -14.83) * mm, "end": v(20.2, -14.81) * mm});
            skArc(sketch, "E410.3.138", {"start": v(12, -14.84) * mm, "mid": v(11.82, -14.88) * mm, "end": v(11.65, -14.92) * mm});
            skArc(sketch, "E410.3.139", {"start": v(12.3, -14.06) * mm, "mid": v(12.35, -14.1) * mm, "end": v(12.4, -14.14) * mm});
            skArc(sketch, "E410.3.140", {"start": v(11.65, -14.92) * mm, "mid": v(11.57, -14.94) * mm, "end": v(11.5, -14.97) * mm});
            skArc(sketch, "E410.3.141", {"start": v(10.1, -14.13) * mm, "mid": v(10.16, -14.07) * mm, "end": v(10.23, -14.02) * mm});
            skArc(sketch, "E410.3.142", {"start": v(12.7, -14.4) * mm, "mid": v(12.74, -14.43) * mm, "end": v(12.77, -14.46) * mm});
            skArc(sketch, "E410.3.143", {"start": v(11.75, -12.49) * mm, "mid": v(11.63, -12.6) * mm, "end": v(11.51, -12.7) * mm});
            skArc(sketch, "E410.3.144", {"start": v(10.32, -13.97) * mm, "mid": v(10.34, -13.96) * mm, "end": v(10.36, -13.95) * mm});
            skArc(sketch, "E410.3.145", {"start": v(9.1, -13.7) * mm, "mid": v(9.07, -13.72) * mm, "end": v(9.04, -13.74) * mm});
            skArc(sketch, "E410.3.146", {"start": v(13.52, -15.99) * mm, "mid": v(13.34, -16.13) * mm, "end": v(13.15, -16.28) * mm});
            skArc(sketch, "E410.3.147", {"start": v(12.1, -15.62) * mm, "mid": v(12.15, -15.61) * mm, "end": v(12.2, -15.6) * mm});
            skArc(sketch, "E410.3.148", {"start": v(10.45, -13.92) * mm, "mid": v(10.6, -13.87) * mm, "end": v(10.74, -13.84) * mm});
            skArc(sketch, "E410.3.149", {"start": v(9.62, -14.83) * mm, "mid": v(9.63, -14.84) * mm, "end": v(9.64, -14.85) * mm});
            skArc(sketch, "E410.3.150", {"start": v(12.2, -15.6) * mm, "mid": v(12.35, -15.6) * mm, "end": v(12.5, -15.62) * mm});
            skArc(sketch, "E410.3.151", {"start": v(11.3, -15.07) * mm, "mid": v(11.27, -15.09) * mm, "end": v(11.25, -15.1) * mm});
            skArc(sketch, "E410.3.152", {"start": v(11.19, -13.84) * mm, "mid": v(11.3, -13.87) * mm, "end": v(11.4, -13.9) * mm});
            skArc(sketch, "E410.3.153", {"start": v(12.69, -14.64) * mm, "mid": v(12.66, -14.65) * mm, "end": v(12.64, -14.67) * mm});
            skArc(sketch, "E410.3.154", {"start": v(11.4, -13.9) * mm, "mid": v(11.46, -13.91) * mm, "end": v(11.52, -13.93) * mm});
            skArc(sketch, "E410.3.155", {"start": v(11.02, -15.22) * mm, "mid": v(10.96, -15.25) * mm, "end": v(10.91, -15.27) * mm});
            skArc(sketch, "E410.3.156", {"start": v(8.94, -14.02) * mm, "mid": v(8.95, -14.05) * mm, "end": v(8.96, -14.08) * mm});
            skArc(sketch, "E410.3.157", {"start": v(10.84, -15.32) * mm, "mid": v(10.78, -15.37) * mm, "end": v(10.71, -15.4) * mm});
            skArc(sketch, "E410.3.158", {"start": v(11.78, -13.92) * mm, "mid": v(11.86, -13.91) * mm, "end": v(11.94, -13.9) * mm});
            skArc(sketch, "E410.3.159", {"start": v(9.84, -14.6) * mm, "mid": v(9.85, -14.56) * mm, "end": v(9.87, -14.53) * mm});
            skArc(sketch, "E410.3.160", {"start": v(13.38, -15.81) * mm, "mid": v(13.46, -15.8) * mm, "end": v(13.53, -15.79) * mm});
            skArc(sketch, "E410.3.161", {"start": v(11.94, -13.9) * mm, "mid": v(11.98, -13.9) * mm, "end": v(12.03, -13.9) * mm});
            skArc(sketch, "E410.3.162", {"start": v(12.28, -14.8) * mm, "mid": v(12.14, -14.82) * mm, "end": v(12, -14.84) * mm});
            skArc(sketch, "E410.3.163", {"start": v(12.2, -13.97) * mm, "mid": v(12.25, -14.01) * mm, "end": v(12.3, -14.06) * mm});
            skArc(sketch, "E410.3.164", {"start": v(20.25, -14.85) * mm, "mid": v(20.23, -14.85) * mm, "end": v(20.22, -14.84) * mm});
            skArc(sketch, "E410.3.165", {"start": v(10.02, -14.21) * mm, "mid": v(10.05, -14.17) * mm, "end": v(10.1, -14.13) * mm});
            skArc(sketch, "E410.3.166", {"start": v(10.52, -15.82) * mm, "mid": v(10.59, -15.95) * mm, "end": v(10.67, -16.08) * mm});
            skArc(sketch, "E410.3.167", {"start": v(12.44, -14.18) * mm, "mid": v(12.58, -14.3) * mm, "end": v(12.7, -14.4) * mm});
            skArc(sketch, "E410.3.168", {"start": v(13.53, -18.06) * mm, "mid": v(13.61, -18.01) * mm, "end": v(13.7, -17.98) * mm});
            skArc(sketch, "E410.3.169", {"start": v(10.78, -16.23) * mm, "mid": v(10.85, -16.32) * mm, "end": v(10.93, -16.4) * mm});
            skArc(sketch, "E410.3.170", {"start": v(10.28, -13.98) * mm, "mid": v(10.3, -13.98) * mm, "end": v(10.32, -13.97) * mm});
            skArc(sketch, "E410.3.171", {"start": v(11.71, -15.8) * mm, "mid": v(11.85, -15.72) * mm, "end": v(12, -15.66) * mm});
            skArc(sketch, "E410.3.172", {"start": v(13.7, -17.98) * mm, "mid": v(13.78, -17.94) * mm, "end": v(13.88, -17.92) * mm});
            skArc(sketch, "E410.3.173", {"start": v(9.15, -13.68) * mm, "mid": v(9.12, -13.7) * mm, "end": v(9.1, -13.7) * mm});
            skArc(sketch, "E410.3.174", {"start": v(10.93, -16.4) * mm, "mid": v(11, -16.47) * mm, "end": v(11.08, -16.53) * mm});
            skArc(sketch, "E410.3.175", {"start": v(13.6, -15.92) * mm, "mid": v(13.56, -15.95) * mm, "end": v(13.52, -15.99) * mm});
            skArc(sketch, "E410.3.176", {"start": v(12, -15.66) * mm, "mid": v(12.05, -15.64) * mm, "end": v(12.1, -15.62) * mm});
            skArc(sketch, "E410.3.177", {"start": v(13.88, -17.92) * mm, "mid": v(13.97, -17.9) * mm, "end": v(14.06, -17.87) * mm});
            skArc(sketch, "E410.3.178", {"start": v(9.6, -14.81) * mm, "mid": v(9.6, -14.82) * mm, "end": v(9.62, -14.83) * mm});
            skArc(sketch, "E410.3.179", {"start": v(11.34, -15.05) * mm, "mid": v(11.32, -15.06) * mm, "end": v(11.3, -15.07) * mm});
            skArc(sketch, "E410.3.180", {"start": v(14.06, -17.87) * mm, "mid": v(14.16, -17.85) * mm, "end": v(14.25, -17.82) * mm});
            skArc(sketch, "E410.3.181", {"start": v(13.15, -16.28) * mm, "mid": v(12.99, -16.4) * mm, "end": v(12.82, -16.53) * mm});
            skArc(sketch, "E410.3.182", {"start": v(12.82, -16.53) * mm, "mid": v(12.73, -16.59) * mm, "end": v(12.64, -16.64) * mm});
            skArc(sketch, "E410.3.183", {"start": v(12.73, -14.6) * mm, "mid": v(12.7, -14.62) * mm, "end": v(12.69, -14.64) * mm});
            skArc(sketch, "E410.3.184", {"start": v(12.78, -15.69) * mm, "mid": v(12.89, -15.73) * mm, "end": v(13, -15.77) * mm});
            skArc(sketch, "E410.3.185", {"start": v(11.21, -15.13) * mm, "mid": v(11.12, -15.18) * mm, "end": v(11.02, -15.22) * mm});
            skArc(sketch, "E410.3.186", {"start": v(13, -15.77) * mm, "mid": v(13.05, -15.79) * mm, "end": v(13.1, -15.8) * mm});
            skArc(sketch, "E410.3.187", {"start": v(11.25, -16.53) * mm, "mid": v(11.3, -16.46) * mm, "end": v(11.34, -16.39) * mm});
            skArc(sketch, "E410.3.188", {"start": v(8.95, -13.96) * mm, "mid": v(8.94, -13.99) * mm, "end": v(8.94, -14.02) * mm});
            skArc(sketch, "E410.3.189", {"start": v(11.66, -13.93) * mm, "mid": v(11.72, -13.93) * mm, "end": v(11.78, -13.92) * mm});
            skArc(sketch, "E410.3.190", {"start": v(9.83, -14.65) * mm, "mid": v(9.83, -14.62) * mm, "end": v(9.84, -14.6) * mm});
            skArc(sketch, "E410.3.191", {"start": v(12.16, -16.93) * mm, "mid": v(12.08, -16.99) * mm, "end": v(12, -17.05) * mm});
            skArc(sketch, "E410.3.192", {"start": v(13.2, -15.82) * mm, "mid": v(13.29, -15.82) * mm, "end": v(13.38, -15.81) * mm});
            skArc(sketch, "E410.3.193", {"start": v(12.39, -14.78) * mm, "mid": v(12.33, -14.79) * mm, "end": v(12.28, -14.8) * mm});
            skArc(sketch, "E410.3.194", {"start": v(11.77, -17.19) * mm, "mid": v(11.72, -17.2) * mm, "end": v(11.66, -17.22) * mm});
            skArc(sketch, "E410.3.195", {"start": v(20.33, -14.85) * mm, "mid": v(20.29, -14.85) * mm, "end": v(20.25, -14.85) * mm});
            skArc(sketch, "E410.3.196", {"start": v(9.95, -14.32) * mm, "mid": v(9.98, -14.26) * mm, "end": v(10.02, -14.21) * mm});
            skArc(sketch, "E410.3.197", {"start": v(11.47, -16.04) * mm, "mid": v(11.49, -16.01) * mm, "end": v(11.5, -15.99) * mm});
            skArc(sketch, "E410.3.198", {"start": v(10.48, -15.72) * mm, "mid": v(10.5, -15.77) * mm, "end": v(10.52, -15.82) * mm});
            skArc(sketch, "E410.3.199", {"start": v(13.3, -18.22) * mm, "mid": v(13.41, -18.14) * mm, "end": v(13.53, -18.06) * mm});
            skArc(sketch, "E410.3.200", {"start": v(12.4, -14.14) * mm, "mid": v(12.42, -14.16) * mm, "end": v(12.44, -14.18) * mm});
            skArc(sketch, "E410.3.201", {"start": v(10.67, -16.08) * mm, "mid": v(10.72, -16.15) * mm, "end": v(10.78, -16.23) * mm});
            skArc(sketch, "E410.3.202", {"start": v(11.62, -15.87) * mm, "mid": v(11.67, -15.83) * mm, "end": v(11.71, -15.8) * mm});
            skArc(sketch, "E410.3.203", {"start": v(9.21, -13.66) * mm, "mid": v(9.18, -13.67) * mm, "end": v(9.15, -13.68) * mm});
            skArc(sketch, "E410.3.204", {"start": v(13.7, -15.84) * mm, "mid": v(13.65, -15.88) * mm, "end": v(13.6, -15.92) * mm});
            skArc(sketch, "E410.3.205", {"start": v(9.51, -14.77) * mm, "mid": v(9.56, -14.8) * mm, "end": v(9.6, -14.81) * mm});
            skArc(sketch, "E410.3.206", {"start": v(11.4, -15.02) * mm, "mid": v(11.37, -15.03) * mm, "end": v(11.34, -15.05) * mm});
            skArc(sketch, "E410.3.207", {"start": v(12.79, -14.56) * mm, "mid": v(12.76, -14.59) * mm, "end": v(12.73, -14.6) * mm});
            skArc(sketch, "E410.3.208", {"start": v(12.5, -15.62) * mm, "mid": v(12.64, -15.65) * mm, "end": v(12.78, -15.69) * mm});
            skArc(sketch, "E410.3.209", {"start": v(11.25, -15.1) * mm, "mid": v(11.23, -15.12) * mm, "end": v(11.21, -15.13) * mm});
            skArc(sketch, "E410.3.210", {"start": v(11.2, -16.56) * mm, "mid": v(11.23, -16.55) * mm, "end": v(11.25, -16.53) * mm});
            skArc(sketch, "E410.3.211", {"start": v(12.53, -16.7) * mm, "mid": v(12.42, -16.75) * mm, "end": v(12.32, -16.8) * mm});
            skArc(sketch, "E410.3.212", {"start": v(11.52, -13.93) * mm, "mid": v(11.59, -13.93) * mm, "end": v(11.66, -13.93) * mm});
            skArc(sketch, "E410.3.213", {"start": v(9.79, -14.75) * mm, "mid": v(9.82, -14.7) * mm, "end": v(9.83, -14.65) * mm});
            skArc(sketch, "E410.3.214", {"start": v(12.32, -16.8) * mm, "mid": v(12.24, -16.86) * mm, "end": v(12.16, -16.93) * mm});
            skArc(sketch, "E410.3.215", {"start": v(13.1, -15.8) * mm, "mid": v(13.15, -15.81) * mm, "end": v(13.2, -15.82) * mm});
            skArc(sketch, "E410.3.216", {"start": v(11.34, -16.39) * mm, "mid": v(11.36, -16.35) * mm, "end": v(11.36, -16.3) * mm});
            skArc(sketch, "E410.3.217", {"start": v(10.91, -15.27) * mm, "mid": v(10.88, -15.3) * mm, "end": v(10.84, -15.32) * mm});
            skArc(sketch, "E410.3.218", {"start": v(17.18, -20.49) * mm, "mid": v(17.34, -20.16) * mm, "end": v(17.5, -19.84) * mm});
            skArc(sketch, "E410.3.219", {"start": v(11.45, -16.1) * mm, "mid": v(11.46, -16.07) * mm, "end": v(11.47, -16.04) * mm});
            skArc(sketch, "E410.3.220", {"start": v(16.9, -20.42) * mm, "mid": v(16.86, -20.52) * mm, "end": v(16.83, -20.61) * mm});
            skArc(sketch, "E410.3.221", {"start": v(10.48, -15.67) * mm, "mid": v(10.48, -15.7) * mm, "end": v(10.48, -15.72) * mm});
            skArc(sketch, "E410.3.222", {"start": v(16.43, -18.56) * mm, "mid": v(16.28, -18.77) * mm, "end": v(16.14, -19) * mm});
            skArc(sketch, "E410.3.223", {"start": v(17.72, -19.64) * mm, "mid": v(17.75, -19.64) * mm, "end": v(17.78, -19.63) * mm});
            skArc(sketch, "E410.3.224", {"start": v(17.78, -19.63) * mm, "mid": v(17.9, -19.58) * mm, "end": v(18.02, -19.54) * mm});
            skArc(sketch, "E410.3.225", {"start": v(16.11, -19.05) * mm, "mid": v(16.1, -19.08) * mm, "end": v(16.09, -19.1) * mm});
            skArc(sketch, "E410.3.226", {"start": v(18.02, -19.54) * mm, "mid": v(18.2, -19.46) * mm, "end": v(18.38, -19.38) * mm});
            skArc(sketch, "E410.3.227", {"start": v(16.73, -21.03) * mm, "mid": v(16.73, -21.14) * mm, "end": v(16.74, -21.25) * mm});
            skArc(sketch, "E410.3.228", {"start": v(11.54, -15.94) * mm, "mid": v(11.58, -15.9) * mm, "end": v(11.62, -15.87) * mm});
            skArc(sketch, "E410.3.229", {"start": v(13.71, -15.81) * mm, "mid": v(13.7, -15.83) * mm, "end": v(13.7, -15.84) * mm});
            skArc(sketch, "E410.3.230", {"start": v(9.46, -14.72) * mm, "mid": v(9.48, -14.75) * mm, "end": v(9.51, -14.77) * mm});
            skArc(sketch, "E410.3.231", {"start": v(11.45, -15) * mm, "mid": v(11.43, -15.01) * mm, "end": v(11.4, -15.02) * mm});
            skArc(sketch, "E410.3.232", {"start": v(16.75, -20.14) * mm, "mid": v(16.82, -20.08) * mm, "end": v(16.9, -20.03) * mm});
            skArc(sketch, "E410.3.233", {"start": v(12.8, -14.53) * mm, "mid": v(12.8, -14.55) * mm, "end": v(12.79, -14.56) * mm});
            skArc(sketch, "E410.3.234", {"start": v(15.87, -19.4) * mm, "mid": v(15.77, -19.54) * mm, "end": v(15.68, -19.69) * mm});
            skArc(sketch, "E410.3.235", {"start": v(11.17, -16.57) * mm, "mid": v(11.19, -16.57) * mm, "end": v(11.2, -16.56) * mm});
            skArc(sketch, "E410.3.236", {"start": v(15.68, -19.69) * mm, "mid": v(15.53, -19.95) * mm, "end": v(15.4, -20.23) * mm});
            skArc(sketch, "E410.3.237", {"start": v(16.87, -21.37) * mm, "mid": v(16.88, -21.34) * mm, "end": v(16.88, -21.31) * mm});
            skArc(sketch, "E410.3.238", {"start": v(12.64, -16.64) * mm, "mid": v(12.59, -16.67) * mm, "end": v(12.53, -16.7) * mm});
            skArc(sketch, "E410.3.239", {"start": v(16.9, -21.2) * mm, "mid": v(16.98, -20.98) * mm, "end": v(17.05, -20.78) * mm});
            skArc(sketch, "E410.3.240", {"start": v(17.01, -19.97) * mm, "mid": v(17.02, -19.98) * mm, "end": v(17.02, -19.98) * mm});
            skArc(sketch, "E410.3.241", {"start": v(17.05, -20.78) * mm, "mid": v(17.11, -20.63) * mm, "end": v(17.18, -20.49) * mm});
            skArc(sketch, "E410.3.242", {"start": v(11.42, -16.16) * mm, "mid": v(11.44, -16.13) * mm, "end": v(11.45, -16.1) * mm});
            skArc(sketch, "E410.3.243", {"start": v(16.96, -20.2) * mm, "mid": v(16.93, -20.31) * mm, "end": v(16.9, -20.42) * mm});
            skArc(sketch, "E410.3.244", {"start": v(10.5, -15.61) * mm, "mid": v(10.5, -15.64) * mm, "end": v(10.48, -15.67) * mm});
            skArc(sketch, "E410.3.245", {"start": v(17.66, -19.66) * mm, "mid": v(17.69, -19.65) * mm, "end": v(17.72, -19.64) * mm});
            skArc(sketch, "E410.3.246", {"start": v(11.5, -15.99) * mm, "mid": v(11.52, -15.96) * mm, "end": v(11.54, -15.94) * mm});
            skArc(sketch, "E410.3.247", {"start": v(16.14, -19) * mm, "mid": v(16.12, -19.02) * mm, "end": v(16.11, -19.05) * mm});
            skArc(sketch, "E410.3.248", {"start": v(16.4, -20.61) * mm, "mid": v(16.43, -20.57) * mm, "end": v(16.46, -20.52) * mm});
            skArc(sketch, "E410.3.249", {"start": v(13.73, -15.78) * mm, "mid": v(13.73, -15.8) * mm, "end": v(13.71, -15.81) * mm});
            skArc(sketch, "E410.3.250", {"start": v(9.38, -14.64) * mm, "mid": v(9.42, -14.68) * mm, "end": v(9.46, -14.72) * mm});
            skArc(sketch, "E410.3.251", {"start": v(11.5, -14.97) * mm, "mid": v(11.48, -14.99) * mm, "end": v(11.45, -15) * mm});
            skArc(sketch, "E410.3.252", {"start": v(16.64, -20.23) * mm, "mid": v(16.7, -20.18) * mm, "end": v(16.75, -20.14) * mm});
            skArc(sketch, "E410.3.253", {"start": v(12.8, -14.5) * mm, "mid": v(12.8, -14.51) * mm, "end": v(12.8, -14.53) * mm});
            skArc(sketch, "E410.3.254", {"start": v(16, -19.24) * mm, "mid": v(15.93, -19.32) * mm, "end": v(15.87, -19.4) * mm});
            skArc(sketch, "E410.3.255", {"start": v(11.14, -16.56) * mm, "mid": v(11.15, -16.57) * mm, "end": v(11.17, -16.57) * mm});
            skArc(sketch, "E410.3.256", {"start": v(16.85, -21.4) * mm, "mid": v(16.86, -21.39) * mm, "end": v(16.87, -21.37) * mm});
            skArc(sketch, "E410.3.257", {"start": v(16.88, -21.31) * mm, "mid": v(16.9, -21.25) * mm, "end": v(16.9, -21.2) * mm});
            skArc(sketch, "E410.3.258", {"start": v(17, -19.97) * mm, "mid": v(17, -19.97) * mm, "end": v(17.01, -19.97) * mm});
            skArc(sketch, "E410.3.259", {"start": v(17, -20.1) * mm, "mid": v(16.97, -20.15) * mm, "end": v(16.96, -20.2) * mm});
            skArc(sketch, "E410.3.260", {"start": v(11.39, -16.22) * mm, "mid": v(11.4, -16.2) * mm, "end": v(11.42, -16.16) * mm});
            skArc(sketch, "E410.3.261", {"start": v(10.6, -15.49) * mm, "mid": v(10.54, -15.54) * mm, "end": v(10.5, -15.61) * mm});
            skArc(sketch, "E410.3.262", {"start": v(17.57, -19.73) * mm, "mid": v(17.6, -19.7) * mm, "end": v(17.66, -19.66) * mm});
            skArc(sketch, "E410.3.263", {"start": v(16.83, -20.61) * mm, "mid": v(16.8, -20.71) * mm, "end": v(16.77, -20.81) * mm});
            skArc(sketch, "E410.3.264", {"start": v(13.72, -15.75) * mm, "mid": v(13.73, -15.76) * mm, "end": v(13.73, -15.78) * mm});
            skArc(sketch, "E410.3.265", {"start": v(16.77, -20.81) * mm, "mid": v(16.74, -20.92) * mm, "end": v(16.73, -21.03) * mm});
            skArc(sketch, "E410.3.266", {"start": v(9.3, -14.56) * mm, "mid": v(9.34, -14.6) * mm, "end": v(9.38, -14.64) * mm});
            skArc(sketch, "E410.3.267", {"start": v(16.58, -20.33) * mm, "mid": v(16.6, -20.28) * mm, "end": v(16.64, -20.23) * mm});
            skArc(sketch, "E410.3.268", {"start": v(12.77, -14.46) * mm, "mid": v(12.79, -14.48) * mm, "end": v(12.8, -14.5) * mm});
            skArc(sketch, "E410.3.269", {"start": v(16.03, -19.2) * mm, "mid": v(16.02, -19.22) * mm, "end": v(16, -19.24) * mm});
            skArc(sketch, "E410.3.270", {"start": v(11.08, -16.53) * mm, "mid": v(11.1, -16.55) * mm, "end": v(11.14, -16.56) * mm});
            skArc(sketch, "E410.3.271", {"start": v(16.83, -21.42) * mm, "mid": v(16.84, -21.41) * mm, "end": v(16.85, -21.4) * mm});
            skArc(sketch, "E410.3.272", {"start": v(16.97, -19.98) * mm, "mid": v(16.98, -19.98) * mm, "end": v(17, -19.97) * mm});
            skArc(sketch, "E410.3.273", {"start": v(17.02, -20) * mm, "mid": v(17, -20.05) * mm, "end": v(17, -20.1) * mm});
            skArc(sketch, "E410.3.274", {"start": v(11.36, -16.3) * mm, "mid": v(11.37, -16.26) * mm, "end": v(11.39, -16.22) * mm});
            skArc(sketch, "E410.3.275", {"start": v(17.5, -19.84) * mm, "mid": v(17.54, -19.79) * mm, "end": v(17.57, -19.73) * mm});
            skArc(sketch, "E410.3.276", {"start": v(12.48, -14.78) * mm, "mid": v(12.43, -14.78) * mm, "end": v(12.39, -14.78) * mm});
            skArc(sketch, "E410.3.277", {"start": v(13.67, -15.74) * mm, "mid": v(13.7, -15.74) * mm, "end": v(13.72, -15.75) * mm});
            skArc(sketch, "E410.3.278", {"start": v(16.34, -20.7) * mm, "mid": v(16.37, -20.66) * mm, "end": v(16.4, -20.61) * mm});
            skArc(sketch, "E410.3.279", {"start": v(16.46, -20.52) * mm, "mid": v(16.52, -20.43) * mm, "end": v(16.58, -20.33) * mm});
            skArc(sketch, "E410.3.280", {"start": v(16.07, -19.15) * mm, "mid": v(16.05, -19.18) * mm, "end": v(16.03, -19.2) * mm});
            skArc(sketch, "E410.3.281", {"start": v(16.8, -21.4) * mm, "mid": v(16.82, -21.41) * mm, "end": v(16.83, -21.42) * mm});
            skArc(sketch, "E410.3.282", {"start": v(16.9, -20.03) * mm, "mid": v(16.93, -20) * mm, "end": v(16.97, -19.98) * mm});
            skArc(sketch, "E410.3.283", {"start": v(17.02, -19.98) * mm, "mid": v(17.02, -20) * mm, "end": v(17.02, -20) * mm});
            skArc(sketch, "E410.3.284", {"start": v(12.52, -14.77) * mm, "mid": v(12.5, -14.77) * mm, "end": v(12.48, -14.78) * mm});
            skArc(sketch, "E410.3.285", {"start": v(13.63, -15.76) * mm, "mid": v(13.65, -15.75) * mm, "end": v(13.67, -15.74) * mm});
            skArc(sketch, "E410.3.286", {"start": v(16.09, -19.1) * mm, "mid": v(16.08, -19.13) * mm, "end": v(16.07, -19.15) * mm});
            skArc(sketch, "E410.3.287", {"start": v(16.78, -21.37) * mm, "mid": v(16.79, -21.4) * mm, "end": v(16.8, -21.4) * mm});
            skArc(sketch, "E410.3.288", {"start": v(12.57, -14.73) * mm, "mid": v(12.55, -14.75) * mm, "end": v(12.52, -14.77) * mm});
            skArc(sketch, "E410.3.289", {"start": v(12.84, -18.66) * mm, "mid": v(12.87, -18.59) * mm, "end": v(12.9, -18.53) * mm});
            skArc(sketch, "E410.3.290", {"start": v(11.91, -17.12) * mm, "mid": v(11.84, -17.16) * mm, "end": v(11.77, -17.19) * mm});
            skArc(sketch, "E410.3.291", {"start": v(13.53, -15.79) * mm, "mid": v(13.58, -15.78) * mm, "end": v(13.63, -15.76) * mm});
            skArc(sketch, "E410.3.292", {"start": v(11.16, -18.16) * mm, "mid": v(11.27, -18.3) * mm, "end": v(11.39, -18.46) * mm});
            skArc(sketch, "E410.3.293", {"start": v(12.3, -19.17) * mm, "mid": v(12.34, -19.21) * mm, "end": v(12.39, -19.25) * mm});
            skArc(sketch, "E410.3.294", {"start": v(11.39, -18.46) * mm, "mid": v(11.48, -18.56) * mm, "end": v(11.58, -18.66) * mm});
            skArc(sketch, "E410.3.295", {"start": v(13.13, -18.34) * mm, "mid": v(13.21, -18.28) * mm, "end": v(13.3, -18.22) * mm});
            skArc(sketch, "E410.3.296", {"start": v(11.46, -17.3) * mm, "mid": v(11.42, -17.33) * mm, "end": v(11.37, -17.35) * mm});
            skArc(sketch, "E410.3.297", {"start": v(16.74, -21.25) * mm, "mid": v(16.75, -21.31) * mm, "end": v(16.78, -21.37) * mm});
            skArc(sketch, "E410.3.298", {"start": v(11.3, -17.37) * mm, "mid": v(11.22, -17.38) * mm, "end": v(11.15, -17.4) * mm});
            skArc(sketch, "E410.3.299", {"start": v(11.78, -18.78) * mm, "mid": v(11.79, -18.8) * mm, "end": v(11.8, -18.8) * mm});
            skArc(sketch, "E410.3.300", {"start": v(10.96, -17.52) * mm, "mid": v(10.95, -17.55) * mm, "end": v(10.93, -17.58) * mm});
            skArc(sketch, "E410.3.301", {"start": v(12.77, -19.12) * mm, "mid": v(12.79, -19.07) * mm, "end": v(12.8, -19.02) * mm});
            skArc(sketch, "E410.3.302", {"start": v(12.8, -18.97) * mm, "mid": v(12.79, -18.92) * mm, "end": v(12.79, -18.88) * mm});
            skArc(sketch, "E410.3.303", {"start": v(11.9, -18.74) * mm, "mid": v(11.9, -18.74) * mm, "end": v(11.91, -18.75) * mm});
            skArc(sketch, "E410.3.304", {"start": v(10.93, -17.7) * mm, "mid": v(10.93, -17.74) * mm, "end": v(10.93, -17.78) * mm});
            skArc(sketch, "E410.3.305", {"start": v(12.64, -14.67) * mm, "mid": v(12.6, -14.7) * mm, "end": v(12.57, -14.73) * mm});
            skArc(sketch, "E410.3.306", {"start": v(16.11, -21.38) * mm, "mid": v(16.14, -21.3) * mm, "end": v(16.16, -21.22) * mm});
            skArc(sketch, "E410.3.307", {"start": v(12.8, -18.77) * mm, "mid": v(12.82, -18.71) * mm, "end": v(12.84, -18.66) * mm});
            skArc(sketch, "E410.3.308", {"start": v(12, -17.05) * mm, "mid": v(11.96, -17.08) * mm, "end": v(11.91, -17.12) * mm});
            skArc(sketch, "E410.3.309", {"start": v(11.1, -18.08) * mm, "mid": v(11.13, -18.12) * mm, "end": v(11.16, -18.16) * mm});
            skArc(sketch, "E410.3.310", {"start": v(12.2, -19.07) * mm, "mid": v(12.25, -19.12) * mm, "end": v(12.3, -19.17) * mm});
            skArc(sketch, "E410.3.311", {"start": v(13.05, -18.4) * mm, "mid": v(13.1, -18.37) * mm, "end": v(13.13, -18.34) * mm});
            skArc(sketch, "E410.3.312", {"start": v(11.37, -17.35) * mm, "mid": v(11.33, -17.36) * mm, "end": v(11.3, -17.37) * mm});
            skArc(sketch, "E410.3.313", {"start": v(11.75, -18.75) * mm, "mid": v(11.77, -18.77) * mm, "end": v(11.78, -18.78) * mm});
            skArc(sketch, "E410.3.314", {"start": v(11.07, -17.43) * mm, "mid": v(11, -17.46) * mm, "end": v(10.96, -17.52) * mm});
            skArc(sketch, "E410.3.315", {"start": v(12.73, -19.2) * mm, "mid": v(12.75, -19.16) * mm, "end": v(12.77, -19.12) * mm});
            skArc(sketch, "E410.3.316", {"start": v(12.8, -19.02) * mm, "mid": v(12.8, -19) * mm, "end": v(12.8, -18.97) * mm});
            skArc(sketch, "E410.3.317", {"start": v(11.87, -18.75) * mm, "mid": v(11.88, -18.74) * mm, "end": v(11.9, -18.74) * mm});
            skArc(sketch, "E410.3.318", {"start": v(10.92, -17.63) * mm, "mid": v(10.92, -17.67) * mm, "end": v(10.93, -17.7) * mm});
            skArc(sketch, "E410.3.319", {"start": v(12.79, -18.88) * mm, "mid": v(12.8, -18.83) * mm, "end": v(12.8, -18.77) * mm});
            skArc(sketch, "E410.3.320", {"start": v(11.01, -18) * mm, "mid": v(11.06, -18.04) * mm, "end": v(11.1, -18.08) * mm});
            skArc(sketch, "E410.3.321", {"start": v(12.1, -18.98) * mm, "mid": v(12.15, -19.02) * mm, "end": v(12.2, -19.07) * mm});
            skArc(sketch, "E410.3.322", {"start": v(12.97, -18.47) * mm, "mid": v(13.01, -18.43) * mm, "end": v(13.05, -18.4) * mm});
            skArc(sketch, "E410.3.323", {"start": v(11.55, -17.27) * mm, "mid": v(11.5, -17.29) * mm, "end": v(11.46, -17.3) * mm});
            skArc(sketch, "E410.3.324", {"start": v(11.72, -18.74) * mm, "mid": v(11.74, -18.75) * mm, "end": v(11.75, -18.75) * mm});
            skArc(sketch, "E410.3.325", {"start": v(11.15, -17.4) * mm, "mid": v(11.1, -17.4) * mm, "end": v(11.07, -17.43) * mm});
            skArc(sketch, "E410.3.326", {"start": v(12.66, -19.29) * mm, "mid": v(12.7, -19.25) * mm, "end": v(12.73, -19.2) * mm});
            skArc(sketch, "E410.3.327", {"start": v(11.84, -18.77) * mm, "mid": v(11.86, -18.76) * mm, "end": v(11.87, -18.75) * mm});
            skArc(sketch, "E410.3.328", {"start": v(10.93, -17.58) * mm, "mid": v(10.93, -17.6) * mm, "end": v(10.92, -17.63) * mm});
            skArc(sketch, "E410.3.329", {"start": v(10.97, -17.95) * mm, "mid": v(11, -17.97) * mm, "end": v(11.01, -18) * mm});
            skArc(sketch, "E410.3.330", {"start": v(12.9, -18.53) * mm, "mid": v(12.94, -18.5) * mm, "end": v(12.97, -18.47) * mm});
            skArc(sketch, "E410.3.331", {"start": v(11.66, -17.22) * mm, "mid": v(11.6, -17.24) * mm, "end": v(11.55, -17.27) * mm});
            skArc(sketch, "E410.3.332", {"start": v(11.65, -18.72) * mm, "mid": v(11.69, -18.73) * mm, "end": v(11.72, -18.74) * mm});
            skArc(sketch, "E410.3.333", {"start": v(12.63, -19.32) * mm, "mid": v(12.65, -19.3) * mm, "end": v(12.66, -19.29) * mm});
            skArc(sketch, "E410.3.334", {"start": v(11.8, -18.8) * mm, "mid": v(11.83, -18.79) * mm, "end": v(11.84, -18.77) * mm});
            skArc(sketch, "E410.3.335", {"start": v(10.93, -17.86) * mm, "mid": v(10.95, -17.9) * mm, "end": v(10.97, -17.95) * mm});
            skArc(sketch, "E410.3.336", {"start": v(11.99, -18.87) * mm, "mid": v(12.04, -18.93) * mm, "end": v(12.1, -18.98) * mm});
            skArc(sketch, "E410.3.337", {"start": v(11.58, -18.66) * mm, "mid": v(11.62, -18.7) * mm, "end": v(11.65, -18.72) * mm});
            skArc(sketch, "E410.3.338", {"start": v(12.58, -19.33) * mm, "mid": v(12.6, -19.33) * mm, "end": v(12.63, -19.32) * mm});
            skArc(sketch, "E410.3.339", {"start": v(10.93, -17.78) * mm, "mid": v(10.93, -17.82) * mm, "end": v(10.93, -17.86) * mm});
            skArc(sketch, "E410.3.340", {"start": v(11.93, -18.77) * mm, "mid": v(11.95, -18.82) * mm, "end": v(11.99, -18.87) * mm});
            skArc(sketch, "E410.3.341", {"start": v(12.53, -19.32) * mm, "mid": v(12.55, -19.33) * mm, "end": v(12.58, -19.33) * mm});
            skArc(sketch, "E410.3.342", {"start": v(11.91, -18.75) * mm, "mid": v(11.92, -18.76) * mm, "end": v(11.93, -18.77) * mm});
            skArc(sketch, "E410.3.343", {"start": v(12.44, -19.29) * mm, "mid": v(12.48, -19.3) * mm, "end": v(12.53, -19.32) * mm});
            skArc(sketch, "E410.3.344", {"start": v(15.27, -20.73) * mm, "mid": v(15.27, -20.82) * mm, "end": v(15.27, -20.91) * mm});
            skArc(sketch, "E410.3.345", {"start": v(14.32, -22.03) * mm, "mid": v(14.34, -22.06) * mm, "end": v(14.37, -22.1) * mm});
            skArc(sketch, "E410.3.346", {"start": v(14.67, -21.26) * mm, "mid": v(14.59, -21.24) * mm, "end": v(14.5, -21.25) * mm});
            skArc(sketch, "E410.3.347", {"start": v(16.25, -20.84) * mm, "mid": v(16.3, -20.77) * mm, "end": v(16.34, -20.7) * mm});
            skArc(sketch, "E410.3.348", {"start": v(14.37, -22.1) * mm, "mid": v(14.41, -22.16) * mm, "end": v(14.46, -22.22) * mm});
            skArc(sketch, "E410.3.349", {"start": v(12.39, -19.25) * mm, "mid": v(12.41, -19.27) * mm, "end": v(12.44, -19.29) * mm});
            skArc(sketch, "E410.3.350", {"start": v(15.02, -21.6) * mm, "mid": v(15, -21.62) * mm, "end": v(14.98, -21.64) * mm});
            skArc(sketch, "E410.3.351", {"start": v(14.83, -22.43) * mm, "mid": v(14.9, -22.44) * mm, "end": v(14.96, -22.43) * mm});
            skArc(sketch, "E410.3.352", {"start": v(14.84, -21.7) * mm, "mid": v(14.83, -21.64) * mm, "end": v(14.83, -21.57) * mm});
            skArc(sketch, "E410.3.353", {"start": v(14.96, -22.43) * mm, "mid": v(15.05, -22.4) * mm, "end": v(15.15, -22.38) * mm});
            skArc(sketch, "E410.3.354", {"start": v(15.15, -22.38) * mm, "mid": v(15.26, -22.34) * mm, "end": v(15.38, -22.3) * mm});
            skArc(sketch, "E410.3.355", {"start": v(15.38, -22.3) * mm, "mid": v(15.53, -22.2) * mm, "end": v(15.66, -22.1) * mm});
            skArc(sketch, "E410.3.356", {"start": v(15.4, -20.23) * mm, "mid": v(15.34, -20.38) * mm, "end": v(15.29, -20.53) * mm});
            skArc(sketch, "E410.3.357", {"start": v(14.29, -21.5) * mm, "mid": v(14.3, -21.53) * mm, "end": v(14.3, -21.56) * mm});
            skArc(sketch, "E410.3.358", {"start": v(14.84, -21.41) * mm, "mid": v(14.83, -21.38) * mm, "end": v(14.82, -21.35) * mm});
            skArc(sketch, "E410.3.359", {"start": v(15.29, -20.53) * mm, "mid": v(15.27, -20.63) * mm, "end": v(15.27, -20.73) * mm});
            skArc(sketch, "E410.3.360", {"start": v(15.81, -21.92) * mm, "mid": v(15.93, -21.75) * mm, "end": v(16.03, -21.57) * mm});
            skArc(sketch, "E410.3.361", {"start": v(16.16, -21.22) * mm, "mid": v(16.17, -21.15) * mm, "end": v(16.18, -21.08) * mm});
            skArc(sketch, "E410.3.362", {"start": v(14.29, -21.83) * mm, "mid": v(14.29, -21.87) * mm, "end": v(14.3, -21.92) * mm});
            skArc(sketch, "E410.3.363", {"start": v(15.27, -21.1) * mm, "mid": v(15.26, -21.15) * mm, "end": v(15.26, -21.2) * mm});
            skArc(sketch, "E410.3.364", {"start": v(14.3, -21.92) * mm, "mid": v(14.3, -21.98) * mm, "end": v(14.32, -22.03) * mm});
            skArc(sketch, "E410.3.365", {"start": v(15.26, -21.2) * mm, "mid": v(15.24, -21.27) * mm, "end": v(15.22, -21.33) * mm});
            skArc(sketch, "E410.3.366", {"start": v(16.2, -20.94) * mm, "mid": v(16.23, -20.9) * mm, "end": v(16.25, -20.84) * mm});
            skArc(sketch, "E410.3.367", {"start": v(15.08, -21.56) * mm, "mid": v(15.05, -21.58) * mm, "end": v(15.02, -21.6) * mm});
            skArc(sketch, "E410.3.368", {"start": v(14.7, -22.4) * mm, "mid": v(14.77, -22.43) * mm, "end": v(14.83, -22.43) * mm});
            skArc(sketch, "E410.3.369", {"start": v(14.87, -21.72) * mm, "mid": v(14.85, -21.72) * mm, "end": v(14.84, -21.7) * mm});
            skArc(sketch, "E410.3.370", {"start": v(14.3, -21.46) * mm, "mid": v(14.29, -21.48) * mm, "end": v(14.29, -21.5) * mm});
            skArc(sketch, "E410.3.371", {"start": v(14.84, -21.46) * mm, "mid": v(14.84, -21.44) * mm, "end": v(14.84, -21.41) * mm});
            skArc(sketch, "E410.3.372", {"start": v(15.66, -22.1) * mm, "mid": v(15.74, -22.01) * mm, "end": v(15.81, -21.92) * mm});
            skArc(sketch, "E410.3.373", {"start": v(16.03, -21.57) * mm, "mid": v(16.08, -21.48) * mm, "end": v(16.11, -21.38) * mm});
            skArc(sketch, "E410.3.374", {"start": v(14.3, -21.65) * mm, "mid": v(14.29, -21.74) * mm, "end": v(14.29, -21.83) * mm});
            skArc(sketch, "E410.3.375", {"start": v(15.27, -20.91) * mm, "mid": v(15.28, -21) * mm, "end": v(15.27, -21.1) * mm});
            skArc(sketch, "E410.3.376", {"start": v(16.18, -21.08) * mm, "mid": v(16.19, -21.01) * mm, "end": v(16.2, -20.94) * mm});
            skArc(sketch, "E410.3.377", {"start": v(15.17, -21.45) * mm, "mid": v(15.13, -21.51) * mm, "end": v(15.08, -21.56) * mm});
            skArc(sketch, "E410.3.378", {"start": v(14.56, -22.32) * mm, "mid": v(14.63, -22.37) * mm, "end": v(14.7, -22.4) * mm});
            skArc(sketch, "E410.3.379", {"start": v(14.9, -21.71) * mm, "mid": v(14.88, -21.72) * mm, "end": v(14.87, -21.72) * mm});
            skArc(sketch, "E410.3.380", {"start": v(14.3, -21.44) * mm, "mid": v(14.3, -21.45) * mm, "end": v(14.3, -21.46) * mm});
            skArc(sketch, "E410.3.381", {"start": v(14.84, -21.52) * mm, "mid": v(14.84, -21.49) * mm, "end": v(14.84, -21.46) * mm});
            skArc(sketch, "E410.3.382", {"start": v(14.3, -21.56) * mm, "mid": v(14.3, -21.6) * mm, "end": v(14.3, -21.65) * mm});
            skArc(sketch, "E410.3.383", {"start": v(15.22, -21.33) * mm, "mid": v(15.2, -21.4) * mm, "end": v(15.17, -21.45) * mm});
            skArc(sketch, "E410.3.384", {"start": v(14.51, -22.28) * mm, "mid": v(14.53, -22.3) * mm, "end": v(14.56, -22.32) * mm});
            skArc(sketch, "E410.3.385", {"start": v(14.98, -21.64) * mm, "mid": v(14.94, -21.68) * mm, "end": v(14.9, -21.71) * mm});
            skArc(sketch, "E410.3.386", {"start": v(14.33, -21.42) * mm, "mid": v(14.32, -21.43) * mm, "end": v(14.3, -21.44) * mm});
            skArc(sketch, "E410.3.387", {"start": v(14.83, -21.57) * mm, "mid": v(14.83, -21.54) * mm, "end": v(14.84, -21.52) * mm});
            skArc(sketch, "E410.3.388", {"start": v(14.46, -22.22) * mm, "mid": v(14.49, -22.25) * mm, "end": v(14.51, -22.28) * mm});
            skArc(sketch, "E410.3.389", {"start": v(14.35, -21.4) * mm, "mid": v(14.34, -21.41) * mm, "end": v(14.33, -21.42) * mm});
            skArc(sketch, "E410.3.390", {"start": v(14.37, -21.38) * mm, "mid": v(14.36, -21.39) * mm, "end": v(14.35, -21.4) * mm});
            skArc(sketch, "E410.3.391", {"start": v(14.38, -21.36) * mm, "mid": v(14.37, -21.37) * mm, "end": v(14.37, -21.38) * mm});
            skArc(sketch, "E410.3.392", {"start": v(14.4, -21.35) * mm, "mid": v(14.4, -21.36) * mm, "end": v(14.38, -21.36) * mm});
            skArc(sketch, "E410.3.393", {"start": v(14.43, -21.31) * mm, "mid": v(14.42, -21.33) * mm, "end": v(14.4, -21.35) * mm});
            skArc(sketch, "E410.3.394", {"start": v(14.45, -21.27) * mm, "mid": v(14.44, -21.3) * mm, "end": v(14.43, -21.31) * mm});
            skArc(sketch, "E410.3.395", {"start": v(14.5, -21.25) * mm, "mid": v(14.47, -21.25) * mm, "end": v(14.45, -21.27) * mm});
            skArc(sketch, "E410.3.396", {"start": v(14.74, -21.27) * mm, "mid": v(14.7, -21.26) * mm, "end": v(14.67, -21.26) * mm});
            skArc(sketch, "E410.3.397", {"start": v(14.77, -21.29) * mm, "mid": v(14.75, -21.28) * mm, "end": v(14.74, -21.27) * mm});
            skArc(sketch, "E410.3.398", {"start": v(14.8, -21.3) * mm, "mid": v(14.78, -21.3) * mm, "end": v(14.77, -21.29) * mm});
            skArc(sketch, "E410.3.399", {"start": v(14.82, -21.35) * mm, "mid": v(14.8, -21.33) * mm, "end": v(14.8, -21.3) * mm});
            skPoint(sketch, "E410.center", {"position": v(0, 0) * mm});
            skSolve(sketch);
        }
        {
            var Q0;
            Q0=makeQuery(id+"F3.imprint","IMPRINT",FACE,{"disambiguationData":[TD([[makeQuery(id+"F3.imprint","IMPRINT",EDGE,{"derivedFrom":sQuery(id+"F3.wireOp",EDGE,"E10")}),1.0]])]});
            var Q1;
            Q1=makeQuery(id+"F3.imprint","IMPRINT",FACE,{"disambiguationData":[TD([[makeQuery(id+"F3.imprint","IMPRINT",EDGE,{"derivedFrom":sQuery(id+"F3.wireOp",EDGE,"E410.3.0")}),1.0]])]});
            var Q2;
            Q2=makeQuery(id+"F3.imprint","IMPRINT",FACE,{"disambiguationData":[TD([[makeQuery(id+"F3.imprint","IMPRINT",EDGE,{"derivedFrom":sQuery(id+"F3.wireOp",EDGE,"E410.2.0")}),1.0]])]});
            var Q3;
            Q3=makeQuery(id+"F3.imprint","IMPRINT",FACE,{"disambiguationData":[TD([[makeQuery(id+"F3.imprint","IMPRINT",EDGE,{"derivedFrom":sQuery(id+"F3.wireOp",EDGE,"E410.1.0")}),1.0]])]});
            extrude(context, id + "F4", {"entities" : qUnion([Q0, Q1, Q2, Q3]), "operationType" : NewBodyOperationType.REMOVE, "oppositeDirection" : true, "depth" : 25.4 * mm, "offsetDistance" : 25.4 * mm});
        }
        {
            var Q0;
            Q0=makeQuery(id+"F2.opExtrude","CAP_EDGE",EDGE,{"disambiguationData":[OSD([sQuery(id+"F0.wireOp",EDGE,"E3.3")])],"isStart":false});
            var Q1;
            Q1=makeQuery(id+"F2.opExtrude","CAP_EDGE",EDGE,{"disambiguationData":[OSD([sQuery(id+"F0.wireOp",EDGE,"E3.4")])],"isStart":false});
            var Q2;
            Q2=makeQuery(id+"F2.opExtrude","CAP_EDGE",EDGE,{"disambiguationData":[OSD([sQuery(id+"F1.wireOp",EDGE,"E7")])],"isStart":false});
            var Q3;
            Q3=makeQuery(id+"F2.opExtrude","CAP_EDGE",EDGE,{"disambiguationData":[OSD([sQuery(id+"F0.wireOp",EDGE,"E4.3.6")])],"isStart":false});
            var Q4;
            Q4=makeQuery(id+"F2.opExtrude","CAP_EDGE",EDGE,{"disambiguationData":[OSD([sQuery(id+"F0.wireOp",EDGE,"E4.3.9")])],"isStart":false});
            var Q5;
            Q5=makeQuery(id+"F2.opExtrude","CAP_EDGE",EDGE,{"disambiguationData":[OSD([sQuery(id+"F0.wireOp",EDGE,"E4.3.0")])],"isStart":false});
            var Q6;
            Q6=makeQuery(id+"F2.opExtrude","CAP_EDGE",EDGE,{"disambiguationData":[OSD([sQuery(id+"F1.wireOp",EDGE,"E8")])],"isStart":false});
            var Q7;
            Q7=makeQuery(id+"F2.opExtrude","CAP_EDGE",EDGE,{"disambiguationData":[OSD([sQuery(id+"F0.wireOp",EDGE,"E4.2.6")])],"isStart":false});
            var Q8;
            Q8=makeQuery(id+"F2.opExtrude","CAP_EDGE",EDGE,{"disambiguationData":[OSD([sQuery(id+"F0.wireOp",EDGE,"E4.2.9")])],"isStart":false});
            var Q9;
            Q9=makeQuery(id+"F2.opExtrude","CAP_EDGE",EDGE,{"disambiguationData":[OSD([sQuery(id+"F0.wireOp",EDGE,"E4.2.0")])],"isStart":false});
            var Q10;
            Q10=makeQuery(id+"F2.opExtrude","CAP_EDGE",EDGE,{"disambiguationData":[OSD([sQuery(id+"F1.wireOp",EDGE,"E9")])],"isStart":false});
            var Q11;
            Q11=makeQuery(id+"F2.opExtrude","CAP_EDGE",EDGE,{"disambiguationData":[OSD([sQuery(id+"F0.wireOp",EDGE,"E4.1.6")])],"isStart":false});
            var Q12;
            Q12=makeQuery(id+"F2.opExtrude","CAP_EDGE",EDGE,{"disambiguationData":[OSD([sQuery(id+"F0.wireOp",EDGE,"E4.1.9")])],"isStart":false});
            var Q13;
            Q13=makeQuery(id+"F2.opExtrude","CAP_EDGE",EDGE,{"disambiguationData":[OSD([sQuery(id+"F0.wireOp",EDGE,"E4.1.0")])],"isStart":false});
            var Q14;
            Q14=makeQuery(id+"F2.opExtrude","CAP_EDGE",EDGE,{"disambiguationData":[OSD([sQuery(id+"F1.wireOp",EDGE,"E6")])],"isStart":false});
            var Q15;
            Q15=makeQuery(id+"F2.opExtrude","CAP_EDGE",EDGE,{"disambiguationData":[OSD([sQuery(id+"F0.wireOp",EDGE,"E3.2")])],"isStart":false});
            var Q16;
            Q16=makeQuery(id+"F2.opExtrude","CAP_EDGE",EDGE,{"disambiguationData":[OSD([sQuery(id+"F0.wireOp",EDGE,"E3.2")])],"isStart":true});
            var Q17;
            Q17=makeQuery(id+"F2.opExtrude","CAP_EDGE",EDGE,{"disambiguationData":[OSD([sQuery(id+"F0.wireOp",EDGE,"E3.3")])],"isStart":true});
            var Q18;
            Q18=makeQuery(id+"F2.opExtrude","CAP_EDGE",EDGE,{"disambiguationData":[OSD([sQuery(id+"F0.wireOp",EDGE,"E3.4")])],"isStart":true});
            var Q19;
            Q19=makeQuery(id+"F2.opExtrude","CAP_EDGE",EDGE,{"disambiguationData":[OSD([sQuery(id+"F1.wireOp",EDGE,"E7")])],"isStart":true});
            var Q20;
            Q20=makeQuery(id+"F2.opExtrude","CAP_EDGE",EDGE,{"disambiguationData":[OSD([sQuery(id+"F0.wireOp",EDGE,"E4.3.6")])],"isStart":true});
            var Q21;
            Q21=makeQuery(id+"F2.opExtrude","CAP_EDGE",EDGE,{"disambiguationData":[OSD([sQuery(id+"F0.wireOp",EDGE,"E4.3.9")])],"isStart":true});
            var Q22;
            Q22=makeQuery(id+"F2.opExtrude","CAP_EDGE",EDGE,{"disambiguationData":[OSD([sQuery(id+"F0.wireOp",EDGE,"E4.3.0")])],"isStart":true});
            var Q23;
            Q23=makeQuery(id+"F2.opExtrude","CAP_EDGE",EDGE,{"disambiguationData":[OSD([sQuery(id+"F1.wireOp",EDGE,"E8")])],"isStart":true});
            var Q24;
            Q24=makeQuery(id+"F2.opExtrude","CAP_EDGE",EDGE,{"disambiguationData":[OSD([sQuery(id+"F0.wireOp",EDGE,"E4.2.6")])],"isStart":true});
            var Q25;
            Q25=makeQuery(id+"F2.opExtrude","CAP_EDGE",EDGE,{"disambiguationData":[OSD([sQuery(id+"F0.wireOp",EDGE,"E4.2.9")])],"isStart":true});
            var Q26;
            Q26=makeQuery(id+"F2.opExtrude","CAP_EDGE",EDGE,{"disambiguationData":[OSD([sQuery(id+"F0.wireOp",EDGE,"E4.2.0")])],"isStart":true});
            var Q27;
            Q27=makeQuery(id+"F2.opExtrude","CAP_EDGE",EDGE,{"disambiguationData":[OSD([sQuery(id+"F1.wireOp",EDGE,"E9")])],"isStart":true});
            var Q28;
            Q28=makeQuery(id+"F2.opExtrude","CAP_EDGE",EDGE,{"disambiguationData":[OSD([sQuery(id+"F0.wireOp",EDGE,"E4.1.9")])],"isStart":true});
            var Q29;
            Q29=makeQuery(id+"F2.opExtrude","CAP_EDGE",EDGE,{"disambiguationData":[OSD([sQuery(id+"F0.wireOp",EDGE,"E4.1.6")])],"isStart":true});
            var Q30;
            Q30=makeQuery(id+"F2.opExtrude","CAP_EDGE",EDGE,{"disambiguationData":[OSD([sQuery(id+"F0.wireOp",EDGE,"E4.1.0")])],"isStart":true});
            var Q31;
            Q31=makeQuery(id+"F2.opExtrude","CAP_EDGE",EDGE,{"disambiguationData":[OSD([sQuery(id+"F1.wireOp",EDGE,"E6")])],"isStart":true});
            fillet(context, id + "F5", {"entities" : qUnion([Q0, Q1, Q2, Q3, Q4, Q5, Q6, Q7, Q8, Q9, Q10, Q11, Q12, Q13, Q14, Q15, Q16, Q17, Q18, Q19, Q20, Q21, Q22, Q23, Q24, Q25, Q26, Q27, Q28, Q29, Q30, Q31]), "radius" : 3.17 * mm, "tangentPropagation" : true, "allowEdgeOverflow" : false});
        }
    });
